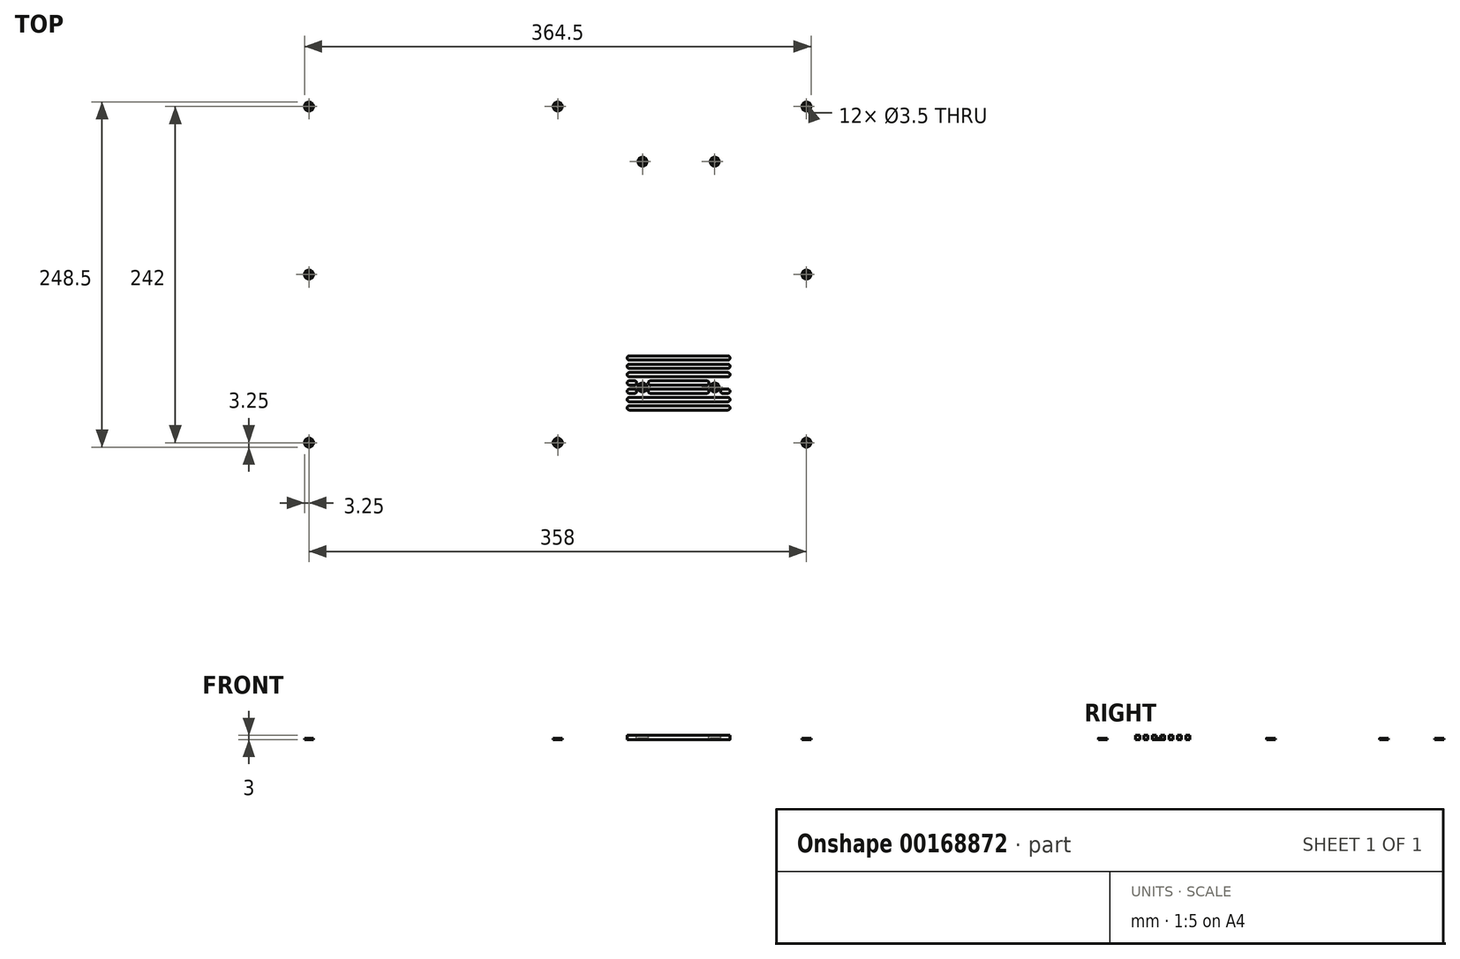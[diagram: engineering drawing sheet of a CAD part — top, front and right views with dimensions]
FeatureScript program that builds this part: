
annotation { "Feature Type Name" : "Feature", "Feature Type Description" : "" }
export const myFeature = defineFeature(function(context is Context, id is Id, definition is map)
    precondition{}
    {
        {
            var Q0;
            Q0=qCreatedBy(makeId("Top.planeOp"),FACE);
            var sketch = newSketch(context, id + "F0", { "sketchPlane" : qUnion([Q0])});
            skLineSegment(sketch, "E0.bottom", {"start": v(184, -126) * mm, "end": v(-184, -126) * mm});
            skLineSegment(sketch, "E0.top", {"start": v(184, 126) * mm, "end": v(-184, 126) * mm});
            skLineSegment(sketch, "E0.left", {"start": v(184, -126) * mm, "end": v(184, 126) * mm});
            skLineSegment(sketch, "E0.right", {"start": v(-184, -126) * mm, "end": v(-184, 126) * mm});
            skPoint(sketch, "E0.middle", {"position": v(0, 0) * mm});
            skLineSegment(sketch, "E1", {"start": v(-123, 245.59) * mm, "end": v(-123, -157.27) * mm, "construction": true});
            skLineSegment(sketch, "E2", {"start": v(-74.74, 270.76) * mm, "end": v(-74.74, -144.34) * mm, "construction": true});
            skLineSegment(sketch, "E3", {"start": v(-26.48, 143.4) * mm, "end": v(-26.48, -157.27) * mm, "construction": true});
            skLineSegment(sketch, "E4", {"start": v(-203.28, 67.26) * mm, "end": v(180.7, 67.26) * mm, "construction": true});
            skLineSegment(sketch, "E5", {"start": v(-202.8, 48.2) * mm, "end": v(185.48, 48.21) * mm, "construction": true});
            skLineSegment(sketch, "E6", {"start": v(-209.03, 29.16) * mm, "end": v(184.53, 29.16) * mm, "construction": true});
            skLineSegment(sketch, "E7.MirrorCS", {"start": v(-209.03, -29.16) * mm, "end": v(184.53, -29.16) * mm, "construction": true});
            skLineSegment(sketch, "E8.MirrorCS", {"start": v(-202.8, -48.2) * mm, "end": v(185.48, -48.21) * mm, "construction": true});
            skLineSegment(sketch, "E9.MirrorCS", {"start": v(-203.28, -67.26) * mm, "end": v(180.7, -67.26) * mm, "construction": true});
            skCircle(sketch, "E10", {"center": v(-123, 29.16) * mm, "radius": 11 * mm});
            skCircle(sketch, "E11", {"center": v(-74.74, 48.21) * mm, "radius": 11 * mm});
            skCircle(sketch, "E12", {"center": v(-123, -29.16) * mm, "radius": 11 * mm});
            skCircle(sketch, "E13", {"center": v(-74.74, -48.21) * mm, "radius": 11 * mm});
            skCircle(sketch, "E14", {"center": v(-26.48, -67.26) * mm, "radius": 11 * mm});
            skCircle(sketch, "E15", {"center": v(-26.48, 67.26) * mm, "radius": 11 * mm});
            skLineSegment(sketch, "E16.bottom", {"start": v(113, -39.5) * mm, "end": v(61, -39.5) * mm});
            skLineSegment(sketch, "E16.top", {"start": v(113, 39.5) * mm, "end": v(61, 39.5) * mm});
            skLineSegment(sketch, "E16.left", {"start": v(113, -39.5) * mm, "end": v(113, 39.5) * mm});
            skLineSegment(sketch, "E16.right", {"start": v(61, -39.5) * mm, "end": v(61, 39.5) * mm});
            skPoint(sketch, "E16.middle", {"position": v(87, 0) * mm});
            skLineSegment(sketch, "E17", {"start": v(55, 135.82) * mm, "end": v(55, -139) * mm, "construction": true});
            skLineSegment(sketch, "E18", {"start": v(119, 132.87) * mm, "end": v(119, -141.2) * mm, "construction": true});
            skLineSegment(sketch, "E19", {"start": v(35.75, 38) * mm, "end": v(185.31, 38) * mm, "construction": true});
            skLineSegment(sketch, "E20.MirrorCS", {"start": v(35.75, -38) * mm, "end": v(185.31, -38) * mm, "construction": true});
            skCircle(sketch, "E21", {"center": v(55, 38) * mm, "radius": 2.25 * mm});
            skCircle(sketch, "E22", {"center": v(119, 38) * mm, "radius": 2.25 * mm});
            skCircle(sketch, "E23", {"center": v(55, -38) * mm, "radius": 2.25 * mm});
            skCircle(sketch, "E24", {"center": v(119, -38) * mm, "radius": 2.25 * mm});
            skLineSegment(sketch, "E25", {"start": v(-171.66, 121) * mm, "end": v(177.1, 121) * mm, "construction": true});
            skLineSegment(sketch, "E26", {"start": v(-179, -132.6) * mm, "end": v(-179, 126) * mm, "construction": true});
            skLineSegment(sketch, "E27.MirrorCS", {"start": v(179, -132.6) * mm, "end": v(179, 126) * mm, "construction": true});
            skLineSegment(sketch, "E28.MirrorCS", {"start": v(-171.66, -121) * mm, "end": v(177.1, -121) * mm, "construction": true});
            skLineSegment(sketch, "E29", {"start": v(0, 148.7) * mm, "end": v(0, -121) * mm, "construction": true});
            skPoint(sketch, "E29.startSnap0", {"position": v(0, 126) * mm});
            skPoint(sketch, "E29.endSnap0", {"position": v(2.72, -121) * mm});
            skLineSegment(sketch, "E30", {"start": v(-194.49, 0) * mm, "end": v(184.92, 0) * mm, "construction": true});
            skPoint(sketch, "E30.startSnap0", {"position": v(-184, 0) * mm});
            skPoint(sketch, "E30.endSnap0", {"position": v(113, 0) * mm});
            skPoint(sketch, "E31", {"position": v(-179, 121) * mm});
            skPoint(sketch, "E32", {"position": v(0, 121) * mm});
            skPoint(sketch, "E33", {"position": v(-179, 0) * mm});
            skPoint(sketch, "E34", {"position": v(179, 121) * mm});
            skPoint(sketch, "E35", {"position": v(179, 0) * mm});
            skPoint(sketch, "E36", {"position": v(179, -121) * mm});
            skPoint(sketch, "E37", {"position": v(0, -121) * mm});
            skPoint(sketch, "E38", {"position": v(-179, -121) * mm});
            skLineSegment(sketch, "E39.bottom", {"start": v(-123, 50.16) * mm, "end": v(-123, 50.16) * mm});
            skLineSegment(sketch, "E39.top", {"start": v(-123, 43.16) * mm, "end": v(-123, 43.16) * mm});
            skLineSegment(sketch, "E39.left", {"start": v(-124, 49.16) * mm, "end": v(-124, 44.16) * mm});
            skLineSegment(sketch, "E39.right", {"start": v(-122, 49.16) * mm, "end": v(-122, 44.16) * mm});
            skPoint(sketch, "E40.visualSharp", {"position": v(-124, 50.16) * mm});
            skArc(sketch, "E40.filletArc", {"start": v(-123, 50.16) * mm, "mid": v(-123.7, 49.87) * mm, "end": v(-124, 49.16) * mm});
            skPoint(sketch, "E41.visualSharp", {"position": v(-122, 50.16) * mm});
            skArc(sketch, "E41.filletArc", {"start": v(-122, 49.16) * mm, "mid": v(-122.3, 49.87) * mm, "end": v(-123, 50.16) * mm});
            skPoint(sketch, "E42.visualSharp", {"position": v(-122, 43.16) * mm});
            skArc(sketch, "E42.filletArc", {"start": v(-123, 43.16) * mm, "mid": v(-122.3, 43.45) * mm, "end": v(-122, 44.16) * mm});
            skPoint(sketch, "E43.visualSharp", {"position": v(-124, 43.16) * mm});
            skArc(sketch, "E43.filletArc", {"start": v(-124, 44.16) * mm, "mid": v(-123.7, 43.45) * mm, "end": v(-123, 43.16) * mm});
            skLineSegment(sketch, "E44.bottom", {"start": v(-74.74, 69.21) * mm, "end": v(-74.74, 69.21) * mm});
            skLineSegment(sketch, "E44.top", {"start": v(-74.74, 62.21) * mm, "end": v(-74.74, 62.21) * mm});
            skLineSegment(sketch, "E44.left", {"start": v(-75.74, 68.21) * mm, "end": v(-75.74, 63.21) * mm});
            skLineSegment(sketch, "E44.right", {"start": v(-73.74, 68.21) * mm, "end": v(-73.74, 63.21) * mm});
            skPoint(sketch, "E45.visualSharp", {"position": v(-75.74, 69.21) * mm});
            skArc(sketch, "E45.filletArc", {"start": v(-74.74, 69.21) * mm, "mid": v(-75.45, 68.92) * mm, "end": v(-75.74, 68.21) * mm});
            skPoint(sketch, "E46.visualSharp", {"position": v(-73.74, 69.21) * mm});
            skArc(sketch, "E46.filletArc", {"start": v(-73.74, 68.21) * mm, "mid": v(-74.03, 68.92) * mm, "end": v(-74.74, 69.21) * mm});
            skPoint(sketch, "E47.visualSharp", {"position": v(-73.74, 62.21) * mm});
            skArc(sketch, "E47.filletArc", {"start": v(-74.74, 62.21) * mm, "mid": v(-74.03, 62.5) * mm, "end": v(-73.74, 63.21) * mm});
            skPoint(sketch, "E48.visualSharp", {"position": v(-75.74, 62.21) * mm});
            skArc(sketch, "E48.filletArc", {"start": v(-75.74, 63.21) * mm, "mid": v(-75.45, 62.5) * mm, "end": v(-74.74, 62.21) * mm});
            skLineSegment(sketch, "E49.bottom", {"start": v(-26.48, 88.26) * mm, "end": v(-26.48, 88.26) * mm});
            skLineSegment(sketch, "E49.top", {"start": v(-26.48, 81.26) * mm, "end": v(-26.48, 81.26) * mm});
            skLineSegment(sketch, "E49.left", {"start": v(-27.48, 87.26) * mm, "end": v(-27.48, 82.26) * mm});
            skLineSegment(sketch, "E49.right", {"start": v(-25.48, 87.26) * mm, "end": v(-25.48, 82.26) * mm});
            skPoint(sketch, "E50.visualSharp", {"position": v(-27.48, 88.26) * mm});
            skArc(sketch, "E50.filletArc", {"start": v(-26.48, 88.26) * mm, "mid": v(-27.19, 87.97) * mm, "end": v(-27.48, 87.26) * mm});
            skPoint(sketch, "E51.visualSharp", {"position": v(-25.48, 88.26) * mm});
            skArc(sketch, "E51.filletArc", {"start": v(-25.48, 87.26) * mm, "mid": v(-25.77, 87.97) * mm, "end": v(-26.48, 88.26) * mm});
            skPoint(sketch, "E52.visualSharp", {"position": v(-25.48, 81.26) * mm});
            skArc(sketch, "E52.filletArc", {"start": v(-26.48, 81.26) * mm, "mid": v(-25.77, 81.55) * mm, "end": v(-25.48, 82.26) * mm});
            skPoint(sketch, "E53.visualSharp", {"position": v(-27.48, 81.26) * mm});
            skArc(sketch, "E53.filletArc", {"start": v(-27.48, 82.26) * mm, "mid": v(-27.19, 81.55) * mm, "end": v(-26.48, 81.26) * mm});
            skLineSegment(sketch, "E54.bottom", {"start": v(-26.48, -46.26) * mm, "end": v(-26.48, -46.26) * mm});
            skLineSegment(sketch, "E54.top", {"start": v(-26.48, -53.26) * mm, "end": v(-26.48, -53.26) * mm});
            skLineSegment(sketch, "E54.left", {"start": v(-27.48, -47.26) * mm, "end": v(-27.48, -52.26) * mm});
            skLineSegment(sketch, "E54.right", {"start": v(-25.48, -47.26) * mm, "end": v(-25.48, -52.26) * mm});
            skPoint(sketch, "E55.visualSharp", {"position": v(-27.48, -46.26) * mm});
            skArc(sketch, "E55.filletArc", {"start": v(-26.48, -46.26) * mm, "mid": v(-27.19, -46.55) * mm, "end": v(-27.48, -47.26) * mm});
            skPoint(sketch, "E56.visualSharp", {"position": v(-25.48, -46.26) * mm});
            skArc(sketch, "E56.filletArc", {"start": v(-25.48, -47.26) * mm, "mid": v(-25.77, -46.55) * mm, "end": v(-26.48, -46.26) * mm});
            skPoint(sketch, "E57.visualSharp", {"position": v(-25.48, -53.26) * mm});
            skArc(sketch, "E57.filletArc", {"start": v(-26.48, -53.26) * mm, "mid": v(-25.77, -52.97) * mm, "end": v(-25.48, -52.26) * mm});
            skPoint(sketch, "E58.visualSharp", {"position": v(-27.48, -53.26) * mm});
            skArc(sketch, "E58.filletArc", {"start": v(-27.48, -52.26) * mm, "mid": v(-27.19, -52.97) * mm, "end": v(-26.48, -53.26) * mm});
            skLineSegment(sketch, "E59.bottom", {"start": v(-74.74, -27.21) * mm, "end": v(-74.74, -27.21) * mm});
            skLineSegment(sketch, "E59.top", {"start": v(-74.74, -34.21) * mm, "end": v(-74.74, -34.21) * mm});
            skLineSegment(sketch, "E59.left", {"start": v(-75.74, -28.21) * mm, "end": v(-75.74, -33.21) * mm});
            skLineSegment(sketch, "E59.right", {"start": v(-73.74, -28.21) * mm, "end": v(-73.74, -33.21) * mm});
            skPoint(sketch, "E60.visualSharp", {"position": v(-75.74, -27.21) * mm});
            skArc(sketch, "E60.filletArc", {"start": v(-74.74, -27.21) * mm, "mid": v(-75.45, -27.5) * mm, "end": v(-75.74, -28.21) * mm});
            skPoint(sketch, "E61.visualSharp", {"position": v(-73.74, -27.21) * mm});
            skArc(sketch, "E61.filletArc", {"start": v(-73.74, -28.21) * mm, "mid": v(-74.03, -27.5) * mm, "end": v(-74.74, -27.21) * mm});
            skPoint(sketch, "E62.visualSharp", {"position": v(-73.74, -34.21) * mm});
            skArc(sketch, "E62.filletArc", {"start": v(-74.74, -34.21) * mm, "mid": v(-74.03, -33.92) * mm, "end": v(-73.74, -33.21) * mm});
            skPoint(sketch, "E63.visualSharp", {"position": v(-75.74, -34.21) * mm});
            skArc(sketch, "E63.filletArc", {"start": v(-75.74, -33.21) * mm, "mid": v(-75.45, -33.92) * mm, "end": v(-74.74, -34.21) * mm});
            skLineSegment(sketch, "E64.bottom", {"start": v(-123, -8.16) * mm, "end": v(-123, -8.16) * mm});
            skLineSegment(sketch, "E64.top", {"start": v(-123, -15.16) * mm, "end": v(-123, -15.16) * mm});
            skLineSegment(sketch, "E64.left", {"start": v(-124, -9.16) * mm, "end": v(-124, -14.16) * mm});
            skLineSegment(sketch, "E64.right", {"start": v(-122, -9.16) * mm, "end": v(-122, -14.16) * mm});
            skPoint(sketch, "E65.visualSharp", {"position": v(-124, -8.16) * mm});
            skArc(sketch, "E65.filletArc", {"start": v(-123, -8.16) * mm, "mid": v(-123.7, -8.45) * mm, "end": v(-124, -9.16) * mm});
            skPoint(sketch, "E66.visualSharp", {"position": v(-122, -8.16) * mm});
            skArc(sketch, "E66.filletArc", {"start": v(-122, -9.16) * mm, "mid": v(-122.3, -8.45) * mm, "end": v(-123, -8.16) * mm});
            skPoint(sketch, "E67.visualSharp", {"position": v(-122, -15.16) * mm});
            skArc(sketch, "E67.filletArc", {"start": v(-123, -15.16) * mm, "mid": v(-122.3, -14.87) * mm, "end": v(-122, -14.16) * mm});
            skPoint(sketch, "E68.visualSharp", {"position": v(-124, -15.16) * mm});
            skArc(sketch, "E68.filletArc", {"start": v(-124, -14.16) * mm, "mid": v(-123.7, -14.87) * mm, "end": v(-123, -15.16) * mm});
            skLineSegment(sketch, "E69.1.0", {"start": v(-128.23, 48.5) * mm, "end": v(-126.68, 43.73) * mm});
            skArc(sketch, "E69.1.1", {"start": v(-128.59, 43.12) * mm, "mid": v(-128.09, 42.53) * mm, "end": v(-127.33, 42.47) * mm});
            skPoint(sketch, "E69.1.2", {"position": v(-126.38, 42.78) * mm});
            skArc(sketch, "E69.1.3", {"start": v(-127.33, 42.47) * mm, "mid": v(-126.74, 42.97) * mm, "end": v(-126.68, 43.73) * mm});
            skPoint(sketch, "E69.1.4", {"position": v(-128.28, 42.17) * mm});
            skLineSegment(sketch, "E69.1.5", {"start": v(-130.13, 47.87) * mm, "end": v(-128.59, 43.12) * mm});
            skPoint(sketch, "E69.1.6", {"position": v(-130.44, 48.82) * mm});
            skArc(sketch, "E69.1.7", {"start": v(-129.49, 49.13) * mm, "mid": v(-130.07, 48.64) * mm, "end": v(-130.13, 47.87) * mm});
            skPoint(sketch, "E69.1.8", {"position": v(-128.54, 49.44) * mm});
            skArc(sketch, "E69.1.9", {"start": v(-128.23, 48.5) * mm, "mid": v(-128.73, 49.07) * mm, "end": v(-129.49, 49.13) * mm});
            skLineSegment(sketch, "E69.2.0", {"start": v(-133.95, 45.93) * mm, "end": v(-131, 41.88) * mm});
            skArc(sketch, "E69.2.1", {"start": v(-132.63, 40.7) * mm, "mid": v(-131.97, 40.3) * mm, "end": v(-131.23, 40.49) * mm});
            skPoint(sketch, "E69.2.2", {"position": v(-130.42, 41.07) * mm});
            skArc(sketch, "E69.2.3", {"start": v(-131.23, 40.49) * mm, "mid": v(-130.83, 41.14) * mm, "end": v(-131, 41.88) * mm});
            skPoint(sketch, "E69.2.4", {"position": v(-132.04, 39.9) * mm});
            skLineSegment(sketch, "E69.2.5", {"start": v(-135.56, 44.75) * mm, "end": v(-132.63, 40.7) * mm});
            skPoint(sketch, "E69.2.6", {"position": v(-136.15, 45.56) * mm});
            skArc(sketch, "E69.2.7", {"start": v(-135.34, 46.15) * mm, "mid": v(-135.74, 45.5) * mm, "end": v(-135.56, 44.75) * mm});
            skPoint(sketch, "E69.2.8", {"position": v(-134.53, 46.74) * mm});
            skArc(sketch, "E69.2.9", {"start": v(-133.95, 45.93) * mm, "mid": v(-134.6, 46.33) * mm, "end": v(-135.34, 46.15) * mm});
            skLineSegment(sketch, "E69.3.0", {"start": v(-138.6, 41.72) * mm, "end": v(-134.55, 38.79) * mm});
            skArc(sketch, "E69.3.1", {"start": v(-135.72, 37.17) * mm, "mid": v(-134.98, 36.99) * mm, "end": v(-134.33, 37.39) * mm});
            skPoint(sketch, "E69.3.2", {"position": v(-133.74, 38.2) * mm});
            skArc(sketch, "E69.3.3", {"start": v(-134.33, 37.39) * mm, "mid": v(-134.15, 38.13) * mm, "end": v(-134.55, 38.79) * mm});
            skPoint(sketch, "E69.3.4", {"position": v(-134.91, 36.58) * mm});
            skLineSegment(sketch, "E69.3.5", {"start": v(-139.77, 40.1) * mm, "end": v(-135.72, 37.17) * mm});
            skPoint(sketch, "E69.3.6", {"position": v(-140.58, 40.7) * mm});
            skArc(sketch, "E69.3.7", {"start": v(-139.99, 41.5) * mm, "mid": v(-140.17, 40.76) * mm, "end": v(-139.77, 40.1) * mm});
            skPoint(sketch, "E69.3.8", {"position": v(-139.4, 42.31) * mm});
            skArc(sketch, "E69.3.9", {"start": v(-138.6, 41.72) * mm, "mid": v(-139.34, 41.9) * mm, "end": v(-139.99, 41.5) * mm});
            skLineSegment(sketch, "E69.4.0", {"start": v(-141.71, 36.3) * mm, "end": v(-136.96, 34.75) * mm});
            skArc(sketch, "E69.4.1", {"start": v(-137.57, 32.84) * mm, "mid": v(-136.81, 32.9) * mm, "end": v(-136.31, 33.49) * mm});
            skPoint(sketch, "E69.4.2", {"position": v(-136, 34.44) * mm});
            skArc(sketch, "E69.4.3", {"start": v(-136.31, 33.49) * mm, "mid": v(-136.37, 34.25) * mm, "end": v(-136.96, 34.75) * mm});
            skPoint(sketch, "E69.4.4", {"position": v(-136.62, 32.54) * mm});
            skLineSegment(sketch, "E69.4.5", {"start": v(-142.33, 34.39) * mm, "end": v(-137.57, 32.84) * mm});
            skPoint(sketch, "E69.4.6", {"position": v(-143.28, 34.7) * mm});
            skArc(sketch, "E69.4.7", {"start": v(-142.97, 35.65) * mm, "mid": v(-142.91, 34.89) * mm, "end": v(-142.33, 34.39) * mm});
            skPoint(sketch, "E69.4.8", {"position": v(-142.66, 36.6) * mm});
            skArc(sketch, "E69.4.9", {"start": v(-141.71, 36.3) * mm, "mid": v(-142.48, 36.23) * mm, "end": v(-142.97, 35.65) * mm});
            skLineSegment(sketch, "E69.5.0", {"start": v(-143, 30.16) * mm, "end": v(-138, 30.16) * mm});
            skArc(sketch, "E69.5.1", {"start": v(-138, 28.16) * mm, "mid": v(-137.3, 28.45) * mm, "end": v(-137, 29.16) * mm});
            skPoint(sketch, "E69.5.2", {"position": v(-137, 30.16) * mm});
            skArc(sketch, "E69.5.3", {"start": v(-137, 29.16) * mm, "mid": v(-137.3, 29.87) * mm, "end": v(-138, 30.16) * mm});
            skPoint(sketch, "E69.5.4", {"position": v(-137, 28.16) * mm});
            skLineSegment(sketch, "E69.5.5", {"start": v(-143, 28.16) * mm, "end": v(-138, 28.16) * mm});
            skPoint(sketch, "E69.5.6", {"position": v(-144, 28.16) * mm});
            skArc(sketch, "E69.5.7", {"start": v(-144, 29.16) * mm, "mid": v(-143.7, 28.45) * mm, "end": v(-143, 28.16) * mm});
            skPoint(sketch, "E69.5.8", {"position": v(-144, 30.16) * mm});
            skArc(sketch, "E69.5.9", {"start": v(-143, 30.16) * mm, "mid": v(-143.7, 29.87) * mm, "end": v(-144, 29.16) * mm});
            skLineSegment(sketch, "E69.6.0", {"start": v(-142.33, 23.93) * mm, "end": v(-137.57, 25.48) * mm});
            skArc(sketch, "E69.6.1", {"start": v(-136.96, 23.57) * mm, "mid": v(-136.37, 24.07) * mm, "end": v(-136.31, 24.83) * mm});
            skPoint(sketch, "E69.6.2", {"position": v(-136.62, 25.78) * mm});
            skArc(sketch, "E69.6.3", {"start": v(-136.31, 24.83) * mm, "mid": v(-136.81, 25.42) * mm, "end": v(-137.57, 25.48) * mm});
            skPoint(sketch, "E69.6.4", {"position": v(-136, 23.88) * mm});
            skLineSegment(sketch, "E69.6.5", {"start": v(-141.71, 22.03) * mm, "end": v(-136.96, 23.57) * mm});
            skPoint(sketch, "E69.6.6", {"position": v(-142.66, 21.72) * mm});
            skArc(sketch, "E69.6.7", {"start": v(-142.97, 22.67) * mm, "mid": v(-142.48, 22.09) * mm, "end": v(-141.71, 22.03) * mm});
            skPoint(sketch, "E69.6.8", {"position": v(-143.28, 23.62) * mm});
            skArc(sketch, "E69.6.9", {"start": v(-142.33, 23.93) * mm, "mid": v(-142.91, 23.43) * mm, "end": v(-142.97, 22.67) * mm});
            skLineSegment(sketch, "E69.7.0", {"start": v(-139.77, 18.21) * mm, "end": v(-135.72, 21.15) * mm});
            skArc(sketch, "E69.7.1", {"start": v(-134.55, 19.53) * mm, "mid": v(-134.15, 20.19) * mm, "end": v(-134.33, 20.93) * mm});
            skPoint(sketch, "E69.7.2", {"position": v(-134.91, 21.74) * mm});
            skArc(sketch, "E69.7.3", {"start": v(-134.33, 20.93) * mm, "mid": v(-134.98, 21.33) * mm, "end": v(-135.72, 21.15) * mm});
            skPoint(sketch, "E69.7.4", {"position": v(-133.74, 20.12) * mm});
            skLineSegment(sketch, "E69.7.5", {"start": v(-138.6, 16.6) * mm, "end": v(-134.55, 19.53) * mm});
            skPoint(sketch, "E69.7.6", {"position": v(-139.4, 16) * mm});
            skArc(sketch, "E69.7.7", {"start": v(-139.99, 16.82) * mm, "mid": v(-139.34, 16.42) * mm, "end": v(-138.6, 16.6) * mm});
            skPoint(sketch, "E69.7.8", {"position": v(-140.58, 17.63) * mm});
            skArc(sketch, "E69.7.9", {"start": v(-139.77, 18.21) * mm, "mid": v(-140.17, 17.56) * mm, "end": v(-139.99, 16.82) * mm});
            skLineSegment(sketch, "E69.8.0", {"start": v(-135.56, 13.57) * mm, "end": v(-132.63, 17.61) * mm});
            skArc(sketch, "E69.8.1", {"start": v(-131, 16.44) * mm, "mid": v(-130.83, 17.18) * mm, "end": v(-131.23, 17.83) * mm});
            skPoint(sketch, "E69.8.2", {"position": v(-132.04, 18.42) * mm});
            skArc(sketch, "E69.8.3", {"start": v(-131.23, 17.83) * mm, "mid": v(-131.97, 18.01) * mm, "end": v(-132.63, 17.61) * mm});
            skPoint(sketch, "E69.8.4", {"position": v(-130.42, 17.25) * mm});
            skLineSegment(sketch, "E69.8.5", {"start": v(-133.95, 12.4) * mm, "end": v(-131, 16.44) * mm});
            skPoint(sketch, "E69.8.6", {"position": v(-134.53, 11.58) * mm});
            skArc(sketch, "E69.8.7", {"start": v(-135.34, 12.17) * mm, "mid": v(-134.6, 12) * mm, "end": v(-133.95, 12.4) * mm});
            skPoint(sketch, "E69.8.8", {"position": v(-136.15, 12.76) * mm});
            skArc(sketch, "E69.8.9", {"start": v(-135.56, 13.57) * mm, "mid": v(-135.74, 12.82) * mm, "end": v(-135.34, 12.17) * mm});
            skLineSegment(sketch, "E69.9.0", {"start": v(-130.13, 10.45) * mm, "end": v(-128.59, 15.2) * mm});
            skArc(sketch, "E69.9.1", {"start": v(-126.68, 14.59) * mm, "mid": v(-126.74, 15.35) * mm, "end": v(-127.33, 15.85) * mm});
            skPoint(sketch, "E69.9.2", {"position": v(-128.28, 16.15) * mm});
            skArc(sketch, "E69.9.3", {"start": v(-127.33, 15.85) * mm, "mid": v(-128.09, 15.79) * mm, "end": v(-128.59, 15.2) * mm});
            skPoint(sketch, "E69.9.4", {"position": v(-126.38, 15.54) * mm});
            skLineSegment(sketch, "E69.9.5", {"start": v(-128.23, 9.83) * mm, "end": v(-126.68, 14.59) * mm});
            skPoint(sketch, "E69.9.6", {"position": v(-128.54, 8.88) * mm});
            skArc(sketch, "E69.9.7", {"start": v(-129.49, 9.19) * mm, "mid": v(-128.73, 9.25) * mm, "end": v(-128.23, 9.83) * mm});
            skPoint(sketch, "E69.9.8", {"position": v(-130.44, 9.5) * mm});
            skArc(sketch, "E69.9.9", {"start": v(-130.13, 10.45) * mm, "mid": v(-130.07, 9.68) * mm, "end": v(-129.49, 9.19) * mm});
            skLineSegment(sketch, "E69.10.0", {"start": v(-124, 9.16) * mm, "end": v(-124, 14.16) * mm});
            skArc(sketch, "E69.10.1", {"start": v(-122, 14.16) * mm, "mid": v(-122.3, 14.87) * mm, "end": v(-123, 15.16) * mm});
            skPoint(sketch, "E69.10.2", {"position": v(-124, 15.16) * mm});
            skArc(sketch, "E69.10.3", {"start": v(-123, 15.16) * mm, "mid": v(-123.7, 14.87) * mm, "end": v(-124, 14.16) * mm});
            skPoint(sketch, "E69.10.4", {"position": v(-122, 15.16) * mm});
            skLineSegment(sketch, "E69.10.5", {"start": v(-122, 9.16) * mm, "end": v(-122, 14.16) * mm});
            skPoint(sketch, "E69.10.6", {"position": v(-122, 8.16) * mm});
            skArc(sketch, "E69.10.7", {"start": v(-123, 8.16) * mm, "mid": v(-122.3, 8.45) * mm, "end": v(-122, 9.16) * mm});
            skPoint(sketch, "E69.10.8", {"position": v(-124, 8.16) * mm});
            skArc(sketch, "E69.10.9", {"start": v(-124, 9.16) * mm, "mid": v(-123.7, 8.45) * mm, "end": v(-123, 8.16) * mm});
            skLineSegment(sketch, "E69.11.0", {"start": v(-117.77, 9.83) * mm, "end": v(-119.32, 14.59) * mm});
            skArc(sketch, "E69.11.1", {"start": v(-117.41, 15.2) * mm, "mid": v(-117.91, 15.79) * mm, "end": v(-118.67, 15.85) * mm});
            skPoint(sketch, "E69.11.2", {"position": v(-119.62, 15.54) * mm});
            skArc(sketch, "E69.11.3", {"start": v(-118.67, 15.85) * mm, "mid": v(-119.26, 15.35) * mm, "end": v(-119.32, 14.59) * mm});
            skPoint(sketch, "E69.11.4", {"position": v(-117.72, 16.15) * mm});
            skLineSegment(sketch, "E69.11.5", {"start": v(-115.87, 10.45) * mm, "end": v(-117.41, 15.2) * mm});
            skPoint(sketch, "E69.11.6", {"position": v(-115.56, 9.5) * mm});
            skArc(sketch, "E69.11.7", {"start": v(-116.51, 9.19) * mm, "mid": v(-115.93, 9.68) * mm, "end": v(-115.87, 10.45) * mm});
            skPoint(sketch, "E69.11.8", {"position": v(-117.46, 8.88) * mm});
            skArc(sketch, "E69.11.9", {"start": v(-117.77, 9.83) * mm, "mid": v(-117.27, 9.25) * mm, "end": v(-116.51, 9.19) * mm});
            skLineSegment(sketch, "E69.12.0", {"start": v(-112.05, 12.4) * mm, "end": v(-115, 16.44) * mm});
            skArc(sketch, "E69.12.1", {"start": v(-113.37, 17.61) * mm, "mid": v(-114.03, 18.01) * mm, "end": v(-114.77, 17.83) * mm});
            skPoint(sketch, "E69.12.2", {"position": v(-115.58, 17.25) * mm});
            skArc(sketch, "E69.12.3", {"start": v(-114.77, 17.83) * mm, "mid": v(-115.17, 17.18) * mm, "end": v(-115, 16.44) * mm});
            skPoint(sketch, "E69.12.4", {"position": v(-113.96, 18.42) * mm});
            skLineSegment(sketch, "E69.12.5", {"start": v(-110.44, 13.57) * mm, "end": v(-113.37, 17.61) * mm});
            skPoint(sketch, "E69.12.6", {"position": v(-109.85, 12.76) * mm});
            skArc(sketch, "E69.12.7", {"start": v(-110.66, 12.17) * mm, "mid": v(-110.26, 12.82) * mm, "end": v(-110.44, 13.57) * mm});
            skPoint(sketch, "E69.12.8", {"position": v(-111.47, 11.58) * mm});
            skArc(sketch, "E69.12.9", {"start": v(-112.05, 12.4) * mm, "mid": v(-111.4, 12) * mm, "end": v(-110.66, 12.17) * mm});
            skLineSegment(sketch, "E69.13.0", {"start": v(-107.4, 16.6) * mm, "end": v(-111.45, 19.53) * mm});
            skArc(sketch, "E69.13.1", {"start": v(-110.28, 21.15) * mm, "mid": v(-111.02, 21.33) * mm, "end": v(-111.67, 20.93) * mm});
            skPoint(sketch, "E69.13.2", {"position": v(-112.26, 20.12) * mm});
            skArc(sketch, "E69.13.3", {"start": v(-111.67, 20.93) * mm, "mid": v(-111.85, 20.19) * mm, "end": v(-111.45, 19.53) * mm});
            skPoint(sketch, "E69.13.4", {"position": v(-111.09, 21.74) * mm});
            skLineSegment(sketch, "E69.13.5", {"start": v(-106.23, 18.21) * mm, "end": v(-110.28, 21.15) * mm});
            skPoint(sketch, "E69.13.6", {"position": v(-105.42, 17.63) * mm});
            skArc(sketch, "E69.13.7", {"start": v(-106.01, 16.82) * mm, "mid": v(-105.83, 17.56) * mm, "end": v(-106.23, 18.21) * mm});
            skPoint(sketch, "E69.13.8", {"position": v(-106.6, 16) * mm});
            skArc(sketch, "E69.13.9", {"start": v(-107.4, 16.6) * mm, "mid": v(-106.66, 16.42) * mm, "end": v(-106.01, 16.82) * mm});
            skLineSegment(sketch, "E69.14.0", {"start": v(-104.29, 22.03) * mm, "end": v(-109.04, 23.57) * mm});
            skArc(sketch, "E69.14.1", {"start": v(-108.43, 25.48) * mm, "mid": v(-109.19, 25.42) * mm, "end": v(-109.69, 24.83) * mm});
            skPoint(sketch, "E69.14.2", {"position": v(-110, 23.88) * mm});
            skArc(sketch, "E69.14.3", {"start": v(-109.69, 24.83) * mm, "mid": v(-109.63, 24.07) * mm, "end": v(-109.04, 23.57) * mm});
            skPoint(sketch, "E69.14.4", {"position": v(-109.38, 25.78) * mm});
            skLineSegment(sketch, "E69.14.5", {"start": v(-103.67, 23.93) * mm, "end": v(-108.43, 25.48) * mm});
            skPoint(sketch, "E69.14.6", {"position": v(-102.72, 23.62) * mm});
            skArc(sketch, "E69.14.7", {"start": v(-103.03, 22.67) * mm, "mid": v(-103.09, 23.43) * mm, "end": v(-103.67, 23.93) * mm});
            skPoint(sketch, "E69.14.8", {"position": v(-103.34, 21.72) * mm});
            skArc(sketch, "E69.14.9", {"start": v(-104.29, 22.03) * mm, "mid": v(-103.52, 22.09) * mm, "end": v(-103.03, 22.67) * mm});
            skLineSegment(sketch, "E69.15.0", {"start": v(-103, 28.16) * mm, "end": v(-108, 28.16) * mm});
            skArc(sketch, "E69.15.1", {"start": v(-108, 30.16) * mm, "mid": v(-108.7, 29.87) * mm, "end": v(-109, 29.16) * mm});
            skPoint(sketch, "E69.15.2", {"position": v(-109, 28.16) * mm});
            skArc(sketch, "E69.15.3", {"start": v(-109, 29.16) * mm, "mid": v(-108.7, 28.45) * mm, "end": v(-108, 28.16) * mm});
            skPoint(sketch, "E69.15.4", {"position": v(-109, 30.16) * mm});
            skLineSegment(sketch, "E69.15.5", {"start": v(-103, 30.16) * mm, "end": v(-108, 30.16) * mm});
            skPoint(sketch, "E69.15.6", {"position": v(-102, 30.16) * mm});
            skArc(sketch, "E69.15.7", {"start": v(-102, 29.16) * mm, "mid": v(-102.3, 29.87) * mm, "end": v(-103, 30.16) * mm});
            skPoint(sketch, "E69.15.8", {"position": v(-102, 28.16) * mm});
            skArc(sketch, "E69.15.9", {"start": v(-103, 28.16) * mm, "mid": v(-102.3, 28.45) * mm, "end": v(-102, 29.16) * mm});
            skLineSegment(sketch, "E69.16.0", {"start": v(-103.67, 34.39) * mm, "end": v(-108.43, 32.84) * mm});
            skArc(sketch, "E69.16.1", {"start": v(-109.04, 34.75) * mm, "mid": v(-109.63, 34.25) * mm, "end": v(-109.69, 33.49) * mm});
            skPoint(sketch, "E69.16.2", {"position": v(-109.38, 32.54) * mm});
            skArc(sketch, "E69.16.3", {"start": v(-109.69, 33.49) * mm, "mid": v(-109.19, 32.9) * mm, "end": v(-108.43, 32.84) * mm});
            skPoint(sketch, "E69.16.4", {"position": v(-110, 34.44) * mm});
            skLineSegment(sketch, "E69.16.5", {"start": v(-104.29, 36.3) * mm, "end": v(-109.04, 34.75) * mm});
            skPoint(sketch, "E69.16.6", {"position": v(-103.34, 36.6) * mm});
            skArc(sketch, "E69.16.7", {"start": v(-103.03, 35.65) * mm, "mid": v(-103.52, 36.23) * mm, "end": v(-104.29, 36.3) * mm});
            skPoint(sketch, "E69.16.8", {"position": v(-102.72, 34.7) * mm});
            skArc(sketch, "E69.16.9", {"start": v(-103.67, 34.39) * mm, "mid": v(-103.09, 34.89) * mm, "end": v(-103.03, 35.65) * mm});
            skLineSegment(sketch, "E69.17.0", {"start": v(-106.23, 40.1) * mm, "end": v(-110.28, 37.17) * mm});
            skArc(sketch, "E69.17.1", {"start": v(-111.45, 38.79) * mm, "mid": v(-111.85, 38.13) * mm, "end": v(-111.67, 37.39) * mm});
            skPoint(sketch, "E69.17.2", {"position": v(-111.09, 36.58) * mm});
            skArc(sketch, "E69.17.3", {"start": v(-111.67, 37.39) * mm, "mid": v(-111.02, 36.99) * mm, "end": v(-110.28, 37.17) * mm});
            skPoint(sketch, "E69.17.4", {"position": v(-112.26, 38.2) * mm});
            skLineSegment(sketch, "E69.17.5", {"start": v(-107.4, 41.72) * mm, "end": v(-111.45, 38.79) * mm});
            skPoint(sketch, "E69.17.6", {"position": v(-106.6, 42.31) * mm});
            skArc(sketch, "E69.17.7", {"start": v(-106.01, 41.5) * mm, "mid": v(-106.66, 41.9) * mm, "end": v(-107.4, 41.72) * mm});
            skPoint(sketch, "E69.17.8", {"position": v(-105.42, 40.7) * mm});
            skArc(sketch, "E69.17.9", {"start": v(-106.23, 40.1) * mm, "mid": v(-105.83, 40.76) * mm, "end": v(-106.01, 41.5) * mm});
            skLineSegment(sketch, "E69.18.0", {"start": v(-110.44, 44.75) * mm, "end": v(-113.37, 40.7) * mm});
            skArc(sketch, "E69.18.1", {"start": v(-115, 41.88) * mm, "mid": v(-115.17, 41.14) * mm, "end": v(-114.77, 40.49) * mm});
            skPoint(sketch, "E69.18.2", {"position": v(-113.96, 39.9) * mm});
            skArc(sketch, "E69.18.3", {"start": v(-114.77, 40.49) * mm, "mid": v(-114.03, 40.3) * mm, "end": v(-113.37, 40.7) * mm});
            skPoint(sketch, "E69.18.4", {"position": v(-115.58, 41.07) * mm});
            skLineSegment(sketch, "E69.18.5", {"start": v(-112.05, 45.93) * mm, "end": v(-115, 41.88) * mm});
            skPoint(sketch, "E69.18.6", {"position": v(-111.47, 46.74) * mm});
            skArc(sketch, "E69.18.7", {"start": v(-110.66, 46.15) * mm, "mid": v(-111.4, 46.33) * mm, "end": v(-112.05, 45.93) * mm});
            skPoint(sketch, "E69.18.8", {"position": v(-109.85, 45.56) * mm});
            skArc(sketch, "E69.18.9", {"start": v(-110.44, 44.75) * mm, "mid": v(-110.26, 45.5) * mm, "end": v(-110.66, 46.15) * mm});
            skLineSegment(sketch, "E69.19.0", {"start": v(-115.87, 47.87) * mm, "end": v(-117.41, 43.12) * mm});
            skArc(sketch, "E69.19.1", {"start": v(-119.32, 43.73) * mm, "mid": v(-119.26, 42.97) * mm, "end": v(-118.67, 42.47) * mm});
            skPoint(sketch, "E69.19.2", {"position": v(-117.72, 42.17) * mm});
            skArc(sketch, "E69.19.3", {"start": v(-118.67, 42.47) * mm, "mid": v(-117.91, 42.53) * mm, "end": v(-117.41, 43.12) * mm});
            skPoint(sketch, "E69.19.4", {"position": v(-119.62, 42.78) * mm});
            skLineSegment(sketch, "E69.19.5", {"start": v(-117.77, 48.5) * mm, "end": v(-119.32, 43.73) * mm});
            skPoint(sketch, "E69.19.6", {"position": v(-117.46, 49.44) * mm});
            skArc(sketch, "E69.19.7", {"start": v(-116.51, 49.13) * mm, "mid": v(-117.27, 49.07) * mm, "end": v(-117.77, 48.5) * mm});
            skPoint(sketch, "E69.19.8", {"position": v(-115.56, 48.82) * mm});
            skArc(sketch, "E69.19.9", {"start": v(-115.87, 47.87) * mm, "mid": v(-115.93, 48.64) * mm, "end": v(-116.51, 49.13) * mm});
            skLineSegment(sketch, "E70.1.0", {"start": v(-79.97, 67.54) * mm, "end": v(-78.42, 62.78) * mm});
            skLineSegment(sketch, "E70.1.1", {"start": v(-81.87, 66.92) * mm, "end": v(-80.33, 62.17) * mm});
            skPoint(sketch, "E70.1.2", {"position": v(-80.02, 61.22) * mm});
            skPoint(sketch, "E70.1.3", {"position": v(-78.12, 61.83) * mm});
            skArc(sketch, "E70.1.4", {"start": v(-80.33, 62.17) * mm, "mid": v(-79.83, 61.58) * mm, "end": v(-79.07, 61.52) * mm});
            skArc(sketch, "E70.1.5", {"start": v(-79.07, 61.52) * mm, "mid": v(-78.48, 62.02) * mm, "end": v(-78.42, 62.78) * mm});
            skPoint(sketch, "E70.1.6", {"position": v(-82.18, 67.87) * mm});
            skPoint(sketch, "E70.1.7", {"position": v(-80.28, 68.5) * mm});
            skArc(sketch, "E70.1.8", {"start": v(-79.97, 67.54) * mm, "mid": v(-80.47, 68.12) * mm, "end": v(-81.23, 68.18) * mm});
            skArc(sketch, "E70.1.9", {"start": v(-81.23, 68.18) * mm, "mid": v(-81.81, 67.69) * mm, "end": v(-81.87, 66.92) * mm});
            skLineSegment(sketch, "E70.2.0", {"start": v(-85.69, 64.98) * mm, "end": v(-82.75, 60.93) * mm});
            skLineSegment(sketch, "E70.2.1", {"start": v(-87.3, 63.8) * mm, "end": v(-84.37, 59.76) * mm});
            skPoint(sketch, "E70.2.2", {"position": v(-83.78, 58.95) * mm});
            skPoint(sketch, "E70.2.3", {"position": v(-82.16, 60.12) * mm});
            skArc(sketch, "E70.2.4", {"start": v(-84.37, 59.76) * mm, "mid": v(-83.71, 59.36) * mm, "end": v(-82.97, 59.54) * mm});
            skArc(sketch, "E70.2.5", {"start": v(-82.97, 59.54) * mm, "mid": v(-82.57, 60.19) * mm, "end": v(-82.75, 60.93) * mm});
            skPoint(sketch, "E70.2.6", {"position": v(-87.9, 64.61) * mm});
            skPoint(sketch, "E70.2.7", {"position": v(-86.27, 65.79) * mm});
            skArc(sketch, "E70.2.8", {"start": v(-85.69, 64.98) * mm, "mid": v(-86.34, 65.38) * mm, "end": v(-87.08, 65.2) * mm});
            skArc(sketch, "E70.2.9", {"start": v(-87.08, 65.2) * mm, "mid": v(-87.48, 64.55) * mm, "end": v(-87.3, 63.8) * mm});
            skLineSegment(sketch, "E70.3.0", {"start": v(-90.33, 60.77) * mm, "end": v(-86.29, 57.84) * mm});
            skLineSegment(sketch, "E70.3.1", {"start": v(-91.5, 59.16) * mm, "end": v(-87.46, 56.22) * mm});
            skPoint(sketch, "E70.3.2", {"position": v(-86.65, 55.63) * mm});
            skPoint(sketch, "E70.3.3", {"position": v(-85.48, 57.25) * mm});
            skArc(sketch, "E70.3.4", {"start": v(-87.46, 56.22) * mm, "mid": v(-86.72, 56.04) * mm, "end": v(-86.07, 56.44) * mm});
            skArc(sketch, "E70.3.5", {"start": v(-86.07, 56.44) * mm, "mid": v(-85.89, 57.18) * mm, "end": v(-86.29, 57.84) * mm});
            skPoint(sketch, "E70.3.6", {"position": v(-92.32, 59.74) * mm});
            skPoint(sketch, "E70.3.7", {"position": v(-91.14, 61.36) * mm});
            skArc(sketch, "E70.3.8", {"start": v(-90.33, 60.77) * mm, "mid": v(-91.08, 60.95) * mm, "end": v(-91.73, 60.55) * mm});
            skArc(sketch, "E70.3.9", {"start": v(-91.73, 60.55) * mm, "mid": v(-91.9, 59.8) * mm, "end": v(-91.5, 59.16) * mm});
            skLineSegment(sketch, "E70.4.0", {"start": v(-93.45, 55.34) * mm, "end": v(-88.7, 53.8) * mm});
            skLineSegment(sketch, "E70.4.1", {"start": v(-94.07, 53.44) * mm, "end": v(-89.31, 51.9) * mm});
            skPoint(sketch, "E70.4.2", {"position": v(-88.36, 51.59) * mm});
            skPoint(sketch, "E70.4.3", {"position": v(-87.75, 53.49) * mm});
            skArc(sketch, "E70.4.4", {"start": v(-89.31, 51.9) * mm, "mid": v(-88.55, 51.95) * mm, "end": v(-88.05, 52.54) * mm});
            skArc(sketch, "E70.4.5", {"start": v(-88.05, 52.54) * mm, "mid": v(-88.11, 53.3) * mm, "end": v(-88.7, 53.8) * mm});
            skPoint(sketch, "E70.4.6", {"position": v(-95.02, 53.75) * mm});
            skPoint(sketch, "E70.4.7", {"position": v(-94.4, 55.65) * mm});
            skArc(sketch, "E70.4.8", {"start": v(-93.45, 55.34) * mm, "mid": v(-94.22, 55.28) * mm, "end": v(-94.71, 54.7) * mm});
            skArc(sketch, "E70.4.9", {"start": v(-94.71, 54.7) * mm, "mid": v(-94.65, 53.94) * mm, "end": v(-94.07, 53.44) * mm});
            skLineSegment(sketch, "E70.5.0", {"start": v(-94.74, 49.21) * mm, "end": v(-89.74, 49.21) * mm});
            skLineSegment(sketch, "E70.5.1", {"start": v(-94.74, 47.21) * mm, "end": v(-89.74, 47.21) * mm});
            skPoint(sketch, "E70.5.2", {"position": v(-88.74, 47.21) * mm});
            skPoint(sketch, "E70.5.3", {"position": v(-88.74, 49.21) * mm});
            skArc(sketch, "E70.5.4", {"start": v(-89.74, 47.21) * mm, "mid": v(-89.03, 47.5) * mm, "end": v(-88.74, 48.21) * mm});
            skArc(sketch, "E70.5.5", {"start": v(-88.74, 48.21) * mm, "mid": v(-89.03, 48.92) * mm, "end": v(-89.74, 49.21) * mm});
            skPoint(sketch, "E70.5.6", {"position": v(-95.74, 47.21) * mm});
            skPoint(sketch, "E70.5.7", {"position": v(-95.74, 49.21) * mm});
            skArc(sketch, "E70.5.8", {"start": v(-94.74, 49.21) * mm, "mid": v(-95.45, 48.92) * mm, "end": v(-95.74, 48.21) * mm});
            skArc(sketch, "E70.5.9", {"start": v(-95.74, 48.21) * mm, "mid": v(-95.45, 47.5) * mm, "end": v(-94.74, 47.21) * mm});
            skLineSegment(sketch, "E70.6.0", {"start": v(-94.07, 42.98) * mm, "end": v(-89.31, 44.53) * mm});
            skLineSegment(sketch, "E70.6.1", {"start": v(-93.45, 41.08) * mm, "end": v(-88.7, 42.62) * mm});
            skPoint(sketch, "E70.6.2", {"position": v(-87.75, 42.93) * mm});
            skPoint(sketch, "E70.6.3", {"position": v(-88.36, 44.83) * mm});
            skArc(sketch, "E70.6.4", {"start": v(-88.7, 42.62) * mm, "mid": v(-88.11, 43.12) * mm, "end": v(-88.05, 43.88) * mm});
            skArc(sketch, "E70.6.5", {"start": v(-88.05, 43.88) * mm, "mid": v(-88.55, 44.47) * mm, "end": v(-89.31, 44.53) * mm});
            skPoint(sketch, "E70.6.6", {"position": v(-94.4, 40.77) * mm});
            skPoint(sketch, "E70.6.7", {"position": v(-95.02, 42.67) * mm});
            skArc(sketch, "E70.6.8", {"start": v(-94.07, 42.98) * mm, "mid": v(-94.65, 42.48) * mm, "end": v(-94.71, 41.72) * mm});
            skArc(sketch, "E70.6.9", {"start": v(-94.71, 41.72) * mm, "mid": v(-94.22, 41.14) * mm, "end": v(-93.45, 41.08) * mm});
            skLineSegment(sketch, "E70.7.0", {"start": v(-91.5, 37.26) * mm, "end": v(-87.46, 40.2) * mm});
            skLineSegment(sketch, "E70.7.1", {"start": v(-90.33, 35.65) * mm, "end": v(-86.29, 38.58) * mm});
            skPoint(sketch, "E70.7.2", {"position": v(-85.48, 39.17) * mm});
            skPoint(sketch, "E70.7.3", {"position": v(-86.65, 40.8) * mm});
            skArc(sketch, "E70.7.4", {"start": v(-86.29, 38.58) * mm, "mid": v(-85.89, 39.24) * mm, "end": v(-86.07, 39.98) * mm});
            skArc(sketch, "E70.7.5", {"start": v(-86.07, 39.98) * mm, "mid": v(-86.72, 40.38) * mm, "end": v(-87.46, 40.2) * mm});
            skPoint(sketch, "E70.7.6", {"position": v(-91.14, 35.06) * mm});
            skPoint(sketch, "E70.7.7", {"position": v(-92.32, 36.68) * mm});
            skArc(sketch, "E70.7.8", {"start": v(-91.5, 37.26) * mm, "mid": v(-91.9, 36.61) * mm, "end": v(-91.73, 35.87) * mm});
            skArc(sketch, "E70.7.9", {"start": v(-91.73, 35.87) * mm, "mid": v(-91.08, 35.47) * mm, "end": v(-90.33, 35.65) * mm});
            skLineSegment(sketch, "E70.8.0", {"start": v(-87.3, 32.62) * mm, "end": v(-84.37, 36.66) * mm});
            skLineSegment(sketch, "E70.8.1", {"start": v(-85.69, 31.44) * mm, "end": v(-82.75, 35.49) * mm});
            skPoint(sketch, "E70.8.2", {"position": v(-82.16, 36.3) * mm});
            skPoint(sketch, "E70.8.3", {"position": v(-83.78, 37.47) * mm});
            skArc(sketch, "E70.8.4", {"start": v(-82.75, 35.49) * mm, "mid": v(-82.57, 36.23) * mm, "end": v(-82.97, 36.88) * mm});
            skArc(sketch, "E70.8.5", {"start": v(-82.97, 36.88) * mm, "mid": v(-83.71, 37.06) * mm, "end": v(-84.37, 36.66) * mm});
            skPoint(sketch, "E70.8.6", {"position": v(-86.27, 30.63) * mm});
            skPoint(sketch, "E70.8.7", {"position": v(-87.9, 31.8) * mm});
            skArc(sketch, "E70.8.8", {"start": v(-87.3, 32.62) * mm, "mid": v(-87.48, 31.87) * mm, "end": v(-87.08, 31.22) * mm});
            skArc(sketch, "E70.8.9", {"start": v(-87.08, 31.22) * mm, "mid": v(-86.34, 31.04) * mm, "end": v(-85.69, 31.44) * mm});
            skLineSegment(sketch, "E70.9.0", {"start": v(-81.87, 29.5) * mm, "end": v(-80.33, 34.25) * mm});
            skLineSegment(sketch, "E70.9.1", {"start": v(-79.97, 28.88) * mm, "end": v(-78.42, 33.64) * mm});
            skPoint(sketch, "E70.9.2", {"position": v(-78.12, 34.59) * mm});
            skPoint(sketch, "E70.9.3", {"position": v(-80.02, 35.2) * mm});
            skArc(sketch, "E70.9.4", {"start": v(-78.42, 33.64) * mm, "mid": v(-78.48, 34.4) * mm, "end": v(-79.07, 34.9) * mm});
            skArc(sketch, "E70.9.5", {"start": v(-79.07, 34.9) * mm, "mid": v(-79.83, 34.84) * mm, "end": v(-80.33, 34.25) * mm});
            skPoint(sketch, "E70.9.6", {"position": v(-80.28, 27.93) * mm});
            skPoint(sketch, "E70.9.7", {"position": v(-82.18, 28.55) * mm});
            skArc(sketch, "E70.9.8", {"start": v(-81.87, 29.5) * mm, "mid": v(-81.81, 28.73) * mm, "end": v(-81.23, 28.24) * mm});
            skArc(sketch, "E70.9.9", {"start": v(-81.23, 28.24) * mm, "mid": v(-80.47, 28.3) * mm, "end": v(-79.97, 28.88) * mm});
            skLineSegment(sketch, "E70.10.0", {"start": v(-75.74, 28.21) * mm, "end": v(-75.74, 33.21) * mm});
            skLineSegment(sketch, "E70.10.1", {"start": v(-73.74, 28.21) * mm, "end": v(-73.74, 33.21) * mm});
            skPoint(sketch, "E70.10.2", {"position": v(-73.74, 34.21) * mm});
            skPoint(sketch, "E70.10.3", {"position": v(-75.74, 34.21) * mm});
            skArc(sketch, "E70.10.4", {"start": v(-73.74, 33.21) * mm, "mid": v(-74.03, 33.92) * mm, "end": v(-74.74, 34.21) * mm});
            skArc(sketch, "E70.10.5", {"start": v(-74.74, 34.21) * mm, "mid": v(-75.45, 33.92) * mm, "end": v(-75.74, 33.21) * mm});
            skPoint(sketch, "E70.10.6", {"position": v(-73.74, 27.21) * mm});
            skPoint(sketch, "E70.10.7", {"position": v(-75.74, 27.21) * mm});
            skArc(sketch, "E70.10.8", {"start": v(-75.74, 28.21) * mm, "mid": v(-75.45, 27.5) * mm, "end": v(-74.74, 27.21) * mm});
            skArc(sketch, "E70.10.9", {"start": v(-74.74, 27.21) * mm, "mid": v(-74.03, 27.5) * mm, "end": v(-73.74, 28.21) * mm});
            skLineSegment(sketch, "E70.11.0", {"start": v(-69.51, 28.88) * mm, "end": v(-71.06, 33.64) * mm});
            skLineSegment(sketch, "E70.11.1", {"start": v(-67.6, 29.5) * mm, "end": v(-69.15, 34.25) * mm});
            skPoint(sketch, "E70.11.2", {"position": v(-69.46, 35.2) * mm});
            skPoint(sketch, "E70.11.3", {"position": v(-71.36, 34.59) * mm});
            skArc(sketch, "E70.11.4", {"start": v(-69.15, 34.25) * mm, "mid": v(-69.65, 34.84) * mm, "end": v(-70.41, 34.9) * mm});
            skArc(sketch, "E70.11.5", {"start": v(-70.41, 34.9) * mm, "mid": v(-71, 34.4) * mm, "end": v(-71.06, 33.64) * mm});
            skPoint(sketch, "E70.11.6", {"position": v(-67.3, 28.55) * mm});
            skPoint(sketch, "E70.11.7", {"position": v(-69.2, 27.93) * mm});
            skArc(sketch, "E70.11.8", {"start": v(-69.51, 28.88) * mm, "mid": v(-69.01, 28.3) * mm, "end": v(-68.25, 28.24) * mm});
            skArc(sketch, "E70.11.9", {"start": v(-68.25, 28.24) * mm, "mid": v(-67.67, 28.73) * mm, "end": v(-67.6, 29.5) * mm});
            skLineSegment(sketch, "E70.12.0", {"start": v(-63.8, 31.44) * mm, "end": v(-66.73, 35.49) * mm});
            skLineSegment(sketch, "E70.12.1", {"start": v(-62.18, 32.62) * mm, "end": v(-65.11, 36.66) * mm});
            skPoint(sketch, "E70.12.2", {"position": v(-65.7, 37.47) * mm});
            skPoint(sketch, "E70.12.3", {"position": v(-67.32, 36.3) * mm});
            skArc(sketch, "E70.12.4", {"start": v(-65.11, 36.66) * mm, "mid": v(-65.77, 37.06) * mm, "end": v(-66.51, 36.88) * mm});
            skArc(sketch, "E70.12.5", {"start": v(-66.51, 36.88) * mm, "mid": v(-66.91, 36.23) * mm, "end": v(-66.73, 35.49) * mm});
            skPoint(sketch, "E70.12.6", {"position": v(-61.59, 31.8) * mm});
            skPoint(sketch, "E70.12.7", {"position": v(-63.2, 30.63) * mm});
            skArc(sketch, "E70.12.8", {"start": v(-63.8, 31.44) * mm, "mid": v(-63.14, 31.04) * mm, "end": v(-62.4, 31.22) * mm});
            skArc(sketch, "E70.12.9", {"start": v(-62.4, 31.22) * mm, "mid": v(-62, 31.87) * mm, "end": v(-62.18, 32.62) * mm});
            skLineSegment(sketch, "E70.13.0", {"start": v(-59.15, 35.65) * mm, "end": v(-63.2, 38.58) * mm});
            skLineSegment(sketch, "E70.13.1", {"start": v(-57.97, 37.26) * mm, "end": v(-62.02, 40.2) * mm});
            skPoint(sketch, "E70.13.2", {"position": v(-62.83, 40.8) * mm});
            skPoint(sketch, "E70.13.3", {"position": v(-64, 39.17) * mm});
            skArc(sketch, "E70.13.4", {"start": v(-62.02, 40.2) * mm, "mid": v(-62.76, 40.38) * mm, "end": v(-63.41, 39.98) * mm});
            skArc(sketch, "E70.13.5", {"start": v(-63.41, 39.98) * mm, "mid": v(-63.6, 39.24) * mm, "end": v(-63.2, 38.58) * mm});
            skPoint(sketch, "E70.13.6", {"position": v(-57.16, 36.68) * mm});
            skPoint(sketch, "E70.13.7", {"position": v(-58.34, 35.06) * mm});
            skArc(sketch, "E70.13.8", {"start": v(-59.15, 35.65) * mm, "mid": v(-58.4, 35.47) * mm, "end": v(-57.75, 35.87) * mm});
            skArc(sketch, "E70.13.9", {"start": v(-57.75, 35.87) * mm, "mid": v(-57.57, 36.61) * mm, "end": v(-57.97, 37.26) * mm});
            skLineSegment(sketch, "E70.14.0", {"start": v(-56.03, 41.08) * mm, "end": v(-60.78, 42.62) * mm});
            skLineSegment(sketch, "E70.14.1", {"start": v(-55.4, 42.98) * mm, "end": v(-60.17, 44.53) * mm});
            skPoint(sketch, "E70.14.2", {"position": v(-61.12, 44.83) * mm});
            skPoint(sketch, "E70.14.3", {"position": v(-61.73, 42.93) * mm});
            skArc(sketch, "E70.14.4", {"start": v(-60.17, 44.53) * mm, "mid": v(-60.93, 44.47) * mm, "end": v(-61.43, 43.88) * mm});
            skArc(sketch, "E70.14.5", {"start": v(-61.43, 43.88) * mm, "mid": v(-61.37, 43.12) * mm, "end": v(-60.78, 42.62) * mm});
            skPoint(sketch, "E70.14.6", {"position": v(-54.46, 42.67) * mm});
            skPoint(sketch, "E70.14.7", {"position": v(-55.08, 40.77) * mm});
            skArc(sketch, "E70.14.8", {"start": v(-56.03, 41.08) * mm, "mid": v(-55.26, 41.14) * mm, "end": v(-54.77, 41.72) * mm});
            skArc(sketch, "E70.14.9", {"start": v(-54.77, 41.72) * mm, "mid": v(-54.83, 42.48) * mm, "end": v(-55.4, 42.98) * mm});
            skLineSegment(sketch, "E70.15.0", {"start": v(-54.74, 47.21) * mm, "end": v(-59.74, 47.21) * mm});
            skLineSegment(sketch, "E70.15.1", {"start": v(-54.74, 49.21) * mm, "end": v(-59.74, 49.21) * mm});
            skPoint(sketch, "E70.15.2", {"position": v(-60.74, 49.21) * mm});
            skPoint(sketch, "E70.15.3", {"position": v(-60.74, 47.21) * mm});
            skArc(sketch, "E70.15.4", {"start": v(-59.74, 49.21) * mm, "mid": v(-60.45, 48.92) * mm, "end": v(-60.74, 48.21) * mm});
            skArc(sketch, "E70.15.5", {"start": v(-60.74, 48.21) * mm, "mid": v(-60.45, 47.5) * mm, "end": v(-59.74, 47.21) * mm});
            skPoint(sketch, "E70.15.6", {"position": v(-53.74, 49.21) * mm});
            skPoint(sketch, "E70.15.7", {"position": v(-53.74, 47.21) * mm});
            skArc(sketch, "E70.15.8", {"start": v(-54.74, 47.21) * mm, "mid": v(-54.03, 47.5) * mm, "end": v(-53.74, 48.21) * mm});
            skArc(sketch, "E70.15.9", {"start": v(-53.74, 48.21) * mm, "mid": v(-54.03, 48.92) * mm, "end": v(-54.74, 49.21) * mm});
            skLineSegment(sketch, "E70.16.0", {"start": v(-55.4, 53.44) * mm, "end": v(-60.17, 51.9) * mm});
            skLineSegment(sketch, "E70.16.1", {"start": v(-56.03, 55.34) * mm, "end": v(-60.78, 53.8) * mm});
            skPoint(sketch, "E70.16.2", {"position": v(-61.73, 53.49) * mm});
            skPoint(sketch, "E70.16.3", {"position": v(-61.12, 51.59) * mm});
            skArc(sketch, "E70.16.4", {"start": v(-60.78, 53.8) * mm, "mid": v(-61.37, 53.3) * mm, "end": v(-61.43, 52.54) * mm});
            skArc(sketch, "E70.16.5", {"start": v(-61.43, 52.54) * mm, "mid": v(-60.93, 51.95) * mm, "end": v(-60.17, 51.9) * mm});
            skPoint(sketch, "E70.16.6", {"position": v(-55.08, 55.65) * mm});
            skPoint(sketch, "E70.16.7", {"position": v(-54.46, 53.75) * mm});
            skArc(sketch, "E70.16.8", {"start": v(-55.4, 53.44) * mm, "mid": v(-54.83, 53.94) * mm, "end": v(-54.77, 54.7) * mm});
            skArc(sketch, "E70.16.9", {"start": v(-54.77, 54.7) * mm, "mid": v(-55.26, 55.28) * mm, "end": v(-56.03, 55.34) * mm});
            skLineSegment(sketch, "E70.17.0", {"start": v(-57.97, 59.16) * mm, "end": v(-62.02, 56.22) * mm});
            skLineSegment(sketch, "E70.17.1", {"start": v(-59.15, 60.77) * mm, "end": v(-63.2, 57.84) * mm});
            skPoint(sketch, "E70.17.2", {"position": v(-64, 57.25) * mm});
            skPoint(sketch, "E70.17.3", {"position": v(-62.83, 55.63) * mm});
            skArc(sketch, "E70.17.4", {"start": v(-63.2, 57.84) * mm, "mid": v(-63.6, 57.18) * mm, "end": v(-63.41, 56.44) * mm});
            skArc(sketch, "E70.17.5", {"start": v(-63.41, 56.44) * mm, "mid": v(-62.76, 56.04) * mm, "end": v(-62.02, 56.22) * mm});
            skPoint(sketch, "E70.17.6", {"position": v(-58.34, 61.36) * mm});
            skPoint(sketch, "E70.17.7", {"position": v(-57.16, 59.74) * mm});
            skArc(sketch, "E70.17.8", {"start": v(-57.97, 59.16) * mm, "mid": v(-57.57, 59.8) * mm, "end": v(-57.75, 60.55) * mm});
            skArc(sketch, "E70.17.9", {"start": v(-57.75, 60.55) * mm, "mid": v(-58.4, 60.95) * mm, "end": v(-59.15, 60.77) * mm});
            skLineSegment(sketch, "E70.18.0", {"start": v(-62.18, 63.8) * mm, "end": v(-65.11, 59.76) * mm});
            skLineSegment(sketch, "E70.18.1", {"start": v(-63.8, 64.98) * mm, "end": v(-66.73, 60.93) * mm});
            skPoint(sketch, "E70.18.2", {"position": v(-67.32, 60.12) * mm});
            skPoint(sketch, "E70.18.3", {"position": v(-65.7, 58.95) * mm});
            skArc(sketch, "E70.18.4", {"start": v(-66.73, 60.93) * mm, "mid": v(-66.91, 60.19) * mm, "end": v(-66.51, 59.54) * mm});
            skArc(sketch, "E70.18.5", {"start": v(-66.51, 59.54) * mm, "mid": v(-65.77, 59.36) * mm, "end": v(-65.11, 59.76) * mm});
            skPoint(sketch, "E70.18.6", {"position": v(-63.2, 65.79) * mm});
            skPoint(sketch, "E70.18.7", {"position": v(-61.59, 64.61) * mm});
            skArc(sketch, "E70.18.8", {"start": v(-62.18, 63.8) * mm, "mid": v(-62, 64.55) * mm, "end": v(-62.4, 65.2) * mm});
            skArc(sketch, "E70.18.9", {"start": v(-62.4, 65.2) * mm, "mid": v(-63.14, 65.38) * mm, "end": v(-63.8, 64.98) * mm});
            skLineSegment(sketch, "E70.19.0", {"start": v(-67.6, 66.92) * mm, "end": v(-69.15, 62.17) * mm});
            skLineSegment(sketch, "E70.19.1", {"start": v(-69.51, 67.54) * mm, "end": v(-71.06, 62.78) * mm});
            skPoint(sketch, "E70.19.2", {"position": v(-71.36, 61.83) * mm});
            skPoint(sketch, "E70.19.3", {"position": v(-69.46, 61.22) * mm});
            skArc(sketch, "E70.19.4", {"start": v(-71.06, 62.78) * mm, "mid": v(-71, 62.02) * mm, "end": v(-70.41, 61.52) * mm});
            skArc(sketch, "E70.19.5", {"start": v(-70.41, 61.52) * mm, "mid": v(-69.65, 61.58) * mm, "end": v(-69.15, 62.17) * mm});
            skPoint(sketch, "E70.19.6", {"position": v(-69.2, 68.5) * mm});
            skPoint(sketch, "E70.19.7", {"position": v(-67.3, 67.87) * mm});
            skArc(sketch, "E70.19.8", {"start": v(-67.6, 66.92) * mm, "mid": v(-67.67, 67.69) * mm, "end": v(-68.25, 68.18) * mm});
            skArc(sketch, "E70.19.9", {"start": v(-68.25, 68.18) * mm, "mid": v(-69.01, 68.12) * mm, "end": v(-69.51, 67.54) * mm});
            skArc(sketch, "E71.1.0", {"start": v(-30.8, 80.57) * mm, "mid": v(-30.22, 81.07) * mm, "end": v(-30.16, 81.83) * mm});
            skLineSegment(sketch, "E71.1.1", {"start": v(-33.61, 85.97) * mm, "end": v(-32.07, 81.22) * mm});
            skPoint(sketch, "E71.1.2", {"position": v(-29.86, 80.88) * mm});
            skLineSegment(sketch, "E71.1.3", {"start": v(-31.7, 86.6) * mm, "end": v(-30.16, 81.83) * mm});
            skPoint(sketch, "E71.1.4", {"position": v(-31.76, 80.27) * mm});
            skArc(sketch, "E71.1.5", {"start": v(-32.07, 81.22) * mm, "mid": v(-31.57, 80.63) * mm, "end": v(-30.8, 80.57) * mm});
            skPoint(sketch, "E71.1.6", {"position": v(-33.92, 86.92) * mm});
            skPoint(sketch, "E71.1.7", {"position": v(-32.02, 87.54) * mm});
            skArc(sketch, "E71.1.8", {"start": v(-31.7, 86.6) * mm, "mid": v(-32.2, 87.17) * mm, "end": v(-32.97, 87.23) * mm});
            skArc(sketch, "E71.1.9", {"start": v(-32.97, 87.23) * mm, "mid": v(-33.55, 86.74) * mm, "end": v(-33.61, 85.97) * mm});
            skArc(sketch, "E71.2.0", {"start": v(-34.7, 78.59) * mm, "mid": v(-34.3, 79.24) * mm, "end": v(-34.49, 79.98) * mm});
            skLineSegment(sketch, "E71.2.1", {"start": v(-39.04, 82.85) * mm, "end": v(-36.1, 78.8) * mm});
            skPoint(sketch, "E71.2.2", {"position": v(-33.9, 79.17) * mm});
            skLineSegment(sketch, "E71.2.3", {"start": v(-37.43, 84.03) * mm, "end": v(-34.49, 79.98) * mm});
            skPoint(sketch, "E71.2.4", {"position": v(-35.52, 78) * mm});
            skArc(sketch, "E71.2.5", {"start": v(-36.1, 78.8) * mm, "mid": v(-35.45, 78.4) * mm, "end": v(-34.7, 78.59) * mm});
            skPoint(sketch, "E71.2.6", {"position": v(-39.63, 83.66) * mm});
            skPoint(sketch, "E71.2.7", {"position": v(-38.01, 84.84) * mm});
            skArc(sketch, "E71.2.8", {"start": v(-37.43, 84.03) * mm, "mid": v(-38.08, 84.43) * mm, "end": v(-38.82, 84.25) * mm});
            skArc(sketch, "E71.2.9", {"start": v(-38.82, 84.25) * mm, "mid": v(-39.22, 83.6) * mm, "end": v(-39.04, 82.85) * mm});
            skArc(sketch, "E71.3.0", {"start": v(-37.8, 75.49) * mm, "mid": v(-37.63, 76.23) * mm, "end": v(-38.03, 76.89) * mm});
            skLineSegment(sketch, "E71.3.1", {"start": v(-43.25, 78.2) * mm, "end": v(-39.2, 75.27) * mm});
            skPoint(sketch, "E71.3.2", {"position": v(-37.22, 76.3) * mm});
            skLineSegment(sketch, "E71.3.3", {"start": v(-42.07, 79.82) * mm, "end": v(-38.03, 76.89) * mm});
            skPoint(sketch, "E71.3.4", {"position": v(-38.4, 74.68) * mm});
            skArc(sketch, "E71.3.5", {"start": v(-39.2, 75.27) * mm, "mid": v(-38.46, 75.09) * mm, "end": v(-37.8, 75.49) * mm});
            skPoint(sketch, "E71.3.6", {"position": v(-44.06, 78.8) * mm});
            skPoint(sketch, "E71.3.7", {"position": v(-42.88, 80.41) * mm});
            skArc(sketch, "E71.3.8", {"start": v(-42.07, 79.82) * mm, "mid": v(-42.82, 80) * mm, "end": v(-43.47, 79.6) * mm});
            skArc(sketch, "E71.3.9", {"start": v(-43.47, 79.6) * mm, "mid": v(-43.65, 78.86) * mm, "end": v(-43.25, 78.2) * mm});
            skArc(sketch, "E71.4.0", {"start": v(-39.8, 71.59) * mm, "mid": v(-39.85, 72.35) * mm, "end": v(-40.44, 72.85) * mm});
            skLineSegment(sketch, "E71.4.1", {"start": v(-45.81, 72.49) * mm, "end": v(-41.05, 70.94) * mm});
            skPoint(sketch, "E71.4.2", {"position": v(-39.49, 72.54) * mm});
            skLineSegment(sketch, "E71.4.3", {"start": v(-45.2, 74.4) * mm, "end": v(-40.44, 72.85) * mm});
            skPoint(sketch, "E71.4.4", {"position": v(-40.1, 70.64) * mm});
            skArc(sketch, "E71.4.5", {"start": v(-41.05, 70.94) * mm, "mid": v(-40.3, 71) * mm, "end": v(-39.8, 71.59) * mm});
            skPoint(sketch, "E71.4.6", {"position": v(-46.76, 72.8) * mm});
            skPoint(sketch, "E71.4.7", {"position": v(-46.14, 74.7) * mm});
            skArc(sketch, "E71.4.8", {"start": v(-45.2, 74.4) * mm, "mid": v(-45.96, 74.33) * mm, "end": v(-46.45, 73.75) * mm});
            skArc(sketch, "E71.4.9", {"start": v(-46.45, 73.75) * mm, "mid": v(-46.4, 72.99) * mm, "end": v(-45.81, 72.49) * mm});
            skArc(sketch, "E71.5.0", {"start": v(-40.48, 67.26) * mm, "mid": v(-40.77, 67.97) * mm, "end": v(-41.48, 68.26) * mm});
            skLineSegment(sketch, "E71.5.1", {"start": v(-46.48, 66.26) * mm, "end": v(-41.48, 66.26) * mm});
            skPoint(sketch, "E71.5.2", {"position": v(-40.48, 68.26) * mm});
            skLineSegment(sketch, "E71.5.3", {"start": v(-46.48, 68.26) * mm, "end": v(-41.48, 68.26) * mm});
            skPoint(sketch, "E71.5.4", {"position": v(-40.48, 66.26) * mm});
            skArc(sketch, "E71.5.5", {"start": v(-41.48, 66.26) * mm, "mid": v(-40.77, 66.55) * mm, "end": v(-40.48, 67.26) * mm});
            skPoint(sketch, "E71.5.6", {"position": v(-47.48, 66.26) * mm});
            skPoint(sketch, "E71.5.7", {"position": v(-47.48, 68.26) * mm});
            skArc(sketch, "E71.5.8", {"start": v(-46.48, 68.26) * mm, "mid": v(-47.19, 67.97) * mm, "end": v(-47.48, 67.26) * mm});
            skArc(sketch, "E71.5.9", {"start": v(-47.48, 67.26) * mm, "mid": v(-47.19, 66.55) * mm, "end": v(-46.48, 66.26) * mm});
            skArc(sketch, "E71.6.0", {"start": v(-39.8, 62.93) * mm, "mid": v(-40.3, 63.52) * mm, "end": v(-41.05, 63.58) * mm});
            skLineSegment(sketch, "E71.6.1", {"start": v(-45.2, 60.13) * mm, "end": v(-40.44, 61.67) * mm});
            skPoint(sketch, "E71.6.2", {"position": v(-40.1, 63.88) * mm});
            skLineSegment(sketch, "E71.6.3", {"start": v(-45.81, 62.03) * mm, "end": v(-41.05, 63.58) * mm});
            skPoint(sketch, "E71.6.4", {"position": v(-39.49, 61.98) * mm});
            skArc(sketch, "E71.6.5", {"start": v(-40.44, 61.67) * mm, "mid": v(-39.85, 62.17) * mm, "end": v(-39.8, 62.93) * mm});
            skPoint(sketch, "E71.6.6", {"position": v(-46.14, 59.82) * mm});
            skPoint(sketch, "E71.6.7", {"position": v(-46.76, 61.72) * mm});
            skArc(sketch, "E71.6.8", {"start": v(-45.81, 62.03) * mm, "mid": v(-46.4, 61.53) * mm, "end": v(-46.45, 60.77) * mm});
            skArc(sketch, "E71.6.9", {"start": v(-46.45, 60.77) * mm, "mid": v(-45.96, 60.19) * mm, "end": v(-45.2, 60.13) * mm});
            skArc(sketch, "E71.7.0", {"start": v(-37.8, 59.03) * mm, "mid": v(-38.46, 59.43) * mm, "end": v(-39.2, 59.25) * mm});
            skLineSegment(sketch, "E71.7.1", {"start": v(-42.07, 54.7) * mm, "end": v(-38.03, 57.63) * mm});
            skPoint(sketch, "E71.7.2", {"position": v(-38.4, 59.84) * mm});
            skLineSegment(sketch, "E71.7.3", {"start": v(-43.25, 56.31) * mm, "end": v(-39.2, 59.25) * mm});
            skPoint(sketch, "E71.7.4", {"position": v(-37.22, 58.22) * mm});
            skArc(sketch, "E71.7.5", {"start": v(-38.03, 57.63) * mm, "mid": v(-37.63, 58.29) * mm, "end": v(-37.8, 59.03) * mm});
            skPoint(sketch, "E71.7.6", {"position": v(-42.88, 54.1) * mm});
            skPoint(sketch, "E71.7.7", {"position": v(-44.06, 55.73) * mm});
            skArc(sketch, "E71.7.8", {"start": v(-43.25, 56.31) * mm, "mid": v(-43.65, 55.66) * mm, "end": v(-43.47, 54.92) * mm});
            skArc(sketch, "E71.7.9", {"start": v(-43.47, 54.92) * mm, "mid": v(-42.82, 54.52) * mm, "end": v(-42.07, 54.7) * mm});
            skArc(sketch, "E71.8.0", {"start": v(-34.7, 55.93) * mm, "mid": v(-35.45, 56.11) * mm, "end": v(-36.1, 55.71) * mm});
            skLineSegment(sketch, "E71.8.1", {"start": v(-37.43, 50.5) * mm, "end": v(-34.49, 54.54) * mm});
            skPoint(sketch, "E71.8.2", {"position": v(-35.52, 56.52) * mm});
            skLineSegment(sketch, "E71.8.3", {"start": v(-39.04, 51.67) * mm, "end": v(-36.1, 55.71) * mm});
            skPoint(sketch, "E71.8.4", {"position": v(-33.9, 55.35) * mm});
            skArc(sketch, "E71.8.5", {"start": v(-34.49, 54.54) * mm, "mid": v(-34.3, 55.28) * mm, "end": v(-34.7, 55.93) * mm});
            skPoint(sketch, "E71.8.6", {"position": v(-38.01, 49.68) * mm});
            skPoint(sketch, "E71.8.7", {"position": v(-39.63, 50.86) * mm});
            skArc(sketch, "E71.8.8", {"start": v(-39.04, 51.67) * mm, "mid": v(-39.22, 50.92) * mm, "end": v(-38.82, 50.27) * mm});
            skArc(sketch, "E71.8.9", {"start": v(-38.82, 50.27) * mm, "mid": v(-38.08, 50.1) * mm, "end": v(-37.43, 50.5) * mm});
            skArc(sketch, "E71.9.0", {"start": v(-30.8, 53.95) * mm, "mid": v(-31.57, 53.89) * mm, "end": v(-32.07, 53.3) * mm});
            skLineSegment(sketch, "E71.9.1", {"start": v(-31.7, 47.93) * mm, "end": v(-30.16, 52.69) * mm});
            skPoint(sketch, "E71.9.2", {"position": v(-31.76, 54.25) * mm});
            skLineSegment(sketch, "E71.9.3", {"start": v(-33.61, 48.55) * mm, "end": v(-32.07, 53.3) * mm});
            skPoint(sketch, "E71.9.4", {"position": v(-29.86, 53.64) * mm});
            skArc(sketch, "E71.9.5", {"start": v(-30.16, 52.69) * mm, "mid": v(-30.22, 53.45) * mm, "end": v(-30.8, 53.95) * mm});
            skPoint(sketch, "E71.9.6", {"position": v(-32.02, 46.98) * mm});
            skPoint(sketch, "E71.9.7", {"position": v(-33.92, 47.6) * mm});
            skArc(sketch, "E71.9.8", {"start": v(-33.61, 48.55) * mm, "mid": v(-33.55, 47.78) * mm, "end": v(-32.97, 47.29) * mm});
            skArc(sketch, "E71.9.9", {"start": v(-32.97, 47.29) * mm, "mid": v(-32.2, 47.35) * mm, "end": v(-31.7, 47.93) * mm});
            skArc(sketch, "E71.10.0", {"start": v(-26.48, 53.26) * mm, "mid": v(-27.19, 52.97) * mm, "end": v(-27.48, 52.26) * mm});
            skLineSegment(sketch, "E71.10.1", {"start": v(-25.48, 47.26) * mm, "end": v(-25.48, 52.26) * mm});
            skPoint(sketch, "E71.10.2", {"position": v(-27.48, 53.26) * mm});
            skLineSegment(sketch, "E71.10.3", {"start": v(-27.48, 47.26) * mm, "end": v(-27.48, 52.26) * mm});
            skPoint(sketch, "E71.10.4", {"position": v(-25.48, 53.26) * mm});
            skArc(sketch, "E71.10.5", {"start": v(-25.48, 52.26) * mm, "mid": v(-25.77, 52.97) * mm, "end": v(-26.48, 53.26) * mm});
            skPoint(sketch, "E71.10.6", {"position": v(-25.48, 46.26) * mm});
            skPoint(sketch, "E71.10.7", {"position": v(-27.48, 46.26) * mm});
            skArc(sketch, "E71.10.8", {"start": v(-27.48, 47.26) * mm, "mid": v(-27.19, 46.55) * mm, "end": v(-26.48, 46.26) * mm});
            skArc(sketch, "E71.10.9", {"start": v(-26.48, 46.26) * mm, "mid": v(-25.77, 46.55) * mm, "end": v(-25.48, 47.26) * mm});
            skArc(sketch, "E71.11.0", {"start": v(-22.15, 53.95) * mm, "mid": v(-22.74, 53.45) * mm, "end": v(-22.8, 52.69) * mm});
            skLineSegment(sketch, "E71.11.1", {"start": v(-19.35, 48.55) * mm, "end": v(-20.9, 53.3) * mm});
            skPoint(sketch, "E71.11.2", {"position": v(-23.1, 53.64) * mm});
            skLineSegment(sketch, "E71.11.3", {"start": v(-21.25, 47.93) * mm, "end": v(-22.8, 52.69) * mm});
            skPoint(sketch, "E71.11.4", {"position": v(-21.2, 54.25) * mm});
            skArc(sketch, "E71.11.5", {"start": v(-20.9, 53.3) * mm, "mid": v(-21.4, 53.89) * mm, "end": v(-22.15, 53.95) * mm});
            skPoint(sketch, "E71.11.6", {"position": v(-19.04, 47.6) * mm});
            skPoint(sketch, "E71.11.7", {"position": v(-20.94, 46.98) * mm});
            skArc(sketch, "E71.11.8", {"start": v(-21.25, 47.93) * mm, "mid": v(-20.75, 47.35) * mm, "end": v(-20, 47.29) * mm});
            skArc(sketch, "E71.11.9", {"start": v(-20, 47.29) * mm, "mid": v(-19.4, 47.78) * mm, "end": v(-19.35, 48.55) * mm});
            skArc(sketch, "E71.12.0", {"start": v(-18.25, 55.93) * mm, "mid": v(-18.65, 55.28) * mm, "end": v(-18.47, 54.54) * mm});
            skLineSegment(sketch, "E71.12.1", {"start": v(-13.92, 51.67) * mm, "end": v(-16.85, 55.71) * mm});
            skPoint(sketch, "E71.12.2", {"position": v(-19.06, 55.35) * mm});
            skLineSegment(sketch, "E71.12.3", {"start": v(-15.53, 50.5) * mm, "end": v(-18.47, 54.54) * mm});
            skPoint(sketch, "E71.12.4", {"position": v(-17.44, 56.52) * mm});
            skArc(sketch, "E71.12.5", {"start": v(-16.85, 55.71) * mm, "mid": v(-17.5, 56.11) * mm, "end": v(-18.25, 55.93) * mm});
            skPoint(sketch, "E71.12.6", {"position": v(-13.33, 50.86) * mm});
            skPoint(sketch, "E71.12.7", {"position": v(-14.95, 49.68) * mm});
            skArc(sketch, "E71.12.8", {"start": v(-15.53, 50.5) * mm, "mid": v(-14.88, 50.1) * mm, "end": v(-14.14, 50.27) * mm});
            skArc(sketch, "E71.12.9", {"start": v(-14.14, 50.27) * mm, "mid": v(-13.74, 50.92) * mm, "end": v(-13.92, 51.67) * mm});
            skArc(sketch, "E71.13.0", {"start": v(-15.15, 59.03) * mm, "mid": v(-15.33, 58.29) * mm, "end": v(-14.93, 57.63) * mm});
            skLineSegment(sketch, "E71.13.1", {"start": v(-9.71, 56.31) * mm, "end": v(-13.76, 59.25) * mm});
            skPoint(sketch, "E71.13.2", {"position": v(-15.74, 58.22) * mm});
            skLineSegment(sketch, "E71.13.3", {"start": v(-10.89, 54.7) * mm, "end": v(-14.93, 57.63) * mm});
            skPoint(sketch, "E71.13.4", {"position": v(-14.57, 59.84) * mm});
            skArc(sketch, "E71.13.5", {"start": v(-13.76, 59.25) * mm, "mid": v(-14.5, 59.43) * mm, "end": v(-15.15, 59.03) * mm});
            skPoint(sketch, "E71.13.6", {"position": v(-8.9, 55.73) * mm});
            skPoint(sketch, "E71.13.7", {"position": v(-10.08, 54.1) * mm});
            skArc(sketch, "E71.13.8", {"start": v(-10.89, 54.7) * mm, "mid": v(-10.14, 54.52) * mm, "end": v(-9.5, 54.92) * mm});
            skArc(sketch, "E71.13.9", {"start": v(-9.5, 54.92) * mm, "mid": v(-9.31, 55.66) * mm, "end": v(-9.71, 56.31) * mm});
            skArc(sketch, "E71.14.0", {"start": v(-13.17, 62.93) * mm, "mid": v(-13.1, 62.17) * mm, "end": v(-12.52, 61.67) * mm});
            skLineSegment(sketch, "E71.14.1", {"start": v(-7.15, 62.03) * mm, "end": v(-11.9, 63.58) * mm});
            skPoint(sketch, "E71.14.2", {"position": v(-13.47, 61.98) * mm});
            skLineSegment(sketch, "E71.14.3", {"start": v(-7.77, 60.13) * mm, "end": v(-12.52, 61.67) * mm});
            skPoint(sketch, "E71.14.4", {"position": v(-12.86, 63.88) * mm});
            skArc(sketch, "E71.14.5", {"start": v(-11.9, 63.58) * mm, "mid": v(-12.67, 63.52) * mm, "end": v(-13.17, 62.93) * mm});
            skPoint(sketch, "E71.14.6", {"position": v(-6.2, 61.72) * mm});
            skPoint(sketch, "E71.14.7", {"position": v(-6.82, 59.82) * mm});
            skArc(sketch, "E71.14.8", {"start": v(-7.77, 60.13) * mm, "mid": v(-7, 60.19) * mm, "end": v(-6.5, 60.77) * mm});
            skArc(sketch, "E71.14.9", {"start": v(-6.5, 60.77) * mm, "mid": v(-6.57, 61.53) * mm, "end": v(-7.15, 62.03) * mm});
            skArc(sketch, "E71.15.0", {"start": v(-12.48, 67.26) * mm, "mid": v(-12.19, 66.55) * mm, "end": v(-11.48, 66.26) * mm});
            skLineSegment(sketch, "E71.15.1", {"start": v(-6.48, 68.26) * mm, "end": v(-11.48, 68.26) * mm});
            skPoint(sketch, "E71.15.2", {"position": v(-12.48, 66.26) * mm});
            skLineSegment(sketch, "E71.15.3", {"start": v(-6.48, 66.26) * mm, "end": v(-11.48, 66.26) * mm});
            skPoint(sketch, "E71.15.4", {"position": v(-12.48, 68.26) * mm});
            skArc(sketch, "E71.15.5", {"start": v(-11.48, 68.26) * mm, "mid": v(-12.19, 67.97) * mm, "end": v(-12.48, 67.26) * mm});
            skPoint(sketch, "E71.15.6", {"position": v(-5.48, 68.26) * mm});
            skPoint(sketch, "E71.15.7", {"position": v(-5.48, 66.26) * mm});
            skArc(sketch, "E71.15.8", {"start": v(-6.48, 66.26) * mm, "mid": v(-5.77, 66.55) * mm, "end": v(-5.48, 67.26) * mm});
            skArc(sketch, "E71.15.9", {"start": v(-5.48, 67.26) * mm, "mid": v(-5.77, 67.97) * mm, "end": v(-6.48, 68.26) * mm});
            skArc(sketch, "E71.16.0", {"start": v(-13.17, 71.59) * mm, "mid": v(-12.67, 71) * mm, "end": v(-11.9, 70.94) * mm});
            skLineSegment(sketch, "E71.16.1", {"start": v(-7.77, 74.4) * mm, "end": v(-12.52, 72.85) * mm});
            skPoint(sketch, "E71.16.2", {"position": v(-12.86, 70.64) * mm});
            skLineSegment(sketch, "E71.16.3", {"start": v(-7.15, 72.49) * mm, "end": v(-11.9, 70.94) * mm});
            skPoint(sketch, "E71.16.4", {"position": v(-13.47, 72.54) * mm});
            skArc(sketch, "E71.16.5", {"start": v(-12.52, 72.85) * mm, "mid": v(-13.1, 72.35) * mm, "end": v(-13.17, 71.59) * mm});
            skPoint(sketch, "E71.16.6", {"position": v(-6.82, 74.7) * mm});
            skPoint(sketch, "E71.16.7", {"position": v(-6.2, 72.8) * mm});
            skArc(sketch, "E71.16.8", {"start": v(-7.15, 72.49) * mm, "mid": v(-6.57, 72.99) * mm, "end": v(-6.5, 73.75) * mm});
            skArc(sketch, "E71.16.9", {"start": v(-6.5, 73.75) * mm, "mid": v(-7, 74.33) * mm, "end": v(-7.77, 74.4) * mm});
            skArc(sketch, "E71.17.0", {"start": v(-15.15, 75.49) * mm, "mid": v(-14.5, 75.09) * mm, "end": v(-13.76, 75.27) * mm});
            skLineSegment(sketch, "E71.17.1", {"start": v(-10.89, 79.82) * mm, "end": v(-14.93, 76.89) * mm});
            skPoint(sketch, "E71.17.2", {"position": v(-14.57, 74.68) * mm});
            skLineSegment(sketch, "E71.17.3", {"start": v(-9.71, 78.2) * mm, "end": v(-13.76, 75.27) * mm});
            skPoint(sketch, "E71.17.4", {"position": v(-15.74, 76.3) * mm});
            skArc(sketch, "E71.17.5", {"start": v(-14.93, 76.89) * mm, "mid": v(-15.33, 76.23) * mm, "end": v(-15.15, 75.49) * mm});
            skPoint(sketch, "E71.17.6", {"position": v(-10.08, 80.41) * mm});
            skPoint(sketch, "E71.17.7", {"position": v(-8.9, 78.8) * mm});
            skArc(sketch, "E71.17.8", {"start": v(-9.71, 78.2) * mm, "mid": v(-9.31, 78.86) * mm, "end": v(-9.5, 79.6) * mm});
            skArc(sketch, "E71.17.9", {"start": v(-9.5, 79.6) * mm, "mid": v(-10.14, 80) * mm, "end": v(-10.89, 79.82) * mm});
            skArc(sketch, "E71.18.0", {"start": v(-18.25, 78.59) * mm, "mid": v(-17.5, 78.4) * mm, "end": v(-16.85, 78.8) * mm});
            skLineSegment(sketch, "E71.18.1", {"start": v(-15.53, 84.03) * mm, "end": v(-18.47, 79.98) * mm});
            skPoint(sketch, "E71.18.2", {"position": v(-17.44, 78) * mm});
            skLineSegment(sketch, "E71.18.3", {"start": v(-13.92, 82.85) * mm, "end": v(-16.85, 78.8) * mm});
            skPoint(sketch, "E71.18.4", {"position": v(-19.06, 79.17) * mm});
            skArc(sketch, "E71.18.5", {"start": v(-18.47, 79.98) * mm, "mid": v(-18.65, 79.24) * mm, "end": v(-18.25, 78.59) * mm});
            skPoint(sketch, "E71.18.6", {"position": v(-14.95, 84.84) * mm});
            skPoint(sketch, "E71.18.7", {"position": v(-13.33, 83.66) * mm});
            skArc(sketch, "E71.18.8", {"start": v(-13.92, 82.85) * mm, "mid": v(-13.74, 83.6) * mm, "end": v(-14.14, 84.25) * mm});
            skArc(sketch, "E71.18.9", {"start": v(-14.14, 84.25) * mm, "mid": v(-14.88, 84.43) * mm, "end": v(-15.53, 84.03) * mm});
            skArc(sketch, "E71.19.0", {"start": v(-22.15, 80.57) * mm, "mid": v(-21.4, 80.63) * mm, "end": v(-20.9, 81.22) * mm});
            skLineSegment(sketch, "E71.19.1", {"start": v(-21.25, 86.6) * mm, "end": v(-22.8, 81.83) * mm});
            skPoint(sketch, "E71.19.2", {"position": v(-21.2, 80.27) * mm});
            skLineSegment(sketch, "E71.19.3", {"start": v(-19.35, 85.97) * mm, "end": v(-20.9, 81.22) * mm});
            skPoint(sketch, "E71.19.4", {"position": v(-23.1, 80.88) * mm});
            skArc(sketch, "E71.19.5", {"start": v(-22.8, 81.83) * mm, "mid": v(-22.74, 81.07) * mm, "end": v(-22.15, 80.57) * mm});
            skPoint(sketch, "E71.19.6", {"position": v(-20.94, 87.54) * mm});
            skPoint(sketch, "E71.19.7", {"position": v(-19.04, 86.92) * mm});
            skArc(sketch, "E71.19.8", {"start": v(-19.35, 85.97) * mm, "mid": v(-19.4, 86.74) * mm, "end": v(-20, 87.23) * mm});
            skArc(sketch, "E71.19.9", {"start": v(-20, 87.23) * mm, "mid": v(-20.75, 87.17) * mm, "end": v(-21.25, 86.6) * mm});
            skPoint(sketch, "E72.1.0", {"position": v(-31.76, -54.25) * mm});
            skPoint(sketch, "E72.1.1", {"position": v(-32.02, -46.98) * mm});
            skPoint(sketch, "E72.1.2", {"position": v(-29.86, -53.64) * mm});
            skPoint(sketch, "E72.1.3", {"position": v(-33.92, -47.6) * mm});
            skLineSegment(sketch, "E72.1.4", {"start": v(-31.7, -47.93) * mm, "end": v(-30.16, -52.69) * mm});
            skLineSegment(sketch, "E72.1.5", {"start": v(-33.61, -48.55) * mm, "end": v(-32.07, -53.3) * mm});
            skArc(sketch, "E72.1.6", {"start": v(-32.07, -53.3) * mm, "mid": v(-31.57, -53.89) * mm, "end": v(-30.8, -53.95) * mm});
            skArc(sketch, "E72.1.7", {"start": v(-30.8, -53.95) * mm, "mid": v(-30.22, -53.45) * mm, "end": v(-30.16, -52.69) * mm});
            skArc(sketch, "E72.1.8", {"start": v(-31.7, -47.93) * mm, "mid": v(-32.2, -47.35) * mm, "end": v(-32.97, -47.29) * mm});
            skArc(sketch, "E72.1.9", {"start": v(-32.97, -47.29) * mm, "mid": v(-33.55, -47.78) * mm, "end": v(-33.61, -48.55) * mm});
            skPoint(sketch, "E72.2.0", {"position": v(-35.52, -56.52) * mm});
            skPoint(sketch, "E72.2.1", {"position": v(-38.01, -49.68) * mm});
            skPoint(sketch, "E72.2.2", {"position": v(-33.9, -55.35) * mm});
            skPoint(sketch, "E72.2.3", {"position": v(-39.63, -50.86) * mm});
            skLineSegment(sketch, "E72.2.4", {"start": v(-37.43, -50.5) * mm, "end": v(-34.49, -54.54) * mm});
            skLineSegment(sketch, "E72.2.5", {"start": v(-39.04, -51.67) * mm, "end": v(-36.1, -55.71) * mm});
            skArc(sketch, "E72.2.6", {"start": v(-36.1, -55.71) * mm, "mid": v(-35.45, -56.11) * mm, "end": v(-34.7, -55.93) * mm});
            skArc(sketch, "E72.2.7", {"start": v(-34.7, -55.93) * mm, "mid": v(-34.3, -55.28) * mm, "end": v(-34.49, -54.54) * mm});
            skArc(sketch, "E72.2.8", {"start": v(-37.43, -50.5) * mm, "mid": v(-38.08, -50.1) * mm, "end": v(-38.82, -50.27) * mm});
            skArc(sketch, "E72.2.9", {"start": v(-38.82, -50.27) * mm, "mid": v(-39.22, -50.92) * mm, "end": v(-39.04, -51.67) * mm});
            skPoint(sketch, "E72.3.0", {"position": v(-38.4, -59.84) * mm});
            skPoint(sketch, "E72.3.1", {"position": v(-42.88, -54.1) * mm});
            skPoint(sketch, "E72.3.2", {"position": v(-37.22, -58.22) * mm});
            skPoint(sketch, "E72.3.3", {"position": v(-44.06, -55.73) * mm});
            skLineSegment(sketch, "E72.3.4", {"start": v(-42.07, -54.7) * mm, "end": v(-38.03, -57.63) * mm});
            skLineSegment(sketch, "E72.3.5", {"start": v(-43.25, -56.31) * mm, "end": v(-39.2, -59.25) * mm});
            skArc(sketch, "E72.3.6", {"start": v(-39.2, -59.25) * mm, "mid": v(-38.46, -59.43) * mm, "end": v(-37.8, -59.03) * mm});
            skArc(sketch, "E72.3.7", {"start": v(-37.8, -59.03) * mm, "mid": v(-37.63, -58.29) * mm, "end": v(-38.03, -57.63) * mm});
            skArc(sketch, "E72.3.8", {"start": v(-42.07, -54.7) * mm, "mid": v(-42.82, -54.52) * mm, "end": v(-43.47, -54.92) * mm});
            skArc(sketch, "E72.3.9", {"start": v(-43.47, -54.92) * mm, "mid": v(-43.65, -55.66) * mm, "end": v(-43.25, -56.31) * mm});
            skPoint(sketch, "E72.4.0", {"position": v(-40.1, -63.88) * mm});
            skPoint(sketch, "E72.4.1", {"position": v(-46.14, -59.82) * mm});
            skPoint(sketch, "E72.4.2", {"position": v(-39.49, -61.98) * mm});
            skPoint(sketch, "E72.4.3", {"position": v(-46.76, -61.72) * mm});
            skLineSegment(sketch, "E72.4.4", {"start": v(-45.2, -60.13) * mm, "end": v(-40.44, -61.67) * mm});
            skLineSegment(sketch, "E72.4.5", {"start": v(-45.81, -62.03) * mm, "end": v(-41.05, -63.58) * mm});
            skArc(sketch, "E72.4.6", {"start": v(-41.05, -63.58) * mm, "mid": v(-40.3, -63.52) * mm, "end": v(-39.8, -62.93) * mm});
            skArc(sketch, "E72.4.7", {"start": v(-39.8, -62.93) * mm, "mid": v(-39.85, -62.17) * mm, "end": v(-40.44, -61.67) * mm});
            skArc(sketch, "E72.4.8", {"start": v(-45.2, -60.13) * mm, "mid": v(-45.96, -60.19) * mm, "end": v(-46.45, -60.77) * mm});
            skArc(sketch, "E72.4.9", {"start": v(-46.45, -60.77) * mm, "mid": v(-46.4, -61.53) * mm, "end": v(-45.81, -62.03) * mm});
            skPoint(sketch, "E72.5.0", {"position": v(-40.48, -68.26) * mm});
            skPoint(sketch, "E72.5.1", {"position": v(-47.48, -66.26) * mm});
            skPoint(sketch, "E72.5.2", {"position": v(-40.48, -66.26) * mm});
            skPoint(sketch, "E72.5.3", {"position": v(-47.48, -68.26) * mm});
            skLineSegment(sketch, "E72.5.4", {"start": v(-46.48, -66.26) * mm, "end": v(-41.48, -66.26) * mm});
            skLineSegment(sketch, "E72.5.5", {"start": v(-46.48, -68.26) * mm, "end": v(-41.48, -68.26) * mm});
            skArc(sketch, "E72.5.6", {"start": v(-41.48, -68.26) * mm, "mid": v(-40.77, -67.97) * mm, "end": v(-40.48, -67.26) * mm});
            skArc(sketch, "E72.5.7", {"start": v(-40.48, -67.26) * mm, "mid": v(-40.77, -66.55) * mm, "end": v(-41.48, -66.26) * mm});
            skArc(sketch, "E72.5.8", {"start": v(-46.48, -66.26) * mm, "mid": v(-47.19, -66.55) * mm, "end": v(-47.48, -67.26) * mm});
            skArc(sketch, "E72.5.9", {"start": v(-47.48, -67.26) * mm, "mid": v(-47.19, -67.97) * mm, "end": v(-46.48, -68.26) * mm});
            skPoint(sketch, "E72.6.0", {"position": v(-39.49, -72.54) * mm});
            skPoint(sketch, "E72.6.1", {"position": v(-46.76, -72.8) * mm});
            skPoint(sketch, "E72.6.2", {"position": v(-40.1, -70.64) * mm});
            skPoint(sketch, "E72.6.3", {"position": v(-46.14, -74.7) * mm});
            skLineSegment(sketch, "E72.6.4", {"start": v(-45.81, -72.49) * mm, "end": v(-41.05, -70.94) * mm});
            skLineSegment(sketch, "E72.6.5", {"start": v(-45.2, -74.4) * mm, "end": v(-40.44, -72.85) * mm});
            skArc(sketch, "E72.6.6", {"start": v(-40.44, -72.85) * mm, "mid": v(-39.85, -72.35) * mm, "end": v(-39.8, -71.59) * mm});
            skArc(sketch, "E72.6.7", {"start": v(-39.8, -71.59) * mm, "mid": v(-40.3, -71) * mm, "end": v(-41.05, -70.94) * mm});
            skArc(sketch, "E72.6.8", {"start": v(-45.81, -72.49) * mm, "mid": v(-46.4, -72.99) * mm, "end": v(-46.45, -73.75) * mm});
            skArc(sketch, "E72.6.9", {"start": v(-46.45, -73.75) * mm, "mid": v(-45.96, -74.33) * mm, "end": v(-45.2, -74.4) * mm});
            skPoint(sketch, "E72.7.0", {"position": v(-37.22, -76.3) * mm});
            skPoint(sketch, "E72.7.1", {"position": v(-44.06, -78.8) * mm});
            skPoint(sketch, "E72.7.2", {"position": v(-38.4, -74.68) * mm});
            skPoint(sketch, "E72.7.3", {"position": v(-42.88, -80.41) * mm});
            skLineSegment(sketch, "E72.7.4", {"start": v(-43.25, -78.2) * mm, "end": v(-39.2, -75.27) * mm});
            skLineSegment(sketch, "E72.7.5", {"start": v(-42.07, -79.82) * mm, "end": v(-38.03, -76.89) * mm});
            skArc(sketch, "E72.7.6", {"start": v(-38.03, -76.89) * mm, "mid": v(-37.63, -76.23) * mm, "end": v(-37.8, -75.49) * mm});
            skArc(sketch, "E72.7.7", {"start": v(-37.8, -75.49) * mm, "mid": v(-38.46, -75.09) * mm, "end": v(-39.2, -75.27) * mm});
            skArc(sketch, "E72.7.8", {"start": v(-43.25, -78.2) * mm, "mid": v(-43.65, -78.86) * mm, "end": v(-43.47, -79.6) * mm});
            skArc(sketch, "E72.7.9", {"start": v(-43.47, -79.6) * mm, "mid": v(-42.82, -80) * mm, "end": v(-42.07, -79.82) * mm});
            skPoint(sketch, "E72.8.0", {"position": v(-33.9, -79.17) * mm});
            skPoint(sketch, "E72.8.1", {"position": v(-39.63, -83.66) * mm});
            skPoint(sketch, "E72.8.2", {"position": v(-35.52, -78) * mm});
            skPoint(sketch, "E72.8.3", {"position": v(-38.01, -84.84) * mm});
            skLineSegment(sketch, "E72.8.4", {"start": v(-39.04, -82.85) * mm, "end": v(-36.1, -78.8) * mm});
            skLineSegment(sketch, "E72.8.5", {"start": v(-37.43, -84.03) * mm, "end": v(-34.49, -79.98) * mm});
            skArc(sketch, "E72.8.6", {"start": v(-34.49, -79.98) * mm, "mid": v(-34.3, -79.24) * mm, "end": v(-34.7, -78.59) * mm});
            skArc(sketch, "E72.8.7", {"start": v(-34.7, -78.59) * mm, "mid": v(-35.45, -78.4) * mm, "end": v(-36.1, -78.8) * mm});
            skArc(sketch, "E72.8.8", {"start": v(-39.04, -82.85) * mm, "mid": v(-39.22, -83.6) * mm, "end": v(-38.82, -84.25) * mm});
            skArc(sketch, "E72.8.9", {"start": v(-38.82, -84.25) * mm, "mid": v(-38.08, -84.43) * mm, "end": v(-37.43, -84.03) * mm});
            skPoint(sketch, "E72.9.0", {"position": v(-29.86, -80.88) * mm});
            skPoint(sketch, "E72.9.1", {"position": v(-33.92, -86.92) * mm});
            skPoint(sketch, "E72.9.2", {"position": v(-31.76, -80.27) * mm});
            skPoint(sketch, "E72.9.3", {"position": v(-32.02, -87.54) * mm});
            skLineSegment(sketch, "E72.9.4", {"start": v(-33.61, -85.97) * mm, "end": v(-32.07, -81.22) * mm});
            skLineSegment(sketch, "E72.9.5", {"start": v(-31.7, -86.6) * mm, "end": v(-30.16, -81.83) * mm});
            skArc(sketch, "E72.9.6", {"start": v(-30.16, -81.83) * mm, "mid": v(-30.22, -81.07) * mm, "end": v(-30.8, -80.57) * mm});
            skArc(sketch, "E72.9.7", {"start": v(-30.8, -80.57) * mm, "mid": v(-31.57, -80.63) * mm, "end": v(-32.07, -81.22) * mm});
            skArc(sketch, "E72.9.8", {"start": v(-33.61, -85.97) * mm, "mid": v(-33.55, -86.74) * mm, "end": v(-32.97, -87.23) * mm});
            skArc(sketch, "E72.9.9", {"start": v(-32.97, -87.23) * mm, "mid": v(-32.2, -87.17) * mm, "end": v(-31.7, -86.6) * mm});
            skPoint(sketch, "E72.10.0", {"position": v(-25.48, -81.26) * mm});
            skPoint(sketch, "E72.10.1", {"position": v(-27.48, -88.26) * mm});
            skPoint(sketch, "E72.10.2", {"position": v(-27.48, -81.26) * mm});
            skPoint(sketch, "E72.10.3", {"position": v(-25.48, -88.26) * mm});
            skLineSegment(sketch, "E72.10.4", {"start": v(-27.48, -87.26) * mm, "end": v(-27.48, -82.26) * mm});
            skLineSegment(sketch, "E72.10.5", {"start": v(-25.48, -87.26) * mm, "end": v(-25.48, -82.26) * mm});
            skArc(sketch, "E72.10.6", {"start": v(-25.48, -82.26) * mm, "mid": v(-25.77, -81.55) * mm, "end": v(-26.48, -81.26) * mm});
            skArc(sketch, "E72.10.7", {"start": v(-26.48, -81.26) * mm, "mid": v(-27.19, -81.55) * mm, "end": v(-27.48, -82.26) * mm});
            skArc(sketch, "E72.10.8", {"start": v(-27.48, -87.26) * mm, "mid": v(-27.19, -87.97) * mm, "end": v(-26.48, -88.26) * mm});
            skArc(sketch, "E72.10.9", {"start": v(-26.48, -88.26) * mm, "mid": v(-25.77, -87.97) * mm, "end": v(-25.48, -87.26) * mm});
            skPoint(sketch, "E72.11.0", {"position": v(-21.2, -80.27) * mm});
            skPoint(sketch, "E72.11.1", {"position": v(-20.94, -87.54) * mm});
            skPoint(sketch, "E72.11.2", {"position": v(-23.1, -80.88) * mm});
            skPoint(sketch, "E72.11.3", {"position": v(-19.04, -86.92) * mm});
            skLineSegment(sketch, "E72.11.4", {"start": v(-21.25, -86.6) * mm, "end": v(-22.8, -81.83) * mm});
            skLineSegment(sketch, "E72.11.5", {"start": v(-19.35, -85.97) * mm, "end": v(-20.9, -81.22) * mm});
            skArc(sketch, "E72.11.6", {"start": v(-20.9, -81.22) * mm, "mid": v(-21.4, -80.63) * mm, "end": v(-22.15, -80.57) * mm});
            skArc(sketch, "E72.11.7", {"start": v(-22.15, -80.57) * mm, "mid": v(-22.74, -81.07) * mm, "end": v(-22.8, -81.83) * mm});
            skArc(sketch, "E72.11.8", {"start": v(-21.25, -86.6) * mm, "mid": v(-20.75, -87.17) * mm, "end": v(-20, -87.23) * mm});
            skArc(sketch, "E72.11.9", {"start": v(-20, -87.23) * mm, "mid": v(-19.4, -86.74) * mm, "end": v(-19.35, -85.97) * mm});
            skPoint(sketch, "E72.12.0", {"position": v(-17.44, -78) * mm});
            skPoint(sketch, "E72.12.1", {"position": v(-14.95, -84.84) * mm});
            skPoint(sketch, "E72.12.2", {"position": v(-19.06, -79.17) * mm});
            skPoint(sketch, "E72.12.3", {"position": v(-13.33, -83.66) * mm});
            skLineSegment(sketch, "E72.12.4", {"start": v(-15.53, -84.03) * mm, "end": v(-18.47, -79.98) * mm});
            skLineSegment(sketch, "E72.12.5", {"start": v(-13.92, -82.85) * mm, "end": v(-16.85, -78.8) * mm});
            skArc(sketch, "E72.12.6", {"start": v(-16.85, -78.8) * mm, "mid": v(-17.5, -78.4) * mm, "end": v(-18.25, -78.59) * mm});
            skArc(sketch, "E72.12.7", {"start": v(-18.25, -78.59) * mm, "mid": v(-18.65, -79.24) * mm, "end": v(-18.47, -79.98) * mm});
            skArc(sketch, "E72.12.8", {"start": v(-15.53, -84.03) * mm, "mid": v(-14.88, -84.43) * mm, "end": v(-14.14, -84.25) * mm});
            skArc(sketch, "E72.12.9", {"start": v(-14.14, -84.25) * mm, "mid": v(-13.74, -83.6) * mm, "end": v(-13.92, -82.85) * mm});
            skPoint(sketch, "E72.13.0", {"position": v(-14.57, -74.68) * mm});
            skPoint(sketch, "E72.13.1", {"position": v(-10.08, -80.41) * mm});
            skPoint(sketch, "E72.13.2", {"position": v(-15.74, -76.3) * mm});
            skPoint(sketch, "E72.13.3", {"position": v(-8.9, -78.8) * mm});
            skLineSegment(sketch, "E72.13.4", {"start": v(-10.89, -79.82) * mm, "end": v(-14.93, -76.89) * mm});
            skLineSegment(sketch, "E72.13.5", {"start": v(-9.71, -78.2) * mm, "end": v(-13.76, -75.27) * mm});
            skArc(sketch, "E72.13.6", {"start": v(-13.76, -75.27) * mm, "mid": v(-14.5, -75.09) * mm, "end": v(-15.15, -75.49) * mm});
            skArc(sketch, "E72.13.7", {"start": v(-15.15, -75.49) * mm, "mid": v(-15.33, -76.23) * mm, "end": v(-14.93, -76.89) * mm});
            skArc(sketch, "E72.13.8", {"start": v(-10.89, -79.82) * mm, "mid": v(-10.14, -80) * mm, "end": v(-9.5, -79.6) * mm});
            skArc(sketch, "E72.13.9", {"start": v(-9.5, -79.6) * mm, "mid": v(-9.31, -78.86) * mm, "end": v(-9.71, -78.2) * mm});
            skPoint(sketch, "E72.14.0", {"position": v(-12.86, -70.64) * mm});
            skPoint(sketch, "E72.14.1", {"position": v(-6.82, -74.7) * mm});
            skPoint(sketch, "E72.14.2", {"position": v(-13.47, -72.54) * mm});
            skPoint(sketch, "E72.14.3", {"position": v(-6.2, -72.8) * mm});
            skLineSegment(sketch, "E72.14.4", {"start": v(-7.77, -74.4) * mm, "end": v(-12.52, -72.85) * mm});
            skLineSegment(sketch, "E72.14.5", {"start": v(-7.15, -72.49) * mm, "end": v(-11.9, -70.94) * mm});
            skArc(sketch, "E72.14.6", {"start": v(-11.9, -70.94) * mm, "mid": v(-12.67, -71) * mm, "end": v(-13.17, -71.59) * mm});
            skArc(sketch, "E72.14.7", {"start": v(-13.17, -71.59) * mm, "mid": v(-13.1, -72.35) * mm, "end": v(-12.52, -72.85) * mm});
            skArc(sketch, "E72.14.8", {"start": v(-7.77, -74.4) * mm, "mid": v(-7, -74.33) * mm, "end": v(-6.5, -73.75) * mm});
            skArc(sketch, "E72.14.9", {"start": v(-6.5, -73.75) * mm, "mid": v(-6.57, -72.99) * mm, "end": v(-7.15, -72.49) * mm});
            skPoint(sketch, "E72.15.0", {"position": v(-12.48, -66.26) * mm});
            skPoint(sketch, "E72.15.1", {"position": v(-5.48, -68.26) * mm});
            skPoint(sketch, "E72.15.2", {"position": v(-12.48, -68.26) * mm});
            skPoint(sketch, "E72.15.3", {"position": v(-5.48, -66.26) * mm});
            skLineSegment(sketch, "E72.15.4", {"start": v(-6.48, -68.26) * mm, "end": v(-11.48, -68.26) * mm});
            skLineSegment(sketch, "E72.15.5", {"start": v(-6.48, -66.26) * mm, "end": v(-11.48, -66.26) * mm});
            skArc(sketch, "E72.15.6", {"start": v(-11.48, -66.26) * mm, "mid": v(-12.19, -66.55) * mm, "end": v(-12.48, -67.26) * mm});
            skArc(sketch, "E72.15.7", {"start": v(-12.48, -67.26) * mm, "mid": v(-12.19, -67.97) * mm, "end": v(-11.48, -68.26) * mm});
            skArc(sketch, "E72.15.8", {"start": v(-6.48, -68.26) * mm, "mid": v(-5.77, -67.97) * mm, "end": v(-5.48, -67.26) * mm});
            skArc(sketch, "E72.15.9", {"start": v(-5.48, -67.26) * mm, "mid": v(-5.77, -66.55) * mm, "end": v(-6.48, -66.26) * mm});
            skPoint(sketch, "E72.16.0", {"position": v(-13.47, -61.98) * mm});
            skPoint(sketch, "E72.16.1", {"position": v(-6.2, -61.72) * mm});
            skPoint(sketch, "E72.16.2", {"position": v(-12.86, -63.88) * mm});
            skPoint(sketch, "E72.16.3", {"position": v(-6.82, -59.82) * mm});
            skLineSegment(sketch, "E72.16.4", {"start": v(-7.15, -62.03) * mm, "end": v(-11.9, -63.58) * mm});
            skLineSegment(sketch, "E72.16.5", {"start": v(-7.77, -60.13) * mm, "end": v(-12.52, -61.67) * mm});
            skArc(sketch, "E72.16.6", {"start": v(-12.52, -61.67) * mm, "mid": v(-13.1, -62.17) * mm, "end": v(-13.17, -62.93) * mm});
            skArc(sketch, "E72.16.7", {"start": v(-13.17, -62.93) * mm, "mid": v(-12.67, -63.52) * mm, "end": v(-11.9, -63.58) * mm});
            skArc(sketch, "E72.16.8", {"start": v(-7.15, -62.03) * mm, "mid": v(-6.57, -61.53) * mm, "end": v(-6.5, -60.77) * mm});
            skArc(sketch, "E72.16.9", {"start": v(-6.5, -60.77) * mm, "mid": v(-7, -60.19) * mm, "end": v(-7.77, -60.13) * mm});
            skPoint(sketch, "E72.17.0", {"position": v(-15.74, -58.22) * mm});
            skPoint(sketch, "E72.17.1", {"position": v(-8.9, -55.73) * mm});
            skPoint(sketch, "E72.17.2", {"position": v(-14.57, -59.84) * mm});
            skPoint(sketch, "E72.17.3", {"position": v(-10.08, -54.1) * mm});
            skLineSegment(sketch, "E72.17.4", {"start": v(-9.71, -56.31) * mm, "end": v(-13.76, -59.25) * mm});
            skLineSegment(sketch, "E72.17.5", {"start": v(-10.89, -54.7) * mm, "end": v(-14.93, -57.63) * mm});
            skArc(sketch, "E72.17.6", {"start": v(-14.93, -57.63) * mm, "mid": v(-15.33, -58.29) * mm, "end": v(-15.15, -59.03) * mm});
            skArc(sketch, "E72.17.7", {"start": v(-15.15, -59.03) * mm, "mid": v(-14.5, -59.43) * mm, "end": v(-13.76, -59.25) * mm});
            skArc(sketch, "E72.17.8", {"start": v(-9.71, -56.31) * mm, "mid": v(-9.31, -55.66) * mm, "end": v(-9.5, -54.92) * mm});
            skArc(sketch, "E72.17.9", {"start": v(-9.5, -54.92) * mm, "mid": v(-10.14, -54.52) * mm, "end": v(-10.89, -54.7) * mm});
            skPoint(sketch, "E72.18.0", {"position": v(-19.06, -55.35) * mm});
            skPoint(sketch, "E72.18.1", {"position": v(-13.33, -50.86) * mm});
            skPoint(sketch, "E72.18.2", {"position": v(-17.44, -56.52) * mm});
            skPoint(sketch, "E72.18.3", {"position": v(-14.95, -49.68) * mm});
            skLineSegment(sketch, "E72.18.4", {"start": v(-13.92, -51.67) * mm, "end": v(-16.85, -55.71) * mm});
            skLineSegment(sketch, "E72.18.5", {"start": v(-15.53, -50.5) * mm, "end": v(-18.47, -54.54) * mm});
            skArc(sketch, "E72.18.6", {"start": v(-18.47, -54.54) * mm, "mid": v(-18.65, -55.28) * mm, "end": v(-18.25, -55.93) * mm});
            skArc(sketch, "E72.18.7", {"start": v(-18.25, -55.93) * mm, "mid": v(-17.5, -56.11) * mm, "end": v(-16.85, -55.71) * mm});
            skArc(sketch, "E72.18.8", {"start": v(-13.92, -51.67) * mm, "mid": v(-13.74, -50.92) * mm, "end": v(-14.14, -50.27) * mm});
            skArc(sketch, "E72.18.9", {"start": v(-14.14, -50.27) * mm, "mid": v(-14.88, -50.1) * mm, "end": v(-15.53, -50.5) * mm});
            skPoint(sketch, "E72.19.0", {"position": v(-23.1, -53.64) * mm});
            skPoint(sketch, "E72.19.1", {"position": v(-19.04, -47.6) * mm});
            skPoint(sketch, "E72.19.2", {"position": v(-21.2, -54.25) * mm});
            skPoint(sketch, "E72.19.3", {"position": v(-20.94, -46.98) * mm});
            skLineSegment(sketch, "E72.19.4", {"start": v(-19.35, -48.55) * mm, "end": v(-20.9, -53.3) * mm});
            skLineSegment(sketch, "E72.19.5", {"start": v(-21.25, -47.93) * mm, "end": v(-22.8, -52.69) * mm});
            skArc(sketch, "E72.19.6", {"start": v(-22.8, -52.69) * mm, "mid": v(-22.74, -53.45) * mm, "end": v(-22.15, -53.95) * mm});
            skArc(sketch, "E72.19.7", {"start": v(-22.15, -53.95) * mm, "mid": v(-21.4, -53.89) * mm, "end": v(-20.9, -53.3) * mm});
            skArc(sketch, "E72.19.8", {"start": v(-19.35, -48.55) * mm, "mid": v(-19.4, -47.78) * mm, "end": v(-20, -47.29) * mm});
            skArc(sketch, "E72.19.9", {"start": v(-20, -47.29) * mm, "mid": v(-20.75, -47.35) * mm, "end": v(-21.25, -47.93) * mm});
            skArc(sketch, "E73.1.0", {"start": v(-80.33, -34.25) * mm, "mid": v(-79.83, -34.84) * mm, "end": v(-79.07, -34.9) * mm});
            skPoint(sketch, "E73.1.1", {"position": v(-82.18, -28.55) * mm});
            skArc(sketch, "E73.1.2", {"start": v(-79.97, -28.88) * mm, "mid": v(-80.47, -28.3) * mm, "end": v(-81.23, -28.24) * mm});
            skArc(sketch, "E73.1.3", {"start": v(-79.07, -34.9) * mm, "mid": v(-78.48, -34.4) * mm, "end": v(-78.42, -33.64) * mm});
            skArc(sketch, "E73.1.4", {"start": v(-81.23, -28.24) * mm, "mid": v(-81.81, -28.73) * mm, "end": v(-81.87, -29.5) * mm});
            skPoint(sketch, "E73.1.5", {"position": v(-78.12, -34.59) * mm});
            skPoint(sketch, "E73.1.6", {"position": v(-80.28, -27.93) * mm});
            skPoint(sketch, "E73.1.7", {"position": v(-80.02, -35.2) * mm});
            skLineSegment(sketch, "E73.1.8", {"start": v(-79.97, -28.88) * mm, "end": v(-78.42, -33.64) * mm});
            skLineSegment(sketch, "E73.1.9", {"start": v(-81.87, -29.5) * mm, "end": v(-80.33, -34.25) * mm});
            skArc(sketch, "E73.2.0", {"start": v(-84.37, -36.66) * mm, "mid": v(-83.71, -37.06) * mm, "end": v(-82.97, -36.88) * mm});
            skPoint(sketch, "E73.2.1", {"position": v(-87.9, -31.8) * mm});
            skArc(sketch, "E73.2.2", {"start": v(-85.69, -31.44) * mm, "mid": v(-86.34, -31.04) * mm, "end": v(-87.08, -31.22) * mm});
            skArc(sketch, "E73.2.3", {"start": v(-82.97, -36.88) * mm, "mid": v(-82.57, -36.23) * mm, "end": v(-82.75, -35.49) * mm});
            skArc(sketch, "E73.2.4", {"start": v(-87.08, -31.22) * mm, "mid": v(-87.48, -31.87) * mm, "end": v(-87.3, -32.62) * mm});
            skPoint(sketch, "E73.2.5", {"position": v(-82.16, -36.3) * mm});
            skPoint(sketch, "E73.2.6", {"position": v(-86.27, -30.63) * mm});
            skPoint(sketch, "E73.2.7", {"position": v(-83.78, -37.47) * mm});
            skLineSegment(sketch, "E73.2.8", {"start": v(-85.69, -31.44) * mm, "end": v(-82.75, -35.49) * mm});
            skLineSegment(sketch, "E73.2.9", {"start": v(-87.3, -32.62) * mm, "end": v(-84.37, -36.66) * mm});
            skArc(sketch, "E73.3.0", {"start": v(-87.46, -40.2) * mm, "mid": v(-86.72, -40.38) * mm, "end": v(-86.07, -39.98) * mm});
            skPoint(sketch, "E73.3.1", {"position": v(-92.32, -36.68) * mm});
            skArc(sketch, "E73.3.2", {"start": v(-90.33, -35.65) * mm, "mid": v(-91.08, -35.47) * mm, "end": v(-91.73, -35.87) * mm});
            skArc(sketch, "E73.3.3", {"start": v(-86.07, -39.98) * mm, "mid": v(-85.89, -39.24) * mm, "end": v(-86.29, -38.58) * mm});
            skArc(sketch, "E73.3.4", {"start": v(-91.73, -35.87) * mm, "mid": v(-91.9, -36.61) * mm, "end": v(-91.5, -37.26) * mm});
            skPoint(sketch, "E73.3.5", {"position": v(-85.48, -39.17) * mm});
            skPoint(sketch, "E73.3.6", {"position": v(-91.14, -35.06) * mm});
            skPoint(sketch, "E73.3.7", {"position": v(-86.65, -40.8) * mm});
            skLineSegment(sketch, "E73.3.8", {"start": v(-90.33, -35.65) * mm, "end": v(-86.29, -38.58) * mm});
            skLineSegment(sketch, "E73.3.9", {"start": v(-91.5, -37.26) * mm, "end": v(-87.46, -40.2) * mm});
            skArc(sketch, "E73.4.0", {"start": v(-89.31, -44.53) * mm, "mid": v(-88.55, -44.47) * mm, "end": v(-88.05, -43.88) * mm});
            skPoint(sketch, "E73.4.1", {"position": v(-95.02, -42.67) * mm});
            skArc(sketch, "E73.4.2", {"start": v(-93.45, -41.08) * mm, "mid": v(-94.22, -41.14) * mm, "end": v(-94.71, -41.72) * mm});
            skArc(sketch, "E73.4.3", {"start": v(-88.05, -43.88) * mm, "mid": v(-88.11, -43.12) * mm, "end": v(-88.7, -42.62) * mm});
            skArc(sketch, "E73.4.4", {"start": v(-94.71, -41.72) * mm, "mid": v(-94.65, -42.48) * mm, "end": v(-94.07, -42.98) * mm});
            skPoint(sketch, "E73.4.5", {"position": v(-87.75, -42.93) * mm});
            skPoint(sketch, "E73.4.6", {"position": v(-94.4, -40.77) * mm});
            skPoint(sketch, "E73.4.7", {"position": v(-88.36, -44.83) * mm});
            skLineSegment(sketch, "E73.4.8", {"start": v(-93.45, -41.08) * mm, "end": v(-88.7, -42.62) * mm});
            skLineSegment(sketch, "E73.4.9", {"start": v(-94.07, -42.98) * mm, "end": v(-89.31, -44.53) * mm});
            skArc(sketch, "E73.5.0", {"start": v(-89.74, -49.21) * mm, "mid": v(-89.03, -48.92) * mm, "end": v(-88.74, -48.21) * mm});
            skPoint(sketch, "E73.5.1", {"position": v(-95.74, -49.21) * mm});
            skArc(sketch, "E73.5.2", {"start": v(-94.74, -47.21) * mm, "mid": v(-95.45, -47.5) * mm, "end": v(-95.74, -48.21) * mm});
            skArc(sketch, "E73.5.3", {"start": v(-88.74, -48.21) * mm, "mid": v(-89.03, -47.5) * mm, "end": v(-89.74, -47.21) * mm});
            skArc(sketch, "E73.5.4", {"start": v(-95.74, -48.21) * mm, "mid": v(-95.45, -48.92) * mm, "end": v(-94.74, -49.21) * mm});
            skPoint(sketch, "E73.5.5", {"position": v(-88.74, -47.21) * mm});
            skPoint(sketch, "E73.5.6", {"position": v(-95.74, -47.21) * mm});
            skPoint(sketch, "E73.5.7", {"position": v(-88.74, -49.21) * mm});
            skLineSegment(sketch, "E73.5.8", {"start": v(-94.74, -47.21) * mm, "end": v(-89.74, -47.21) * mm});
            skLineSegment(sketch, "E73.5.9", {"start": v(-94.74, -49.21) * mm, "end": v(-89.74, -49.21) * mm});
            skArc(sketch, "E73.6.0", {"start": v(-88.7, -53.8) * mm, "mid": v(-88.11, -53.3) * mm, "end": v(-88.05, -52.54) * mm});
            skPoint(sketch, "E73.6.1", {"position": v(-94.4, -55.65) * mm});
            skArc(sketch, "E73.6.2", {"start": v(-94.07, -53.44) * mm, "mid": v(-94.65, -53.94) * mm, "end": v(-94.71, -54.7) * mm});
            skArc(sketch, "E73.6.3", {"start": v(-88.05, -52.54) * mm, "mid": v(-88.55, -51.95) * mm, "end": v(-89.31, -51.9) * mm});
            skArc(sketch, "E73.6.4", {"start": v(-94.71, -54.7) * mm, "mid": v(-94.22, -55.28) * mm, "end": v(-93.45, -55.34) * mm});
            skPoint(sketch, "E73.6.5", {"position": v(-88.36, -51.59) * mm});
            skPoint(sketch, "E73.6.6", {"position": v(-95.02, -53.75) * mm});
            skPoint(sketch, "E73.6.7", {"position": v(-87.75, -53.49) * mm});
            skLineSegment(sketch, "E73.6.8", {"start": v(-94.07, -53.44) * mm, "end": v(-89.31, -51.9) * mm});
            skLineSegment(sketch, "E73.6.9", {"start": v(-93.45, -55.34) * mm, "end": v(-88.7, -53.8) * mm});
            skArc(sketch, "E73.7.0", {"start": v(-86.29, -57.84) * mm, "mid": v(-85.89, -57.18) * mm, "end": v(-86.07, -56.44) * mm});
            skPoint(sketch, "E73.7.1", {"position": v(-91.14, -61.36) * mm});
            skArc(sketch, "E73.7.2", {"start": v(-91.5, -59.16) * mm, "mid": v(-91.9, -59.8) * mm, "end": v(-91.73, -60.55) * mm});
            skArc(sketch, "E73.7.3", {"start": v(-86.07, -56.44) * mm, "mid": v(-86.72, -56.04) * mm, "end": v(-87.46, -56.22) * mm});
            skArc(sketch, "E73.7.4", {"start": v(-91.73, -60.55) * mm, "mid": v(-91.08, -60.95) * mm, "end": v(-90.33, -60.77) * mm});
            skPoint(sketch, "E73.7.5", {"position": v(-86.65, -55.63) * mm});
            skPoint(sketch, "E73.7.6", {"position": v(-92.32, -59.74) * mm});
            skPoint(sketch, "E73.7.7", {"position": v(-85.48, -57.25) * mm});
            skLineSegment(sketch, "E73.7.8", {"start": v(-91.5, -59.16) * mm, "end": v(-87.46, -56.22) * mm});
            skLineSegment(sketch, "E73.7.9", {"start": v(-90.33, -60.77) * mm, "end": v(-86.29, -57.84) * mm});
            skArc(sketch, "E73.8.0", {"start": v(-82.75, -60.93) * mm, "mid": v(-82.57, -60.19) * mm, "end": v(-82.97, -59.54) * mm});
            skPoint(sketch, "E73.8.1", {"position": v(-86.27, -65.79) * mm});
            skArc(sketch, "E73.8.2", {"start": v(-87.3, -63.8) * mm, "mid": v(-87.48, -64.55) * mm, "end": v(-87.08, -65.2) * mm});
            skArc(sketch, "E73.8.3", {"start": v(-82.97, -59.54) * mm, "mid": v(-83.71, -59.36) * mm, "end": v(-84.37, -59.76) * mm});
            skArc(sketch, "E73.8.4", {"start": v(-87.08, -65.2) * mm, "mid": v(-86.34, -65.38) * mm, "end": v(-85.69, -64.98) * mm});
            skPoint(sketch, "E73.8.5", {"position": v(-83.78, -58.95) * mm});
            skPoint(sketch, "E73.8.6", {"position": v(-87.9, -64.61) * mm});
            skPoint(sketch, "E73.8.7", {"position": v(-82.16, -60.12) * mm});
            skLineSegment(sketch, "E73.8.8", {"start": v(-87.3, -63.8) * mm, "end": v(-84.37, -59.76) * mm});
            skLineSegment(sketch, "E73.8.9", {"start": v(-85.69, -64.98) * mm, "end": v(-82.75, -60.93) * mm});
            skArc(sketch, "E73.9.0", {"start": v(-78.42, -62.78) * mm, "mid": v(-78.48, -62.02) * mm, "end": v(-79.07, -61.52) * mm});
            skPoint(sketch, "E73.9.1", {"position": v(-80.28, -68.5) * mm});
            skArc(sketch, "E73.9.2", {"start": v(-81.87, -66.92) * mm, "mid": v(-81.81, -67.69) * mm, "end": v(-81.23, -68.18) * mm});
            skArc(sketch, "E73.9.3", {"start": v(-79.07, -61.52) * mm, "mid": v(-79.83, -61.58) * mm, "end": v(-80.33, -62.17) * mm});
            skArc(sketch, "E73.9.4", {"start": v(-81.23, -68.18) * mm, "mid": v(-80.47, -68.12) * mm, "end": v(-79.97, -67.54) * mm});
            skPoint(sketch, "E73.9.5", {"position": v(-80.02, -61.22) * mm});
            skPoint(sketch, "E73.9.6", {"position": v(-82.18, -67.87) * mm});
            skPoint(sketch, "E73.9.7", {"position": v(-78.12, -61.83) * mm});
            skLineSegment(sketch, "E73.9.8", {"start": v(-81.87, -66.92) * mm, "end": v(-80.33, -62.17) * mm});
            skLineSegment(sketch, "E73.9.9", {"start": v(-79.97, -67.54) * mm, "end": v(-78.42, -62.78) * mm});
            skArc(sketch, "E73.10.0", {"start": v(-73.74, -63.21) * mm, "mid": v(-74.03, -62.5) * mm, "end": v(-74.74, -62.21) * mm});
            skPoint(sketch, "E73.10.1", {"position": v(-73.74, -69.21) * mm});
            skArc(sketch, "E73.10.2", {"start": v(-75.74, -68.21) * mm, "mid": v(-75.45, -68.92) * mm, "end": v(-74.74, -69.21) * mm});
            skArc(sketch, "E73.10.3", {"start": v(-74.74, -62.21) * mm, "mid": v(-75.45, -62.5) * mm, "end": v(-75.74, -63.21) * mm});
            skArc(sketch, "E73.10.4", {"start": v(-74.74, -69.21) * mm, "mid": v(-74.03, -68.92) * mm, "end": v(-73.74, -68.21) * mm});
            skPoint(sketch, "E73.10.5", {"position": v(-75.74, -62.21) * mm});
            skPoint(sketch, "E73.10.6", {"position": v(-75.74, -69.21) * mm});
            skPoint(sketch, "E73.10.7", {"position": v(-73.74, -62.21) * mm});
            skLineSegment(sketch, "E73.10.8", {"start": v(-75.74, -68.21) * mm, "end": v(-75.74, -63.21) * mm});
            skLineSegment(sketch, "E73.10.9", {"start": v(-73.74, -68.21) * mm, "end": v(-73.74, -63.21) * mm});
            skArc(sketch, "E73.11.0", {"start": v(-69.15, -62.17) * mm, "mid": v(-69.65, -61.58) * mm, "end": v(-70.41, -61.52) * mm});
            skPoint(sketch, "E73.11.1", {"position": v(-67.3, -67.87) * mm});
            skArc(sketch, "E73.11.2", {"start": v(-69.51, -67.54) * mm, "mid": v(-69.01, -68.12) * mm, "end": v(-68.25, -68.18) * mm});
            skArc(sketch, "E73.11.3", {"start": v(-70.41, -61.52) * mm, "mid": v(-71, -62.02) * mm, "end": v(-71.06, -62.78) * mm});
            skArc(sketch, "E73.11.4", {"start": v(-68.25, -68.18) * mm, "mid": v(-67.67, -67.69) * mm, "end": v(-67.6, -66.92) * mm});
            skPoint(sketch, "E73.11.5", {"position": v(-71.36, -61.83) * mm});
            skPoint(sketch, "E73.11.6", {"position": v(-69.2, -68.5) * mm});
            skPoint(sketch, "E73.11.7", {"position": v(-69.46, -61.22) * mm});
            skLineSegment(sketch, "E73.11.8", {"start": v(-69.51, -67.54) * mm, "end": v(-71.06, -62.78) * mm});
            skLineSegment(sketch, "E73.11.9", {"start": v(-67.6, -66.92) * mm, "end": v(-69.15, -62.17) * mm});
            skArc(sketch, "E73.12.0", {"start": v(-65.11, -59.76) * mm, "mid": v(-65.77, -59.36) * mm, "end": v(-66.51, -59.54) * mm});
            skPoint(sketch, "E73.12.1", {"position": v(-61.59, -64.61) * mm});
            skArc(sketch, "E73.12.2", {"start": v(-63.8, -64.98) * mm, "mid": v(-63.14, -65.38) * mm, "end": v(-62.4, -65.2) * mm});
            skArc(sketch, "E73.12.3", {"start": v(-66.51, -59.54) * mm, "mid": v(-66.91, -60.19) * mm, "end": v(-66.73, -60.93) * mm});
            skArc(sketch, "E73.12.4", {"start": v(-62.4, -65.2) * mm, "mid": v(-62, -64.55) * mm, "end": v(-62.18, -63.8) * mm});
            skPoint(sketch, "E73.12.5", {"position": v(-67.32, -60.12) * mm});
            skPoint(sketch, "E73.12.6", {"position": v(-63.2, -65.79) * mm});
            skPoint(sketch, "E73.12.7", {"position": v(-65.7, -58.95) * mm});
            skLineSegment(sketch, "E73.12.8", {"start": v(-63.8, -64.98) * mm, "end": v(-66.73, -60.93) * mm});
            skLineSegment(sketch, "E73.12.9", {"start": v(-62.18, -63.8) * mm, "end": v(-65.11, -59.76) * mm});
            skArc(sketch, "E73.13.0", {"start": v(-62.02, -56.22) * mm, "mid": v(-62.76, -56.04) * mm, "end": v(-63.41, -56.44) * mm});
            skPoint(sketch, "E73.13.1", {"position": v(-57.16, -59.74) * mm});
            skArc(sketch, "E73.13.2", {"start": v(-59.15, -60.77) * mm, "mid": v(-58.4, -60.95) * mm, "end": v(-57.75, -60.55) * mm});
            skArc(sketch, "E73.13.3", {"start": v(-63.41, -56.44) * mm, "mid": v(-63.6, -57.18) * mm, "end": v(-63.2, -57.84) * mm});
            skArc(sketch, "E73.13.4", {"start": v(-57.75, -60.55) * mm, "mid": v(-57.57, -59.8) * mm, "end": v(-57.97, -59.16) * mm});
            skPoint(sketch, "E73.13.5", {"position": v(-64, -57.25) * mm});
            skPoint(sketch, "E73.13.6", {"position": v(-58.34, -61.36) * mm});
            skPoint(sketch, "E73.13.7", {"position": v(-62.83, -55.63) * mm});
            skLineSegment(sketch, "E73.13.8", {"start": v(-59.15, -60.77) * mm, "end": v(-63.2, -57.84) * mm});
            skLineSegment(sketch, "E73.13.9", {"start": v(-57.97, -59.16) * mm, "end": v(-62.02, -56.22) * mm});
            skArc(sketch, "E73.14.0", {"start": v(-60.17, -51.9) * mm, "mid": v(-60.93, -51.95) * mm, "end": v(-61.43, -52.54) * mm});
            skPoint(sketch, "E73.14.1", {"position": v(-54.46, -53.75) * mm});
            skArc(sketch, "E73.14.2", {"start": v(-56.03, -55.34) * mm, "mid": v(-55.26, -55.28) * mm, "end": v(-54.77, -54.7) * mm});
            skArc(sketch, "E73.14.3", {"start": v(-61.43, -52.54) * mm, "mid": v(-61.37, -53.3) * mm, "end": v(-60.78, -53.8) * mm});
            skArc(sketch, "E73.14.4", {"start": v(-54.77, -54.7) * mm, "mid": v(-54.83, -53.94) * mm, "end": v(-55.4, -53.44) * mm});
            skPoint(sketch, "E73.14.5", {"position": v(-61.73, -53.49) * mm});
            skPoint(sketch, "E73.14.6", {"position": v(-55.08, -55.65) * mm});
            skPoint(sketch, "E73.14.7", {"position": v(-61.12, -51.59) * mm});
            skLineSegment(sketch, "E73.14.8", {"start": v(-56.03, -55.34) * mm, "end": v(-60.78, -53.8) * mm});
            skLineSegment(sketch, "E73.14.9", {"start": v(-55.4, -53.44) * mm, "end": v(-60.17, -51.9) * mm});
            skArc(sketch, "E73.15.0", {"start": v(-59.74, -47.21) * mm, "mid": v(-60.45, -47.5) * mm, "end": v(-60.74, -48.21) * mm});
            skPoint(sketch, "E73.15.1", {"position": v(-53.74, -47.21) * mm});
            skArc(sketch, "E73.15.2", {"start": v(-54.74, -49.21) * mm, "mid": v(-54.03, -48.92) * mm, "end": v(-53.74, -48.21) * mm});
            skArc(sketch, "E73.15.3", {"start": v(-60.74, -48.21) * mm, "mid": v(-60.45, -48.92) * mm, "end": v(-59.74, -49.21) * mm});
            skArc(sketch, "E73.15.4", {"start": v(-53.74, -48.21) * mm, "mid": v(-54.03, -47.5) * mm, "end": v(-54.74, -47.21) * mm});
            skPoint(sketch, "E73.15.5", {"position": v(-60.74, -49.21) * mm});
            skPoint(sketch, "E73.15.6", {"position": v(-53.74, -49.21) * mm});
            skPoint(sketch, "E73.15.7", {"position": v(-60.74, -47.21) * mm});
            skLineSegment(sketch, "E73.15.8", {"start": v(-54.74, -49.21) * mm, "end": v(-59.74, -49.21) * mm});
            skLineSegment(sketch, "E73.15.9", {"start": v(-54.74, -47.21) * mm, "end": v(-59.74, -47.21) * mm});
            skArc(sketch, "E73.16.0", {"start": v(-60.78, -42.62) * mm, "mid": v(-61.37, -43.12) * mm, "end": v(-61.43, -43.88) * mm});
            skPoint(sketch, "E73.16.1", {"position": v(-55.08, -40.77) * mm});
            skArc(sketch, "E73.16.2", {"start": v(-55.4, -42.98) * mm, "mid": v(-54.83, -42.48) * mm, "end": v(-54.77, -41.72) * mm});
            skArc(sketch, "E73.16.3", {"start": v(-61.43, -43.88) * mm, "mid": v(-60.93, -44.47) * mm, "end": v(-60.17, -44.53) * mm});
            skArc(sketch, "E73.16.4", {"start": v(-54.77, -41.72) * mm, "mid": v(-55.26, -41.14) * mm, "end": v(-56.03, -41.08) * mm});
            skPoint(sketch, "E73.16.5", {"position": v(-61.12, -44.83) * mm});
            skPoint(sketch, "E73.16.6", {"position": v(-54.46, -42.67) * mm});
            skPoint(sketch, "E73.16.7", {"position": v(-61.73, -42.93) * mm});
            skLineSegment(sketch, "E73.16.8", {"start": v(-55.4, -42.98) * mm, "end": v(-60.17, -44.53) * mm});
            skLineSegment(sketch, "E73.16.9", {"start": v(-56.03, -41.08) * mm, "end": v(-60.78, -42.62) * mm});
            skArc(sketch, "E73.17.0", {"start": v(-63.2, -38.58) * mm, "mid": v(-63.6, -39.24) * mm, "end": v(-63.41, -39.98) * mm});
            skPoint(sketch, "E73.17.1", {"position": v(-58.34, -35.06) * mm});
            skArc(sketch, "E73.17.2", {"start": v(-57.97, -37.26) * mm, "mid": v(-57.57, -36.61) * mm, "end": v(-57.75, -35.87) * mm});
            skArc(sketch, "E73.17.3", {"start": v(-63.41, -39.98) * mm, "mid": v(-62.76, -40.38) * mm, "end": v(-62.02, -40.2) * mm});
            skArc(sketch, "E73.17.4", {"start": v(-57.75, -35.87) * mm, "mid": v(-58.4, -35.47) * mm, "end": v(-59.15, -35.65) * mm});
            skPoint(sketch, "E73.17.5", {"position": v(-62.83, -40.8) * mm});
            skPoint(sketch, "E73.17.6", {"position": v(-57.16, -36.68) * mm});
            skPoint(sketch, "E73.17.7", {"position": v(-64, -39.17) * mm});
            skLineSegment(sketch, "E73.17.8", {"start": v(-57.97, -37.26) * mm, "end": v(-62.02, -40.2) * mm});
            skLineSegment(sketch, "E73.17.9", {"start": v(-59.15, -35.65) * mm, "end": v(-63.2, -38.58) * mm});
            skArc(sketch, "E73.18.0", {"start": v(-66.73, -35.49) * mm, "mid": v(-66.91, -36.23) * mm, "end": v(-66.51, -36.88) * mm});
            skPoint(sketch, "E73.18.1", {"position": v(-63.2, -30.63) * mm});
            skArc(sketch, "E73.18.2", {"start": v(-62.18, -32.62) * mm, "mid": v(-62, -31.87) * mm, "end": v(-62.4, -31.22) * mm});
            skArc(sketch, "E73.18.3", {"start": v(-66.51, -36.88) * mm, "mid": v(-65.77, -37.06) * mm, "end": v(-65.11, -36.66) * mm});
            skArc(sketch, "E73.18.4", {"start": v(-62.4, -31.22) * mm, "mid": v(-63.14, -31.04) * mm, "end": v(-63.8, -31.44) * mm});
            skPoint(sketch, "E73.18.5", {"position": v(-65.7, -37.47) * mm});
            skPoint(sketch, "E73.18.6", {"position": v(-61.59, -31.8) * mm});
            skPoint(sketch, "E73.18.7", {"position": v(-67.32, -36.3) * mm});
            skLineSegment(sketch, "E73.18.8", {"start": v(-62.18, -32.62) * mm, "end": v(-65.11, -36.66) * mm});
            skLineSegment(sketch, "E73.18.9", {"start": v(-63.8, -31.44) * mm, "end": v(-66.73, -35.49) * mm});
            skArc(sketch, "E73.19.0", {"start": v(-71.06, -33.64) * mm, "mid": v(-71, -34.4) * mm, "end": v(-70.41, -34.9) * mm});
            skPoint(sketch, "E73.19.1", {"position": v(-69.2, -27.93) * mm});
            skArc(sketch, "E73.19.2", {"start": v(-67.6, -29.5) * mm, "mid": v(-67.67, -28.73) * mm, "end": v(-68.25, -28.24) * mm});
            skArc(sketch, "E73.19.3", {"start": v(-70.41, -34.9) * mm, "mid": v(-69.65, -34.84) * mm, "end": v(-69.15, -34.25) * mm});
            skArc(sketch, "E73.19.4", {"start": v(-68.25, -28.24) * mm, "mid": v(-69.01, -28.3) * mm, "end": v(-69.51, -28.88) * mm});
            skPoint(sketch, "E73.19.5", {"position": v(-69.46, -35.2) * mm});
            skPoint(sketch, "E73.19.6", {"position": v(-67.3, -28.55) * mm});
            skPoint(sketch, "E73.19.7", {"position": v(-71.36, -34.59) * mm});
            skLineSegment(sketch, "E73.19.8", {"start": v(-67.6, -29.5) * mm, "end": v(-69.15, -34.25) * mm});
            skLineSegment(sketch, "E73.19.9", {"start": v(-69.51, -28.88) * mm, "end": v(-71.06, -33.64) * mm});
            skPoint(sketch, "E74.1.0", {"position": v(-128.54, -8.88) * mm});
            skLineSegment(sketch, "E74.1.1", {"start": v(-130.13, -10.45) * mm, "end": v(-128.59, -15.2) * mm});
            skLineSegment(sketch, "E74.1.2", {"start": v(-128.23, -9.83) * mm, "end": v(-126.68, -14.59) * mm});
            skPoint(sketch, "E74.1.3", {"position": v(-126.38, -15.54) * mm});
            skPoint(sketch, "E74.1.4", {"position": v(-130.44, -9.5) * mm});
            skPoint(sketch, "E74.1.5", {"position": v(-128.28, -16.15) * mm});
            skArc(sketch, "E74.1.6", {"start": v(-128.59, -15.2) * mm, "mid": v(-128.09, -15.79) * mm, "end": v(-127.33, -15.85) * mm});
            skArc(sketch, "E74.1.7", {"start": v(-129.49, -9.19) * mm, "mid": v(-130.07, -9.68) * mm, "end": v(-130.13, -10.45) * mm});
            skArc(sketch, "E74.1.8", {"start": v(-128.23, -9.83) * mm, "mid": v(-128.73, -9.25) * mm, "end": v(-129.49, -9.19) * mm});
            skArc(sketch, "E74.1.9", {"start": v(-127.33, -15.85) * mm, "mid": v(-126.74, -15.35) * mm, "end": v(-126.68, -14.59) * mm});
            skPoint(sketch, "E74.2.0", {"position": v(-134.53, -11.58) * mm});
            skLineSegment(sketch, "E74.2.1", {"start": v(-135.56, -13.57) * mm, "end": v(-132.63, -17.61) * mm});
            skLineSegment(sketch, "E74.2.2", {"start": v(-133.95, -12.4) * mm, "end": v(-131, -16.44) * mm});
            skPoint(sketch, "E74.2.3", {"position": v(-130.42, -17.25) * mm});
            skPoint(sketch, "E74.2.4", {"position": v(-136.15, -12.76) * mm});
            skPoint(sketch, "E74.2.5", {"position": v(-132.04, -18.42) * mm});
            skArc(sketch, "E74.2.6", {"start": v(-132.63, -17.61) * mm, "mid": v(-131.97, -18.01) * mm, "end": v(-131.23, -17.83) * mm});
            skArc(sketch, "E74.2.7", {"start": v(-135.34, -12.17) * mm, "mid": v(-135.74, -12.82) * mm, "end": v(-135.56, -13.57) * mm});
            skArc(sketch, "E74.2.8", {"start": v(-133.95, -12.4) * mm, "mid": v(-134.6, -12) * mm, "end": v(-135.34, -12.17) * mm});
            skArc(sketch, "E74.2.9", {"start": v(-131.23, -17.83) * mm, "mid": v(-130.83, -17.18) * mm, "end": v(-131, -16.44) * mm});
            skPoint(sketch, "E74.3.0", {"position": v(-139.4, -16) * mm});
            skLineSegment(sketch, "E74.3.1", {"start": v(-139.77, -18.21) * mm, "end": v(-135.72, -21.15) * mm});
            skLineSegment(sketch, "E74.3.2", {"start": v(-138.6, -16.6) * mm, "end": v(-134.55, -19.53) * mm});
            skPoint(sketch, "E74.3.3", {"position": v(-133.74, -20.12) * mm});
            skPoint(sketch, "E74.3.4", {"position": v(-140.58, -17.63) * mm});
            skPoint(sketch, "E74.3.5", {"position": v(-134.91, -21.74) * mm});
            skArc(sketch, "E74.3.6", {"start": v(-135.72, -21.15) * mm, "mid": v(-134.98, -21.33) * mm, "end": v(-134.33, -20.93) * mm});
            skArc(sketch, "E74.3.7", {"start": v(-139.99, -16.82) * mm, "mid": v(-140.17, -17.56) * mm, "end": v(-139.77, -18.21) * mm});
            skArc(sketch, "E74.3.8", {"start": v(-138.6, -16.6) * mm, "mid": v(-139.34, -16.42) * mm, "end": v(-139.99, -16.82) * mm});
            skArc(sketch, "E74.3.9", {"start": v(-134.33, -20.93) * mm, "mid": v(-134.15, -20.19) * mm, "end": v(-134.55, -19.53) * mm});
            skPoint(sketch, "E74.4.0", {"position": v(-142.66, -21.72) * mm});
            skLineSegment(sketch, "E74.4.1", {"start": v(-142.33, -23.93) * mm, "end": v(-137.57, -25.48) * mm});
            skLineSegment(sketch, "E74.4.2", {"start": v(-141.71, -22.03) * mm, "end": v(-136.96, -23.57) * mm});
            skPoint(sketch, "E74.4.3", {"position": v(-136, -23.88) * mm});
            skPoint(sketch, "E74.4.4", {"position": v(-143.28, -23.62) * mm});
            skPoint(sketch, "E74.4.5", {"position": v(-136.62, -25.78) * mm});
            skArc(sketch, "E74.4.6", {"start": v(-137.57, -25.48) * mm, "mid": v(-136.81, -25.42) * mm, "end": v(-136.31, -24.83) * mm});
            skArc(sketch, "E74.4.7", {"start": v(-142.97, -22.67) * mm, "mid": v(-142.91, -23.43) * mm, "end": v(-142.33, -23.93) * mm});
            skArc(sketch, "E74.4.8", {"start": v(-141.71, -22.03) * mm, "mid": v(-142.48, -22.09) * mm, "end": v(-142.97, -22.67) * mm});
            skArc(sketch, "E74.4.9", {"start": v(-136.31, -24.83) * mm, "mid": v(-136.37, -24.07) * mm, "end": v(-136.96, -23.57) * mm});
            skPoint(sketch, "E74.5.0", {"position": v(-144, -28.16) * mm});
            skLineSegment(sketch, "E74.5.1", {"start": v(-143, -30.16) * mm, "end": v(-138, -30.16) * mm});
            skLineSegment(sketch, "E74.5.2", {"start": v(-143, -28.16) * mm, "end": v(-138, -28.16) * mm});
            skPoint(sketch, "E74.5.3", {"position": v(-137, -28.16) * mm});
            skPoint(sketch, "E74.5.4", {"position": v(-144, -30.16) * mm});
            skPoint(sketch, "E74.5.5", {"position": v(-137, -30.16) * mm});
            skArc(sketch, "E74.5.6", {"start": v(-138, -30.16) * mm, "mid": v(-137.3, -29.87) * mm, "end": v(-137, -29.16) * mm});
            skArc(sketch, "E74.5.7", {"start": v(-144, -29.16) * mm, "mid": v(-143.7, -29.87) * mm, "end": v(-143, -30.16) * mm});
            skArc(sketch, "E74.5.8", {"start": v(-143, -28.16) * mm, "mid": v(-143.7, -28.45) * mm, "end": v(-144, -29.16) * mm});
            skArc(sketch, "E74.5.9", {"start": v(-137, -29.16) * mm, "mid": v(-137.3, -28.45) * mm, "end": v(-138, -28.16) * mm});
            skPoint(sketch, "E74.6.0", {"position": v(-143.28, -34.7) * mm});
            skLineSegment(sketch, "E74.6.1", {"start": v(-141.71, -36.3) * mm, "end": v(-136.96, -34.75) * mm});
            skLineSegment(sketch, "E74.6.2", {"start": v(-142.33, -34.39) * mm, "end": v(-137.57, -32.84) * mm});
            skPoint(sketch, "E74.6.3", {"position": v(-136.62, -32.54) * mm});
            skPoint(sketch, "E74.6.4", {"position": v(-142.66, -36.6) * mm});
            skPoint(sketch, "E74.6.5", {"position": v(-136, -34.44) * mm});
            skArc(sketch, "E74.6.6", {"start": v(-136.96, -34.75) * mm, "mid": v(-136.37, -34.25) * mm, "end": v(-136.31, -33.49) * mm});
            skArc(sketch, "E74.6.7", {"start": v(-142.97, -35.65) * mm, "mid": v(-142.48, -36.23) * mm, "end": v(-141.71, -36.3) * mm});
            skArc(sketch, "E74.6.8", {"start": v(-142.33, -34.39) * mm, "mid": v(-142.91, -34.89) * mm, "end": v(-142.97, -35.65) * mm});
            skArc(sketch, "E74.6.9", {"start": v(-136.31, -33.49) * mm, "mid": v(-136.81, -32.9) * mm, "end": v(-137.57, -32.84) * mm});
            skPoint(sketch, "E74.7.0", {"position": v(-140.58, -40.7) * mm});
            skLineSegment(sketch, "E74.7.1", {"start": v(-138.6, -41.72) * mm, "end": v(-134.55, -38.79) * mm});
            skLineSegment(sketch, "E74.7.2", {"start": v(-139.77, -40.1) * mm, "end": v(-135.72, -37.17) * mm});
            skPoint(sketch, "E74.7.3", {"position": v(-134.91, -36.58) * mm});
            skPoint(sketch, "E74.7.4", {"position": v(-139.4, -42.31) * mm});
            skPoint(sketch, "E74.7.5", {"position": v(-133.74, -38.2) * mm});
            skArc(sketch, "E74.7.6", {"start": v(-134.55, -38.79) * mm, "mid": v(-134.15, -38.13) * mm, "end": v(-134.33, -37.39) * mm});
            skArc(sketch, "E74.7.7", {"start": v(-139.99, -41.5) * mm, "mid": v(-139.34, -41.9) * mm, "end": v(-138.6, -41.72) * mm});
            skArc(sketch, "E74.7.8", {"start": v(-139.77, -40.1) * mm, "mid": v(-140.17, -40.76) * mm, "end": v(-139.99, -41.5) * mm});
            skArc(sketch, "E74.7.9", {"start": v(-134.33, -37.39) * mm, "mid": v(-134.98, -36.99) * mm, "end": v(-135.72, -37.17) * mm});
            skPoint(sketch, "E74.8.0", {"position": v(-136.15, -45.56) * mm});
            skLineSegment(sketch, "E74.8.1", {"start": v(-133.95, -45.93) * mm, "end": v(-131, -41.88) * mm});
            skLineSegment(sketch, "E74.8.2", {"start": v(-135.56, -44.75) * mm, "end": v(-132.63, -40.7) * mm});
            skPoint(sketch, "E74.8.3", {"position": v(-132.04, -39.9) * mm});
            skPoint(sketch, "E74.8.4", {"position": v(-134.53, -46.74) * mm});
            skPoint(sketch, "E74.8.5", {"position": v(-130.42, -41.07) * mm});
            skArc(sketch, "E74.8.6", {"start": v(-131, -41.88) * mm, "mid": v(-130.83, -41.14) * mm, "end": v(-131.23, -40.49) * mm});
            skArc(sketch, "E74.8.7", {"start": v(-135.34, -46.15) * mm, "mid": v(-134.6, -46.33) * mm, "end": v(-133.95, -45.93) * mm});
            skArc(sketch, "E74.8.8", {"start": v(-135.56, -44.75) * mm, "mid": v(-135.74, -45.5) * mm, "end": v(-135.34, -46.15) * mm});
            skArc(sketch, "E74.8.9", {"start": v(-131.23, -40.49) * mm, "mid": v(-131.97, -40.3) * mm, "end": v(-132.63, -40.7) * mm});
            skPoint(sketch, "E74.9.0", {"position": v(-130.44, -48.82) * mm});
            skLineSegment(sketch, "E74.9.1", {"start": v(-128.23, -48.5) * mm, "end": v(-126.68, -43.73) * mm});
            skLineSegment(sketch, "E74.9.2", {"start": v(-130.13, -47.87) * mm, "end": v(-128.59, -43.12) * mm});
            skPoint(sketch, "E74.9.3", {"position": v(-128.28, -42.17) * mm});
            skPoint(sketch, "E74.9.4", {"position": v(-128.54, -49.44) * mm});
            skPoint(sketch, "E74.9.5", {"position": v(-126.38, -42.78) * mm});
            skArc(sketch, "E74.9.6", {"start": v(-126.68, -43.73) * mm, "mid": v(-126.74, -42.97) * mm, "end": v(-127.33, -42.47) * mm});
            skArc(sketch, "E74.9.7", {"start": v(-129.49, -49.13) * mm, "mid": v(-128.73, -49.07) * mm, "end": v(-128.23, -48.5) * mm});
            skArc(sketch, "E74.9.8", {"start": v(-130.13, -47.87) * mm, "mid": v(-130.07, -48.64) * mm, "end": v(-129.49, -49.13) * mm});
            skArc(sketch, "E74.9.9", {"start": v(-127.33, -42.47) * mm, "mid": v(-128.09, -42.53) * mm, "end": v(-128.59, -43.12) * mm});
            skPoint(sketch, "E74.10.0", {"position": v(-124, -50.16) * mm});
            skLineSegment(sketch, "E74.10.1", {"start": v(-122, -49.16) * mm, "end": v(-122, -44.16) * mm});
            skLineSegment(sketch, "E74.10.2", {"start": v(-124, -49.16) * mm, "end": v(-124, -44.16) * mm});
            skPoint(sketch, "E74.10.3", {"position": v(-124, -43.16) * mm});
            skPoint(sketch, "E74.10.4", {"position": v(-122, -50.16) * mm});
            skPoint(sketch, "E74.10.5", {"position": v(-122, -43.16) * mm});
            skArc(sketch, "E74.10.6", {"start": v(-122, -44.16) * mm, "mid": v(-122.3, -43.45) * mm, "end": v(-123, -43.16) * mm});
            skArc(sketch, "E74.10.7", {"start": v(-123, -50.16) * mm, "mid": v(-122.3, -49.87) * mm, "end": v(-122, -49.16) * mm});
            skArc(sketch, "E74.10.8", {"start": v(-124, -49.16) * mm, "mid": v(-123.7, -49.87) * mm, "end": v(-123, -50.16) * mm});
            skArc(sketch, "E74.10.9", {"start": v(-123, -43.16) * mm, "mid": v(-123.7, -43.45) * mm, "end": v(-124, -44.16) * mm});
            skPoint(sketch, "E74.11.0", {"position": v(-117.46, -49.44) * mm});
            skLineSegment(sketch, "E74.11.1", {"start": v(-115.87, -47.87) * mm, "end": v(-117.41, -43.12) * mm});
            skLineSegment(sketch, "E74.11.2", {"start": v(-117.77, -48.5) * mm, "end": v(-119.32, -43.73) * mm});
            skPoint(sketch, "E74.11.3", {"position": v(-119.62, -42.78) * mm});
            skPoint(sketch, "E74.11.4", {"position": v(-115.56, -48.82) * mm});
            skPoint(sketch, "E74.11.5", {"position": v(-117.72, -42.17) * mm});
            skArc(sketch, "E74.11.6", {"start": v(-117.41, -43.12) * mm, "mid": v(-117.91, -42.53) * mm, "end": v(-118.67, -42.47) * mm});
            skArc(sketch, "E74.11.7", {"start": v(-116.51, -49.13) * mm, "mid": v(-115.93, -48.64) * mm, "end": v(-115.87, -47.87) * mm});
            skArc(sketch, "E74.11.8", {"start": v(-117.77, -48.5) * mm, "mid": v(-117.27, -49.07) * mm, "end": v(-116.51, -49.13) * mm});
            skArc(sketch, "E74.11.9", {"start": v(-118.67, -42.47) * mm, "mid": v(-119.26, -42.97) * mm, "end": v(-119.32, -43.73) * mm});
            skPoint(sketch, "E74.12.0", {"position": v(-111.47, -46.74) * mm});
            skLineSegment(sketch, "E74.12.1", {"start": v(-110.44, -44.75) * mm, "end": v(-113.37, -40.7) * mm});
            skLineSegment(sketch, "E74.12.2", {"start": v(-112.05, -45.93) * mm, "end": v(-115, -41.88) * mm});
            skPoint(sketch, "E74.12.3", {"position": v(-115.58, -41.07) * mm});
            skPoint(sketch, "E74.12.4", {"position": v(-109.85, -45.56) * mm});
            skPoint(sketch, "E74.12.5", {"position": v(-113.96, -39.9) * mm});
            skArc(sketch, "E74.12.6", {"start": v(-113.37, -40.7) * mm, "mid": v(-114.03, -40.3) * mm, "end": v(-114.77, -40.49) * mm});
            skArc(sketch, "E74.12.7", {"start": v(-110.66, -46.15) * mm, "mid": v(-110.26, -45.5) * mm, "end": v(-110.44, -44.75) * mm});
            skArc(sketch, "E74.12.8", {"start": v(-112.05, -45.93) * mm, "mid": v(-111.4, -46.33) * mm, "end": v(-110.66, -46.15) * mm});
            skArc(sketch, "E74.12.9", {"start": v(-114.77, -40.49) * mm, "mid": v(-115.17, -41.14) * mm, "end": v(-115, -41.88) * mm});
            skPoint(sketch, "E74.13.0", {"position": v(-106.6, -42.31) * mm});
            skLineSegment(sketch, "E74.13.1", {"start": v(-106.23, -40.1) * mm, "end": v(-110.28, -37.17) * mm});
            skLineSegment(sketch, "E74.13.2", {"start": v(-107.4, -41.72) * mm, "end": v(-111.45, -38.79) * mm});
            skPoint(sketch, "E74.13.3", {"position": v(-112.26, -38.2) * mm});
            skPoint(sketch, "E74.13.4", {"position": v(-105.42, -40.7) * mm});
            skPoint(sketch, "E74.13.5", {"position": v(-111.09, -36.58) * mm});
            skArc(sketch, "E74.13.6", {"start": v(-110.28, -37.17) * mm, "mid": v(-111.02, -36.99) * mm, "end": v(-111.67, -37.39) * mm});
            skArc(sketch, "E74.13.7", {"start": v(-106.01, -41.5) * mm, "mid": v(-105.83, -40.76) * mm, "end": v(-106.23, -40.1) * mm});
            skArc(sketch, "E74.13.8", {"start": v(-107.4, -41.72) * mm, "mid": v(-106.66, -41.9) * mm, "end": v(-106.01, -41.5) * mm});
            skArc(sketch, "E74.13.9", {"start": v(-111.67, -37.39) * mm, "mid": v(-111.85, -38.13) * mm, "end": v(-111.45, -38.79) * mm});
            skPoint(sketch, "E74.14.0", {"position": v(-103.34, -36.6) * mm});
            skLineSegment(sketch, "E74.14.1", {"start": v(-103.67, -34.39) * mm, "end": v(-108.43, -32.84) * mm});
            skLineSegment(sketch, "E74.14.2", {"start": v(-104.29, -36.3) * mm, "end": v(-109.04, -34.75) * mm});
            skPoint(sketch, "E74.14.3", {"position": v(-110, -34.44) * mm});
            skPoint(sketch, "E74.14.4", {"position": v(-102.72, -34.7) * mm});
            skPoint(sketch, "E74.14.5", {"position": v(-109.38, -32.54) * mm});
            skArc(sketch, "E74.14.6", {"start": v(-108.43, -32.84) * mm, "mid": v(-109.19, -32.9) * mm, "end": v(-109.69, -33.49) * mm});
            skArc(sketch, "E74.14.7", {"start": v(-103.03, -35.65) * mm, "mid": v(-103.09, -34.89) * mm, "end": v(-103.67, -34.39) * mm});
            skArc(sketch, "E74.14.8", {"start": v(-104.29, -36.3) * mm, "mid": v(-103.52, -36.23) * mm, "end": v(-103.03, -35.65) * mm});
            skArc(sketch, "E74.14.9", {"start": v(-109.69, -33.49) * mm, "mid": v(-109.63, -34.25) * mm, "end": v(-109.04, -34.75) * mm});
            skPoint(sketch, "E74.15.0", {"position": v(-102, -30.16) * mm});
            skLineSegment(sketch, "E74.15.1", {"start": v(-103, -28.16) * mm, "end": v(-108, -28.16) * mm});
            skLineSegment(sketch, "E74.15.2", {"start": v(-103, -30.16) * mm, "end": v(-108, -30.16) * mm});
            skPoint(sketch, "E74.15.3", {"position": v(-109, -30.16) * mm});
            skPoint(sketch, "E74.15.4", {"position": v(-102, -28.16) * mm});
            skPoint(sketch, "E74.15.5", {"position": v(-109, -28.16) * mm});
            skArc(sketch, "E74.15.6", {"start": v(-108, -28.16) * mm, "mid": v(-108.7, -28.45) * mm, "end": v(-109, -29.16) * mm});
            skArc(sketch, "E74.15.7", {"start": v(-102, -29.16) * mm, "mid": v(-102.3, -28.45) * mm, "end": v(-103, -28.16) * mm});
            skArc(sketch, "E74.15.8", {"start": v(-103, -30.16) * mm, "mid": v(-102.3, -29.87) * mm, "end": v(-102, -29.16) * mm});
            skArc(sketch, "E74.15.9", {"start": v(-109, -29.16) * mm, "mid": v(-108.7, -29.87) * mm, "end": v(-108, -30.16) * mm});
            skPoint(sketch, "E74.16.0", {"position": v(-102.72, -23.62) * mm});
            skLineSegment(sketch, "E74.16.1", {"start": v(-104.29, -22.03) * mm, "end": v(-109.04, -23.57) * mm});
            skLineSegment(sketch, "E74.16.2", {"start": v(-103.67, -23.93) * mm, "end": v(-108.43, -25.48) * mm});
            skPoint(sketch, "E74.16.3", {"position": v(-109.38, -25.78) * mm});
            skPoint(sketch, "E74.16.4", {"position": v(-103.34, -21.72) * mm});
            skPoint(sketch, "E74.16.5", {"position": v(-110, -23.88) * mm});
            skArc(sketch, "E74.16.6", {"start": v(-109.04, -23.57) * mm, "mid": v(-109.63, -24.07) * mm, "end": v(-109.69, -24.83) * mm});
            skArc(sketch, "E74.16.7", {"start": v(-103.03, -22.67) * mm, "mid": v(-103.52, -22.09) * mm, "end": v(-104.29, -22.03) * mm});
            skArc(sketch, "E74.16.8", {"start": v(-103.67, -23.93) * mm, "mid": v(-103.09, -23.43) * mm, "end": v(-103.03, -22.67) * mm});
            skArc(sketch, "E74.16.9", {"start": v(-109.69, -24.83) * mm, "mid": v(-109.19, -25.42) * mm, "end": v(-108.43, -25.48) * mm});
            skPoint(sketch, "E74.17.0", {"position": v(-105.42, -17.63) * mm});
            skLineSegment(sketch, "E74.17.1", {"start": v(-107.4, -16.6) * mm, "end": v(-111.45, -19.53) * mm});
            skLineSegment(sketch, "E74.17.2", {"start": v(-106.23, -18.21) * mm, "end": v(-110.28, -21.15) * mm});
            skPoint(sketch, "E74.17.3", {"position": v(-111.09, -21.74) * mm});
            skPoint(sketch, "E74.17.4", {"position": v(-106.6, -16) * mm});
            skPoint(sketch, "E74.17.5", {"position": v(-112.26, -20.12) * mm});
            skArc(sketch, "E74.17.6", {"start": v(-111.45, -19.53) * mm, "mid": v(-111.85, -20.19) * mm, "end": v(-111.67, -20.93) * mm});
            skArc(sketch, "E74.17.7", {"start": v(-106.01, -16.82) * mm, "mid": v(-106.66, -16.42) * mm, "end": v(-107.4, -16.6) * mm});
            skArc(sketch, "E74.17.8", {"start": v(-106.23, -18.21) * mm, "mid": v(-105.83, -17.56) * mm, "end": v(-106.01, -16.82) * mm});
            skArc(sketch, "E74.17.9", {"start": v(-111.67, -20.93) * mm, "mid": v(-111.02, -21.33) * mm, "end": v(-110.28, -21.15) * mm});
            skPoint(sketch, "E74.18.0", {"position": v(-109.85, -12.76) * mm});
            skLineSegment(sketch, "E74.18.1", {"start": v(-112.05, -12.4) * mm, "end": v(-115, -16.44) * mm});
            skLineSegment(sketch, "E74.18.2", {"start": v(-110.44, -13.57) * mm, "end": v(-113.37, -17.61) * mm});
            skPoint(sketch, "E74.18.3", {"position": v(-113.96, -18.42) * mm});
            skPoint(sketch, "E74.18.4", {"position": v(-111.47, -11.58) * mm});
            skPoint(sketch, "E74.18.5", {"position": v(-115.58, -17.25) * mm});
            skArc(sketch, "E74.18.6", {"start": v(-115, -16.44) * mm, "mid": v(-115.17, -17.18) * mm, "end": v(-114.77, -17.83) * mm});
            skArc(sketch, "E74.18.7", {"start": v(-110.66, -12.17) * mm, "mid": v(-111.4, -12) * mm, "end": v(-112.05, -12.4) * mm});
            skArc(sketch, "E74.18.8", {"start": v(-110.44, -13.57) * mm, "mid": v(-110.26, -12.82) * mm, "end": v(-110.66, -12.17) * mm});
            skArc(sketch, "E74.18.9", {"start": v(-114.77, -17.83) * mm, "mid": v(-114.03, -18.01) * mm, "end": v(-113.37, -17.61) * mm});
            skPoint(sketch, "E74.19.0", {"position": v(-115.56, -9.5) * mm});
            skLineSegment(sketch, "E74.19.1", {"start": v(-117.77, -9.83) * mm, "end": v(-119.32, -14.59) * mm});
            skLineSegment(sketch, "E74.19.2", {"start": v(-115.87, -10.45) * mm, "end": v(-117.41, -15.2) * mm});
            skPoint(sketch, "E74.19.3", {"position": v(-117.72, -16.15) * mm});
            skPoint(sketch, "E74.19.4", {"position": v(-117.46, -8.88) * mm});
            skPoint(sketch, "E74.19.5", {"position": v(-119.62, -15.54) * mm});
            skArc(sketch, "E74.19.6", {"start": v(-119.32, -14.59) * mm, "mid": v(-119.26, -15.35) * mm, "end": v(-118.67, -15.85) * mm});
            skArc(sketch, "E74.19.7", {"start": v(-116.51, -9.19) * mm, "mid": v(-117.27, -9.25) * mm, "end": v(-117.77, -9.83) * mm});
            skArc(sketch, "E74.19.8", {"start": v(-115.87, -10.45) * mm, "mid": v(-115.93, -9.68) * mm, "end": v(-116.51, -9.19) * mm});
            skArc(sketch, "E74.19.9", {"start": v(-118.67, -15.85) * mm, "mid": v(-117.91, -15.79) * mm, "end": v(-117.41, -15.2) * mm});
            skSolve(sketch);
        }
        {
            var Q0;
            Q0=makeQuery(id+"F0.imprint","IMPRINT",FACE,{"disambiguationData":[TD([[makeQuery(id+"F0.imprint","IMPRINT",EDGE,{"derivedFrom":sQuery(id+"F0.wireOp",EDGE,"E0.bottom")}),-1.0]])]});
            extrude(context, id + "F1", {"entities" : qUnion([Q0]), "oppositeDirection" : true, "depth" : 3 * mm});
        }
        {
            var Q0;
            Q0=sQuery(id+"F0.wireOp",VERTEX,"E31");
            var Q1;
            Q1=sQuery(id+"F0.wireOp",VERTEX,"E32");
            var Q2;
            Q2=sQuery(id+"F0.wireOp",VERTEX,"E34");
            var Q3;
            Q3=sQuery(id+"F0.wireOp",VERTEX,"E35");
            var Q4;
            Q4=sQuery(id+"F0.wireOp",VERTEX,"E36");
            var Q5;
            Q5=sQuery(id+"F0.wireOp",VERTEX,"E37");
            var Q6;
            Q6=sQuery(id+"F0.wireOp",VERTEX,"E38");
            var Q7;
            Q7=sQuery(id+"F0.wireOp",VERTEX,"E33");
            var Q8;
            Q8=makeQuery(id+"F1.opExtrude","SWEPT_BODY",BODY,{"disambiguationData":[OSD([sQuery(id+"F0.wireOp",EDGE,"E0.bottom"),sQuery(id+"F0.wireOp",EDGE,"E0.top"),sQuery(id+"F0.wireOp",EDGE,"E0.left"),sQuery(id+"F0.wireOp",EDGE,"E0.right"),sQuery(id+"F0.wireOp",EDGE,"E10"),sQuery(id+"F0.wireOp",EDGE,"E11"),sQuery(id+"F0.wireOp",EDGE,"E12"),sQuery(id+"F0.wireOp",EDGE,"E13"),sQuery(id+"F0.wireOp",EDGE,"E14"),sQuery(id+"F0.wireOp",EDGE,"E15"),sQuery(id+"F0.wireOp",EDGE,"E16.bottom"),sQuery(id+"F0.wireOp",EDGE,"E16.top"),sQuery(id+"F0.wireOp",EDGE,"E16.left"),sQuery(id+"F0.wireOp",EDGE,"E16.right"),sQuery(id+"F0.wireOp",EDGE,"E21"),sQuery(id+"F0.wireOp",EDGE,"E22"),sQuery(id+"F0.wireOp",EDGE,"E23"),sQuery(id+"F0.wireOp",EDGE,"E24")])]});
            hole(context, id + "F2", {"style" : HoleStyle.C_BORE, "endStyle" : HoleEndStyle.THROUGH, "holeDiameter" : 3.5 * mm, "cBoreDiameter" : 6.5 * mm, "cBoreDepth" : 2 * mm, "startFromSketch" : true, "locations" : qUnion([Q0, Q1, Q2, Q3, Q4, Q5, Q6, Q7]), "scope" : qUnion([Q8]), "isTappedThrough" : true});
        }
        {
            var Q0;
            Q0=makeQuery(id+"F1.opExtrude","CAP_FACE",FACE,{"disambiguationData":[OSD([sQuery(id+"F0.wireOp",EDGE,"E0.bottom"),sQuery(id+"F0.wireOp",EDGE,"E0.top"),sQuery(id+"F0.wireOp",EDGE,"E0.left"),sQuery(id+"F0.wireOp",EDGE,"E0.right"),sQuery(id+"F0.wireOp",EDGE,"E10"),sQuery(id+"F0.wireOp",EDGE,"E11"),sQuery(id+"F0.wireOp",EDGE,"E12"),sQuery(id+"F0.wireOp",EDGE,"E13"),sQuery(id+"F0.wireOp",EDGE,"E14"),sQuery(id+"F0.wireOp",EDGE,"E15"),sQuery(id+"F0.wireOp",EDGE,"E16.bottom"),sQuery(id+"F0.wireOp",EDGE,"E16.top"),sQuery(id+"F0.wireOp",EDGE,"E16.left"),sQuery(id+"F0.wireOp",EDGE,"E16.right"),sQuery(id+"F0.wireOp",EDGE,"E21"),sQuery(id+"F0.wireOp",EDGE,"E22"),sQuery(id+"F0.wireOp",EDGE,"E23"),sQuery(id+"F0.wireOp",EDGE,"E24")])],"isStart":true});
            var sketch = newSketch(context, id + "F3", { "sketchPlane" : qUnion([Q0])});
            skLineSegment(sketch, "E75", {"start": v(49.55, 81.28) * mm, "end": v(140.1, 81.28) * mm, "construction": true});
            skLineSegment(sketch, "E76", {"start": v(55.93, -81.28) * mm, "end": v(143.02, -81.28) * mm, "construction": true});
            skLineSegment(sketch, "E77", {"start": v(113, 117.74) * mm, "end": v(113, -66.7) * mm, "construction": true});
            skLineSegment(sketch, "E78", {"start": v(61, 115.87) * mm, "end": v(61, -81.28) * mm, "construction": true});
            skPoint(sketch, "E79", {"position": v(61, 81.28) * mm});
            skPoint(sketch, "E80", {"position": v(113, 81.28) * mm});
            skPoint(sketch, "E81", {"position": v(61, -81.28) * mm});
            skPoint(sketch, "E82", {"position": v(113, -81.28) * mm});
            skSolve(sketch);
        }
        {
            var Q0;
            Q0=sQuery(id+"F3.wireOp",VERTEX,"E79");
            var Q1;
            Q1=sQuery(id+"F3.wireOp",VERTEX,"E80");
            var Q2;
            Q2=sQuery(id+"F3.wireOp",VERTEX,"E81");
            var Q3;
            Q3=sQuery(id+"F3.wireOp",VERTEX,"E82");
            var Q4;
            Q4=makeQuery(id+"F1.opExtrude","SWEPT_BODY",BODY,{"disambiguationData":[OSD([sQuery(id+"F0.wireOp",EDGE,"E0.bottom"),sQuery(id+"F0.wireOp",EDGE,"E0.top"),sQuery(id+"F0.wireOp",EDGE,"E0.left"),sQuery(id+"F0.wireOp",EDGE,"E0.right"),sQuery(id+"F0.wireOp",EDGE,"E10"),sQuery(id+"F0.wireOp",EDGE,"E11"),sQuery(id+"F0.wireOp",EDGE,"E12"),sQuery(id+"F0.wireOp",EDGE,"E13"),sQuery(id+"F0.wireOp",EDGE,"E14"),sQuery(id+"F0.wireOp",EDGE,"E15"),sQuery(id+"F0.wireOp",EDGE,"E16.bottom"),sQuery(id+"F0.wireOp",EDGE,"E16.top"),sQuery(id+"F0.wireOp",EDGE,"E16.left"),sQuery(id+"F0.wireOp",EDGE,"E16.right"),sQuery(id+"F0.wireOp",EDGE,"E21"),sQuery(id+"F0.wireOp",EDGE,"E22"),sQuery(id+"F0.wireOp",EDGE,"E23"),sQuery(id+"F0.wireOp",EDGE,"E24")])]});
            hole(context, id + "F4", {"style" : HoleStyle.C_BORE, "endStyle" : HoleEndStyle.THROUGH, "holeDiameter" : 3.5 * mm, "cBoreDiameter" : 6.5 * mm, "cBoreDepth" : 2 * mm, "startFromSketch" : true, "locations" : qUnion([Q0, Q1, Q2, Q3]), "scope" : qUnion([Q4]), "isTappedThrough" : true});
        }
        {
            var Q0;
            Q0=makeQuery(id+"F1.opExtrude","CAP_FACE",FACE,{"disambiguationData":[OSD([sQuery(id+"F0.wireOp",EDGE,"E0.bottom"),sQuery(id+"F0.wireOp",EDGE,"E0.top"),sQuery(id+"F0.wireOp",EDGE,"E0.left"),sQuery(id+"F0.wireOp",EDGE,"E0.right"),sQuery(id+"F0.wireOp",EDGE,"E10"),sQuery(id+"F0.wireOp",EDGE,"E11"),sQuery(id+"F0.wireOp",EDGE,"E12"),sQuery(id+"F0.wireOp",EDGE,"E13"),sQuery(id+"F0.wireOp",EDGE,"E14"),sQuery(id+"F0.wireOp",EDGE,"E15"),sQuery(id+"F0.wireOp",EDGE,"E16.bottom"),sQuery(id+"F0.wireOp",EDGE,"E16.top"),sQuery(id+"F0.wireOp",EDGE,"E16.left"),sQuery(id+"F0.wireOp",EDGE,"E16.right"),sQuery(id+"F0.wireOp",EDGE,"E21"),sQuery(id+"F0.wireOp",EDGE,"E22"),sQuery(id+"F0.wireOp",EDGE,"E23"),sQuery(id+"F0.wireOp",EDGE,"E24")])],"isStart":true});
            var sketch = newSketch(context, id + "F5", { "sketchPlane" : qUnion([Q0])});
            skLineSegment(sketch, "E83", {"start": v(50, 109.2) * mm, "end": v(50, 0) * mm, "construction": true});
            skLineSegment(sketch, "E84", {"start": v(55, 98.56) * mm, "end": v(55, 15.48) * mm, "construction": true});
            skLineSegment(sketch, "E85", {"start": v(30.25, 96) * mm, "end": v(146.83, 96) * mm, "construction": true});
            skLineSegment(sketch, "E86", {"start": v(124, 107.28) * mm, "end": v(124, 27.3) * mm, "construction": true});
            skLineSegment(sketch, "E87", {"start": v(119, 52.5) * mm, "end": v(119, 25.83) * mm, "construction": true});
            skLineSegment(sketch, "E88", {"start": v(48.72, 90) * mm, "end": v(127.69, 90) * mm, "construction": true});
            skLineSegment(sketch, "E89", {"start": v(47.08, 84) * mm, "end": v(128.67, 84) * mm, "construction": true});
            skLineSegment(sketch, "E90", {"start": v(46.43, 78) * mm, "end": v(128.5, 78) * mm, "construction": true});
            skLineSegment(sketch, "E91", {"start": v(46.5, 60) * mm, "end": v(127.85, 60) * mm, "construction": true});
            skLineSegment(sketch, "E92", {"start": v(47.82, 72) * mm, "end": v(127.85, 72) * mm, "construction": true});
            skLineSegment(sketch, "E93", {"start": v(47.4, 66) * mm, "end": v(127.68, 66) * mm, "construction": true});
            skLineSegment(sketch, "E94.bottom", {"start": v(122.5, 88.5) * mm, "end": v(51.5, 88.5) * mm});
            skLineSegment(sketch, "E94.top", {"start": v(122.5, 91.5) * mm, "end": v(51.5, 91.5) * mm});
            skLineSegment(sketch, "E94.left", {"start": v(124, 90) * mm, "end": v(124, 90) * mm});
            skLineSegment(sketch, "E94.right", {"start": v(50, 90) * mm, "end": v(50, 90) * mm});
            skPoint(sketch, "E94.middle", {"position": v(87, 90) * mm});
            skLineSegment(sketch, "E95.bottom", {"start": v(122.5, 82.5) * mm, "end": v(118.7, 82.5) * mm});
            skLineSegment(sketch, "E95.top", {"start": v(122.5, 85.5) * mm, "end": v(118.7, 85.5) * mm});
            skLineSegment(sketch, "E95.left", {"start": v(124, 84) * mm, "end": v(124, 84) * mm});
            skLineSegment(sketch, "E95.right", {"start": v(50, 84) * mm, "end": v(50, 84) * mm});
            skPoint(sketch, "E95.middle", {"position": v(87, 84) * mm});
            skLineSegment(sketch, "E96.bottom", {"start": v(122.5, 76.5) * mm, "end": v(118.7, 76.5) * mm});
            skLineSegment(sketch, "E96.top", {"start": v(122.5, 79.5) * mm, "end": v(118.7, 79.5) * mm});
            skLineSegment(sketch, "E96.left", {"start": v(124, 78) * mm, "end": v(124, 78) * mm});
            skLineSegment(sketch, "E96.right", {"start": v(50, 78) * mm, "end": v(50, 78) * mm});
            skPoint(sketch, "E96.middle", {"position": v(87, 78) * mm});
            skLineSegment(sketch, "E97.bottom", {"start": v(122.5, 70.5) * mm, "end": v(51.5, 70.5) * mm});
            skLineSegment(sketch, "E97.top", {"start": v(122.5, 73.5) * mm, "end": v(51.5, 73.5) * mm});
            skLineSegment(sketch, "E97.left", {"start": v(124, 72) * mm, "end": v(124, 72) * mm});
            skLineSegment(sketch, "E97.right", {"start": v(50, 72) * mm, "end": v(50, 72) * mm});
            skPoint(sketch, "E97.middle", {"position": v(87, 72) * mm});
            skLineSegment(sketch, "E98.bottom", {"start": v(122.5, 64.5) * mm, "end": v(51.5, 64.5) * mm});
            skLineSegment(sketch, "E98.top", {"start": v(122.5, 67.5) * mm, "end": v(51.5, 67.5) * mm});
            skLineSegment(sketch, "E98.left", {"start": v(124, 66) * mm, "end": v(124, 66) * mm});
            skLineSegment(sketch, "E98.right", {"start": v(50, 66) * mm, "end": v(50, 66) * mm});
            skPoint(sketch, "E98.middle", {"position": v(87, 66) * mm});
            skLineSegment(sketch, "E99.bottom", {"start": v(122.5, 58.5) * mm, "end": v(51.5, 58.5) * mm});
            skLineSegment(sketch, "E99.top", {"start": v(122.5, 61.5) * mm, "end": v(51.5, 61.5) * mm});
            skLineSegment(sketch, "E99.left", {"start": v(124, 60) * mm, "end": v(124, 60) * mm});
            skLineSegment(sketch, "E99.right", {"start": v(50, 60) * mm, "end": v(50, 60) * mm});
            skPoint(sketch, "E99.middle", {"position": v(87, 60) * mm});
            skLineSegment(sketch, "E100.bottom", {"start": v(51.5, 97.5) * mm, "end": v(122.5, 97.5) * mm});
            skLineSegment(sketch, "E100.top", {"start": v(51.5, 94.5) * mm, "end": v(122.5, 94.5) * mm});
            skLineSegment(sketch, "E100.left", {"start": v(50, 96) * mm, "end": v(50, 96) * mm});
            skLineSegment(sketch, "E100.right", {"start": v(124, 96) * mm, "end": v(124, 96) * mm});
            skPoint(sketch, "E101.visualSharp", {"position": v(50, 97.5) * mm});
            skArc(sketch, "E101.filletArc", {"start": v(51.5, 97.5) * mm, "mid": v(50.44, 97.06) * mm, "end": v(50, 96) * mm});
            skPoint(sketch, "E102.visualSharp", {"position": v(50, 94.5) * mm});
            skArc(sketch, "E102.filletArc", {"start": v(50, 96) * mm, "mid": v(50.44, 94.94) * mm, "end": v(51.5, 94.5) * mm});
            skPoint(sketch, "E103.visualSharp", {"position": v(50, 91.5) * mm});
            skArc(sketch, "E103.filletArc", {"start": v(51.5, 91.5) * mm, "mid": v(50.44, 91.06) * mm, "end": v(50, 90) * mm});
            skPoint(sketch, "E104.visualSharp", {"position": v(50, 85.5) * mm});
            skArc(sketch, "E104.filletArc", {"start": v(51.5, 85.5) * mm, "mid": v(50.44, 85.06) * mm, "end": v(50, 84) * mm});
            skPoint(sketch, "E105.visualSharp", {"position": v(50, 88.5) * mm});
            skArc(sketch, "E105.filletArc", {"start": v(50, 90) * mm, "mid": v(50.44, 88.94) * mm, "end": v(51.5, 88.5) * mm});
            skPoint(sketch, "E106.visualSharp", {"position": v(50, 82.5) * mm});
            skArc(sketch, "E106.filletArc", {"start": v(50, 84) * mm, "mid": v(50.44, 82.94) * mm, "end": v(51.5, 82.5) * mm});
            skPoint(sketch, "E107.visualSharp", {"position": v(50, 79.5) * mm});
            skArc(sketch, "E107.filletArc", {"start": v(51.5, 79.5) * mm, "mid": v(50.44, 79.06) * mm, "end": v(50, 78) * mm});
            skPoint(sketch, "E108.visualSharp", {"position": v(50, 76.5) * mm});
            skArc(sketch, "E108.filletArc", {"start": v(50, 78) * mm, "mid": v(50.44, 76.94) * mm, "end": v(51.5, 76.5) * mm});
            skPoint(sketch, "E109.visualSharp", {"position": v(50, 73.5) * mm});
            skArc(sketch, "E109.filletArc", {"start": v(51.5, 73.5) * mm, "mid": v(50.44, 73.06) * mm, "end": v(50, 72) * mm});
            skPoint(sketch, "E110.visualSharp", {"position": v(50, 70.5) * mm});
            skArc(sketch, "E110.filletArc", {"start": v(50, 72) * mm, "mid": v(50.44, 70.94) * mm, "end": v(51.5, 70.5) * mm});
            skPoint(sketch, "E111.visualSharp", {"position": v(50, 67.5) * mm});
            skArc(sketch, "E111.filletArc", {"start": v(51.5, 67.5) * mm, "mid": v(50.44, 67.06) * mm, "end": v(50, 66) * mm});
            skPoint(sketch, "E112.visualSharp", {"position": v(50, 64.5) * mm});
            skArc(sketch, "E112.filletArc", {"start": v(50, 66) * mm, "mid": v(50.44, 64.94) * mm, "end": v(51.5, 64.5) * mm});
            skPoint(sketch, "E113.visualSharp", {"position": v(50, 61.5) * mm});
            skArc(sketch, "E113.filletArc", {"start": v(51.5, 61.5) * mm, "mid": v(50.44, 61.06) * mm, "end": v(50, 60) * mm});
            skPoint(sketch, "E114.visualSharp", {"position": v(50, 58.5) * mm});
            skArc(sketch, "E114.filletArc", {"start": v(50, 60) * mm, "mid": v(50.44, 58.94) * mm, "end": v(51.5, 58.5) * mm});
            skPoint(sketch, "E115.visualSharp", {"position": v(124, 97.5) * mm});
            skArc(sketch, "E115.filletArc", {"start": v(124, 96) * mm, "mid": v(123.56, 97.06) * mm, "end": v(122.5, 97.5) * mm});
            skPoint(sketch, "E116.visualSharp", {"position": v(124, 94.5) * mm});
            skArc(sketch, "E116.filletArc", {"start": v(122.5, 94.5) * mm, "mid": v(123.56, 94.94) * mm, "end": v(124, 96) * mm});
            skPoint(sketch, "E117.visualSharp", {"position": v(124, 91.5) * mm});
            skArc(sketch, "E117.filletArc", {"start": v(124, 90) * mm, "mid": v(123.56, 91.06) * mm, "end": v(122.5, 91.5) * mm});
            skPoint(sketch, "E118.visualSharp", {"position": v(124, 88.5) * mm});
            skArc(sketch, "E118.filletArc", {"start": v(122.5, 88.5) * mm, "mid": v(123.56, 88.94) * mm, "end": v(124, 90) * mm});
            skPoint(sketch, "E119.visualSharp", {"position": v(124, 85.5) * mm});
            skArc(sketch, "E119.filletArc", {"start": v(124, 84) * mm, "mid": v(123.56, 85.06) * mm, "end": v(122.5, 85.5) * mm});
            skPoint(sketch, "E120.visualSharp", {"position": v(124, 82.5) * mm});
            skArc(sketch, "E120.filletArc", {"start": v(122.5, 82.5) * mm, "mid": v(123.56, 82.94) * mm, "end": v(124, 84) * mm});
            skPoint(sketch, "E121.visualSharp", {"position": v(124, 79.5) * mm});
            skArc(sketch, "E121.filletArc", {"start": v(124, 78) * mm, "mid": v(123.56, 79.06) * mm, "end": v(122.5, 79.5) * mm});
            skPoint(sketch, "E122.visualSharp", {"position": v(124, 76.5) * mm});
            skArc(sketch, "E122.filletArc", {"start": v(122.5, 76.5) * mm, "mid": v(123.56, 76.94) * mm, "end": v(124, 78) * mm});
            skPoint(sketch, "E123.visualSharp", {"position": v(124, 73.5) * mm});
            skArc(sketch, "E123.filletArc", {"start": v(124, 72) * mm, "mid": v(123.56, 73.06) * mm, "end": v(122.5, 73.5) * mm});
            skPoint(sketch, "E124.visualSharp", {"position": v(124, 70.5) * mm});
            skArc(sketch, "E124.filletArc", {"start": v(122.5, 70.5) * mm, "mid": v(123.56, 70.94) * mm, "end": v(124, 72) * mm});
            skPoint(sketch, "E125.visualSharp", {"position": v(124, 67.5) * mm});
            skArc(sketch, "E125.filletArc", {"start": v(124, 66) * mm, "mid": v(123.56, 67.06) * mm, "end": v(122.5, 67.5) * mm});
            skPoint(sketch, "E126.visualSharp", {"position": v(124, 64.5) * mm});
            skArc(sketch, "E126.filletArc", {"start": v(122.5, 64.5) * mm, "mid": v(123.56, 64.94) * mm, "end": v(124, 66) * mm});
            skPoint(sketch, "E127.visualSharp", {"position": v(124, 61.5) * mm});
            skArc(sketch, "E127.filletArc", {"start": v(124, 60) * mm, "mid": v(123.56, 61.06) * mm, "end": v(122.5, 61.5) * mm});
            skPoint(sketch, "E128.visualSharp", {"position": v(124, 58.5) * mm});
            skArc(sketch, "E128.filletArc", {"start": v(122.5, 58.5) * mm, "mid": v(123.56, 58.94) * mm, "end": v(124, 60) * mm});
            skArc(sketch, "E129.MirrorCS", {"start": v(51.5, -73.5) * mm, "mid": v(50.44, -73.06) * mm, "end": v(50, -72) * mm});
            skArc(sketch, "E130.MirrorCS", {"start": v(50, -90) * mm, "mid": v(50.44, -88.94) * mm, "end": v(51.5, -88.5) * mm});
            skArc(sketch, "E131.MirrorCS", {"start": v(50, -72) * mm, "mid": v(50.44, -70.94) * mm, "end": v(51.5, -70.5) * mm});
            skArc(sketch, "E132.MirrorCS", {"start": v(51.5, -91.5) * mm, "mid": v(50.44, -91.06) * mm, "end": v(50, -90) * mm});
            skArc(sketch, "E133.MirrorCS", {"start": v(50, -60) * mm, "mid": v(50.44, -58.94) * mm, "end": v(51.5, -58.5) * mm});
            skArc(sketch, "E134.MirrorCS", {"start": v(50, -96) * mm, "mid": v(50.44, -94.94) * mm, "end": v(51.5, -94.5) * mm});
            skArc(sketch, "E135.MirrorCS", {"start": v(50, -66) * mm, "mid": v(50.44, -64.94) * mm, "end": v(51.5, -64.5) * mm});
            skArc(sketch, "E136.MirrorCS", {"start": v(51.5, -67.5) * mm, "mid": v(50.44, -67.06) * mm, "end": v(50, -66) * mm});
            skArc(sketch, "E137.MirrorCS", {"start": v(51.5, -97.5) * mm, "mid": v(50.44, -97.06) * mm, "end": v(50, -96) * mm});
            skArc(sketch, "E138.MirrorCS", {"start": v(51.5, -61.5) * mm, "mid": v(50.44, -61.06) * mm, "end": v(50, -60) * mm});
            skArc(sketch, "E139.MirrorCS", {"start": v(124, -66) * mm, "mid": v(123.56, -67.06) * mm, "end": v(122.5, -67.5) * mm});
            skArc(sketch, "E140.MirrorCS", {"start": v(122.5, -64.5) * mm, "mid": v(123.56, -64.94) * mm, "end": v(124, -66) * mm});
            skArc(sketch, "E141.MirrorCS", {"start": v(122.5, -70.5) * mm, "mid": v(123.56, -70.94) * mm, "end": v(124, -72) * mm});
            skArc(sketch, "E142.MirrorCS", {"start": v(124, -90) * mm, "mid": v(123.56, -91.06) * mm, "end": v(122.5, -91.5) * mm});
            skArc(sketch, "E143.MirrorCS", {"start": v(122.5, -88.5) * mm, "mid": v(123.56, -88.94) * mm, "end": v(124, -90) * mm});
            skArc(sketch, "E144.MirrorCS", {"start": v(124, -72) * mm, "mid": v(123.56, -73.06) * mm, "end": v(122.5, -73.5) * mm});
            skArc(sketch, "E145.MirrorCS", {"start": v(122.5, -58.5) * mm, "mid": v(123.56, -58.94) * mm, "end": v(124, -60) * mm});
            skArc(sketch, "E146.MirrorCS", {"start": v(122.5, -94.5) * mm, "mid": v(123.56, -94.94) * mm, "end": v(124, -96) * mm});
            skArc(sketch, "E147.MirrorCS", {"start": v(124, -96) * mm, "mid": v(123.56, -97.06) * mm, "end": v(122.5, -97.5) * mm});
            skArc(sketch, "E148.MirrorCS", {"start": v(124, -60) * mm, "mid": v(123.56, -61.06) * mm, "end": v(122.5, -61.5) * mm});
            skPoint(sketch, "E149.MirrorP", {"position": v(50, -88.5) * mm});
            skPoint(sketch, "E150.MirrorP", {"position": v(50, -73.5) * mm});
            skPoint(sketch, "E151.MirrorP", {"position": v(124, -67.5) * mm});
            skPoint(sketch, "E152.MirrorP", {"position": v(124, -91.5) * mm});
            skPoint(sketch, "E153.MirrorP", {"position": v(124, -61.5) * mm});
            skPoint(sketch, "E154.MirrorP", {"position": v(50, -91.5) * mm});
            skPoint(sketch, "E155.MirrorP", {"position": v(124, -70.5) * mm});
            skPoint(sketch, "E156.MirrorP", {"position": v(124, -94.5) * mm});
            skPoint(sketch, "E157.MirrorP", {"position": v(50, -67.5) * mm});
            skPoint(sketch, "E158.MirrorP", {"position": v(50, -64.5) * mm});
            skPoint(sketch, "E159.MirrorP", {"position": v(124, -64.5) * mm});
            skPoint(sketch, "E160.MirrorP", {"position": v(50, -94.5) * mm});
            skPoint(sketch, "E161.MirrorP", {"position": v(124, -88.5) * mm});
            skPoint(sketch, "E162.MirrorP", {"position": v(124, -73.5) * mm});
            skPoint(sketch, "E163.MirrorP", {"position": v(50, -70.5) * mm});
            skPoint(sketch, "E164.MirrorP", {"position": v(50, -61.5) * mm});
            skLineSegment(sketch, "E165.MirrorCS", {"start": v(122.5, -70.5) * mm, "end": v(51.5, -70.5) * mm});
            skLineSegment(sketch, "E166.MirrorCS", {"start": v(122.5, -61.5) * mm, "end": v(51.5, -61.5) * mm});
            skLineSegment(sketch, "E167.MirrorCS", {"start": v(50, -96) * mm, "end": v(50, -96) * mm});
            skPoint(sketch, "E168.MirrorP", {"position": v(87, -72) * mm});
            skLineSegment(sketch, "E169.MirrorCS", {"start": v(122.5, -73.5) * mm, "end": v(51.5, -73.5) * mm});
            skLineSegment(sketch, "E170.MirrorCS", {"start": v(124, -72) * mm, "end": v(124, -72) * mm});
            skLineSegment(sketch, "E171.MirrorCS", {"start": v(50, -90) * mm, "end": v(50, -90) * mm});
            skLineSegment(sketch, "E172.MirrorCS", {"start": v(50, -60) * mm, "end": v(50, -60) * mm});
            skPoint(sketch, "E173.MirrorP", {"position": v(124, -97.5) * mm});
            skLineSegment(sketch, "E174.MirrorCS", {"start": v(46.5, -60) * mm, "end": v(127.85, -60) * mm, "construction": true});
            skLineSegment(sketch, "E175.MirrorCS", {"start": v(124, -60) * mm, "end": v(124, -60) * mm});
            skPoint(sketch, "E176.MirrorP", {"position": v(87, -90) * mm});
            skPoint(sketch, "E177.MirrorP", {"position": v(87, -60) * mm});
            skLineSegment(sketch, "E178.MirrorCS", {"start": v(124, -66) * mm, "end": v(124, -66) * mm});
            skPoint(sketch, "E179.MirrorP", {"position": v(124, -58.5) * mm});
            skLineSegment(sketch, "E180.MirrorCS", {"start": v(48.72, -90) * mm, "end": v(127.69, -90) * mm, "construction": true});
            skLineSegment(sketch, "E181.MirrorCS", {"start": v(122.5, -64.5) * mm, "end": v(51.5, -64.5) * mm});
            skLineSegment(sketch, "E182.MirrorCS", {"start": v(122.5, -91.5) * mm, "end": v(51.5, -91.5) * mm});
            skLineSegment(sketch, "E183.MirrorCS", {"start": v(47.4, -66) * mm, "end": v(127.68, -66) * mm, "construction": true});
            skLineSegment(sketch, "E184.MirrorCS", {"start": v(47.82, -72) * mm, "end": v(127.85, -72) * mm, "construction": true});
            skLineSegment(sketch, "E185.MirrorCS", {"start": v(122.5, -88.5) * mm, "end": v(51.5, -88.5) * mm});
            skPoint(sketch, "E186.MirrorP", {"position": v(50, -58.5) * mm});
            skLineSegment(sketch, "E187.MirrorCS", {"start": v(50, -66) * mm, "end": v(50, -66) * mm});
            skLineSegment(sketch, "E188.MirrorCS", {"start": v(51.5, -97.5) * mm, "end": v(122.5, -97.5) * mm});
            skLineSegment(sketch, "E189.MirrorCS", {"start": v(124, -90) * mm, "end": v(124, -90) * mm});
            skPoint(sketch, "E190.MirrorP", {"position": v(87, -66) * mm});
            skLineSegment(sketch, "E191.MirrorCS", {"start": v(124, -96) * mm, "end": v(124, -96) * mm});
            skLineSegment(sketch, "E192.MirrorCS", {"start": v(122.5, -67.5) * mm, "end": v(51.5, -67.5) * mm});
            skLineSegment(sketch, "E193.MirrorCS", {"start": v(51.5, -94.5) * mm, "end": v(122.5, -94.5) * mm});
            skLineSegment(sketch, "E194.MirrorCS", {"start": v(50, -72) * mm, "end": v(50, -72) * mm});
            skPoint(sketch, "E195.MirrorP", {"position": v(50, -97.5) * mm});
            skLineSegment(sketch, "E196.MirrorCS", {"start": v(122.5, -58.5) * mm, "end": v(51.5, -58.5) * mm});
            skLineSegment(sketch, "E197", {"start": v(56.8, 84) * mm, "end": v(56.8, 84) * mm});
            skLineSegment(sketch, "E198", {"start": v(56.8, 78) * mm, "end": v(56.8, 78) * mm});
            skLineSegment(sketch, "E199", {"start": v(65.2, 84) * mm, "end": v(65.2, 84) * mm});
            skLineSegment(sketch, "E200", {"start": v(65.2, 78) * mm, "end": v(65.2, 78) * mm});
            skLineSegment(sketch, "E201", {"start": v(61, 87.48) * mm, "end": v(61, 75.46) * mm, "construction": true});
            skLineSegment(sketch, "E202", {"start": v(87, 90) * mm, "end": v(87, 72) * mm, "construction": true});
            skLineSegment(sketch, "E203.MirrorCS", {"start": v(108.8, 78) * mm, "end": v(108.8, 78) * mm});
            skLineSegment(sketch, "E204.MirrorCS", {"start": v(117.2, 78) * mm, "end": v(117.2, 78) * mm});
            skLineSegment(sketch, "E205.MirrorCS", {"start": v(117.2, 84) * mm, "end": v(117.2, 84) * mm});
            skLineSegment(sketch, "E206.MirrorCS", {"start": v(108.8, 84) * mm, "end": v(108.8, 84) * mm});
            skLineSegment(sketch, "E207.trimOffspring", {"start": v(55.3, 85.5) * mm, "end": v(51.5, 85.5) * mm});
            skLineSegment(sketch, "E208.trimOffspring", {"start": v(55.3, 82.5) * mm, "end": v(51.5, 82.5) * mm});
            skLineSegment(sketch, "E209.trimOffspring", {"start": v(55.3, 79.5) * mm, "end": v(51.5, 79.5) * mm});
            skLineSegment(sketch, "E210.trimOffspring", {"start": v(55.3, 76.5) * mm, "end": v(51.5, 76.5) * mm});
            skLineSegment(sketch, "E211.trimOffspring", {"start": v(107.3, 85.5) * mm, "end": v(66.7, 85.5) * mm});
            skLineSegment(sketch, "E212.trimOffspring", {"start": v(107.3, 82.5) * mm, "end": v(66.7, 82.5) * mm});
            skLineSegment(sketch, "E213.trimOffspring", {"start": v(107.3, 79.5) * mm, "end": v(87, 79.5) * mm});
            skLineSegment(sketch, "E214.trimOffspring", {"start": v(107.3, 76.5) * mm, "end": v(66.7, 76.5) * mm});
            skLineSegment(sketch, "E215", {"start": v(66.7, 79.5) * mm, "end": v(87, 79.5) * mm});
            skPoint(sketch, "E216.visualSharp", {"position": v(56.8, 85.5) * mm});
            skArc(sketch, "E216.filletArc", {"start": v(56.8, 84) * mm, "mid": v(56.36, 85.06) * mm, "end": v(55.3, 85.5) * mm});
            skPoint(sketch, "E217.visualSharp", {"position": v(56.8, 82.5) * mm});
            skArc(sketch, "E217.filletArc", {"start": v(55.3, 82.5) * mm, "mid": v(56.36, 82.94) * mm, "end": v(56.8, 84) * mm});
            skPoint(sketch, "E218.visualSharp", {"position": v(56.8, 79.5) * mm});
            skArc(sketch, "E218.filletArc", {"start": v(56.8, 78) * mm, "mid": v(56.36, 79.06) * mm, "end": v(55.3, 79.5) * mm});
            skPoint(sketch, "E219.visualSharp", {"position": v(56.8, 76.5) * mm});
            skArc(sketch, "E219.filletArc", {"start": v(55.3, 76.5) * mm, "mid": v(56.36, 76.94) * mm, "end": v(56.8, 78) * mm});
            skPoint(sketch, "E220.visualSharp", {"position": v(65.2, 85.5) * mm});
            skArc(sketch, "E220.filletArc", {"start": v(66.7, 85.5) * mm, "mid": v(65.64, 85.06) * mm, "end": v(65.2, 84) * mm});
            skPoint(sketch, "E221.visualSharp", {"position": v(65.2, 82.5) * mm});
            skArc(sketch, "E221.filletArc", {"start": v(65.2, 84) * mm, "mid": v(65.64, 82.94) * mm, "end": v(66.7, 82.5) * mm});
            skPoint(sketch, "E222.visualSharp", {"position": v(65.2, 79.5) * mm});
            skArc(sketch, "E222.filletArc", {"start": v(66.7, 79.5) * mm, "mid": v(65.64, 79.06) * mm, "end": v(65.2, 78) * mm});
            skPoint(sketch, "E223.visualSharp", {"position": v(65.2, 76.5) * mm});
            skArc(sketch, "E223.filletArc", {"start": v(65.2, 78) * mm, "mid": v(65.64, 76.94) * mm, "end": v(66.7, 76.5) * mm});
            skPoint(sketch, "E224.visualSharp", {"position": v(108.8, 85.5) * mm});
            skArc(sketch, "E224.filletArc", {"start": v(108.8, 84) * mm, "mid": v(108.36, 85.06) * mm, "end": v(107.3, 85.5) * mm});
            skPoint(sketch, "E225.visualSharp", {"position": v(108.8, 82.5) * mm});
            skArc(sketch, "E225.filletArc", {"start": v(107.3, 82.5) * mm, "mid": v(108.36, 82.94) * mm, "end": v(108.8, 84) * mm});
            skPoint(sketch, "E226.visualSharp", {"position": v(108.8, 79.5) * mm});
            skArc(sketch, "E226.filletArc", {"start": v(108.8, 78) * mm, "mid": v(108.36, 79.06) * mm, "end": v(107.3, 79.5) * mm});
            skPoint(sketch, "E227.visualSharp", {"position": v(108.8, 76.5) * mm});
            skArc(sketch, "E227.filletArc", {"start": v(107.3, 76.5) * mm, "mid": v(108.36, 76.94) * mm, "end": v(108.8, 78) * mm});
            skPoint(sketch, "E228.visualSharp", {"position": v(117.2, 85.5) * mm});
            skArc(sketch, "E228.filletArc", {"start": v(118.7, 85.5) * mm, "mid": v(117.64, 85.06) * mm, "end": v(117.2, 84) * mm});
            skPoint(sketch, "E229.visualSharp", {"position": v(117.2, 82.5) * mm});
            skArc(sketch, "E229.filletArc", {"start": v(117.2, 84) * mm, "mid": v(117.64, 82.94) * mm, "end": v(118.7, 82.5) * mm});
            skPoint(sketch, "E230.visualSharp", {"position": v(117.2, 79.5) * mm});
            skArc(sketch, "E230.filletArc", {"start": v(118.7, 79.5) * mm, "mid": v(117.64, 79.06) * mm, "end": v(117.2, 78) * mm});
            skPoint(sketch, "E231.visualSharp", {"position": v(117.2, 76.5) * mm});
            skArc(sketch, "E231.filletArc", {"start": v(117.2, 78) * mm, "mid": v(117.64, 76.94) * mm, "end": v(118.7, 76.5) * mm});
            skLineSegment(sketch, "E232.MirrorCS", {"start": v(122.5, -79.5) * mm, "end": v(118.7, -79.5) * mm});
            skArc(sketch, "E233.MirrorCS", {"start": v(50, -78) * mm, "mid": v(50.44, -76.94) * mm, "end": v(51.5, -76.5) * mm});
            skArc(sketch, "E234.MirrorCS", {"start": v(51.5, -79.5) * mm, "mid": v(50.44, -79.06) * mm, "end": v(50, -78) * mm});
            skArc(sketch, "E235.MirrorCS", {"start": v(55.3, -76.5) * mm, "mid": v(56.36, -76.94) * mm, "end": v(56.8, -78) * mm});
            skArc(sketch, "E236.MirrorCS", {"start": v(56.8, -78) * mm, "mid": v(56.36, -79.06) * mm, "end": v(55.3, -79.5) * mm});
            skArc(sketch, "E237.MirrorCS", {"start": v(66.7, -79.5) * mm, "mid": v(65.64, -79.06) * mm, "end": v(65.2, -78) * mm});
            skArc(sketch, "E238.MirrorCS", {"start": v(65.2, -78) * mm, "mid": v(65.64, -76.94) * mm, "end": v(66.7, -76.5) * mm});
            skLineSegment(sketch, "E239.MirrorCS", {"start": v(55.3, -76.5) * mm, "end": v(51.5, -76.5) * mm});
            skArc(sketch, "E240.MirrorCS", {"start": v(108.8, -78) * mm, "mid": v(108.36, -79.06) * mm, "end": v(107.3, -79.5) * mm});
            skArc(sketch, "E241.MirrorCS", {"start": v(117.2, -78) * mm, "mid": v(117.64, -76.94) * mm, "end": v(118.7, -76.5) * mm});
            skLineSegment(sketch, "E242.MirrorCS", {"start": v(122.5, -76.5) * mm, "end": v(118.7, -76.5) * mm});
            skArc(sketch, "E243.MirrorCS", {"start": v(118.7, -79.5) * mm, "mid": v(117.64, -79.06) * mm, "end": v(117.2, -78) * mm});
            skLineSegment(sketch, "E244.MirrorCS", {"start": v(55.3, -79.5) * mm, "end": v(51.5, -79.5) * mm});
            skArc(sketch, "E245.MirrorCS", {"start": v(122.5, -76.5) * mm, "mid": v(123.56, -76.94) * mm, "end": v(124, -78) * mm});
            skArc(sketch, "E246.MirrorCS", {"start": v(124, -78) * mm, "mid": v(123.56, -79.06) * mm, "end": v(122.5, -79.5) * mm});
            skArc(sketch, "E247.MirrorCS", {"start": v(107.3, -76.5) * mm, "mid": v(108.36, -76.94) * mm, "end": v(108.8, -78) * mm});
            skPoint(sketch, "E248.MirrorP", {"position": v(108.8, -82.5) * mm});
            skPoint(sketch, "E249.MirrorP", {"position": v(124, -82.5) * mm});
            skLineSegment(sketch, "E250.MirrorCS", {"start": v(50, -78) * mm, "end": v(50, -78) * mm});
            skLineSegment(sketch, "E251.MirrorCS", {"start": v(124, -78) * mm, "end": v(124, -78) * mm});
            skPoint(sketch, "E252.MirrorP", {"position": v(50, -82.5) * mm});
            skPoint(sketch, "E253.MirrorP", {"position": v(56.8, -82.5) * mm});
            skPoint(sketch, "E254.MirrorP", {"position": v(117.2, -82.5) * mm});
            skPoint(sketch, "E255.MirrorP", {"position": v(65.2, -82.5) * mm});
            skLineSegment(sketch, "E256.MirrorCS", {"start": v(56.8, -78) * mm, "end": v(56.8, -78) * mm});
            skLineSegment(sketch, "E257.MirrorCS", {"start": v(108.8, -78) * mm, "end": v(108.8, -78) * mm});
            skLineSegment(sketch, "E258.MirrorCS", {"start": v(65.2, -78) * mm, "end": v(65.2, -78) * mm});
            skLineSegment(sketch, "E259.MirrorCS", {"start": v(117.2, -78) * mm, "end": v(117.2, -78) * mm});
            skPoint(sketch, "E260.MirrorP", {"position": v(124, -79.5) * mm});
            skPoint(sketch, "E261.MirrorP", {"position": v(56.8, -79.5) * mm});
            skPoint(sketch, "E262.MirrorP", {"position": v(108.8, -79.5) * mm});
            skPoint(sketch, "E263.MirrorP", {"position": v(56.8, -76.5) * mm});
            skPoint(sketch, "E264.MirrorP", {"position": v(108.8, -76.5) * mm});
            skPoint(sketch, "E265.MirrorP", {"position": v(124, -76.5) * mm});
            skLineSegment(sketch, "E266.MirrorCS", {"start": v(107.3, -79.5) * mm, "end": v(87, -79.5) * mm});
            skLineSegment(sketch, "E267.MirrorCS", {"start": v(66.7, -79.5) * mm, "end": v(87, -79.5) * mm});
            skLineSegment(sketch, "E268.MirrorCS", {"start": v(46.43, -78) * mm, "end": v(128.5, -78) * mm, "construction": true});
            skLineSegment(sketch, "E269.MirrorCS", {"start": v(107.3, -76.5) * mm, "end": v(66.7, -76.5) * mm});
            skPoint(sketch, "E270.MirrorP", {"position": v(87, -78) * mm});
            skPoint(sketch, "E271.MirrorP", {"position": v(50, -79.5) * mm});
            skPoint(sketch, "E272.MirrorP", {"position": v(50, -76.5) * mm});
            skPoint(sketch, "E273.MirrorP", {"position": v(117.2, -79.5) * mm});
            skPoint(sketch, "E274.MirrorP", {"position": v(65.2, -79.5) * mm});
            skPoint(sketch, "E275.MirrorP", {"position": v(117.2, -76.5) * mm});
            skPoint(sketch, "E276.MirrorP", {"position": v(65.2, -76.5) * mm});
            skArc(sketch, "E277.MirrorCS", {"start": v(118.7, -85.5) * mm, "mid": v(117.64, -85.06) * mm, "end": v(117.2, -84) * mm});
            skArc(sketch, "E278.MirrorCS", {"start": v(66.7, -85.5) * mm, "mid": v(65.64, -85.06) * mm, "end": v(65.2, -84) * mm});
            skArc(sketch, "E279.MirrorCS", {"start": v(51.5, -85.5) * mm, "mid": v(50.44, -85.06) * mm, "end": v(50, -84) * mm});
            skArc(sketch, "E280.MirrorCS", {"start": v(108.8, -84) * mm, "mid": v(108.36, -85.06) * mm, "end": v(107.3, -85.5) * mm});
            skArc(sketch, "E281.MirrorCS", {"start": v(124, -84) * mm, "mid": v(123.56, -85.06) * mm, "end": v(122.5, -85.5) * mm});
            skLineSegment(sketch, "E282.MirrorCS", {"start": v(55.3, -85.5) * mm, "end": v(51.5, -85.5) * mm});
            skArc(sketch, "E283.MirrorCS", {"start": v(65.2, -84) * mm, "mid": v(65.64, -82.94) * mm, "end": v(66.7, -82.5) * mm});
            skArc(sketch, "E284.MirrorCS", {"start": v(117.2, -84) * mm, "mid": v(117.64, -82.94) * mm, "end": v(118.7, -82.5) * mm});
            skArc(sketch, "E285.MirrorCS", {"start": v(122.5, -82.5) * mm, "mid": v(123.56, -82.94) * mm, "end": v(124, -84) * mm});
            skLineSegment(sketch, "E286.MirrorCS", {"start": v(55.3, -82.5) * mm, "end": v(51.5, -82.5) * mm});
            skArc(sketch, "E287.MirrorCS", {"start": v(56.8, -84) * mm, "mid": v(56.36, -85.06) * mm, "end": v(55.3, -85.5) * mm});
            skArc(sketch, "E288.MirrorCS", {"start": v(55.3, -82.5) * mm, "mid": v(56.36, -82.94) * mm, "end": v(56.8, -84) * mm});
            skArc(sketch, "E289.MirrorCS", {"start": v(107.3, -82.5) * mm, "mid": v(108.36, -82.94) * mm, "end": v(108.8, -84) * mm});
            skArc(sketch, "E290.MirrorCS", {"start": v(50, -84) * mm, "mid": v(50.44, -82.94) * mm, "end": v(51.5, -82.5) * mm});
            skLineSegment(sketch, "E291.MirrorCS", {"start": v(122.5, -82.5) * mm, "end": v(118.7, -82.5) * mm});
            skLineSegment(sketch, "E292.MirrorCS", {"start": v(124, -84) * mm, "end": v(124, -84) * mm});
            skLineSegment(sketch, "E293.MirrorCS", {"start": v(56.8, -84) * mm, "end": v(56.8, -84) * mm});
            skLineSegment(sketch, "E294.MirrorCS", {"start": v(108.8, -84) * mm, "end": v(108.8, -84) * mm});
            skLineSegment(sketch, "E295.MirrorCS", {"start": v(65.2, -84) * mm, "end": v(65.2, -84) * mm});
            skLineSegment(sketch, "E296.MirrorCS", {"start": v(50, -84) * mm, "end": v(50, -84) * mm});
            skLineSegment(sketch, "E297.MirrorCS", {"start": v(117.2, -84) * mm, "end": v(117.2, -84) * mm});
            skPoint(sketch, "E298.MirrorP", {"position": v(50, -85.5) * mm});
            skPoint(sketch, "E299.MirrorP", {"position": v(56.8, -85.5) * mm});
            skPoint(sketch, "E300.MirrorP", {"position": v(108.8, -85.5) * mm});
            skPoint(sketch, "E301.MirrorP", {"position": v(124, -85.5) * mm});
            skPoint(sketch, "E302.MirrorP", {"position": v(117.2, -85.5) * mm});
            skPoint(sketch, "E303.MirrorP", {"position": v(65.2, -85.5) * mm});
            skLineSegment(sketch, "E304.MirrorCS", {"start": v(47.08, -84) * mm, "end": v(128.67, -84) * mm, "construction": true});
            skLineSegment(sketch, "E305.MirrorCS", {"start": v(107.3, -82.5) * mm, "end": v(66.7, -82.5) * mm});
            skPoint(sketch, "E306.MirrorP", {"position": v(87, -84) * mm});
            skLineSegment(sketch, "E307.MirrorCS", {"start": v(107.3, -85.5) * mm, "end": v(66.7, -85.5) * mm});
            skLineSegment(sketch, "E308.MirrorCS", {"start": v(122.5, -85.5) * mm, "end": v(118.7, -85.5) * mm});
            skSolve(sketch);
        }
        {
            var Q0;
            Q0=makeQuery(id+"F5.imprint","IMPRINT",FACE,{"disambiguationData":[TD([[makeQuery(id+"F5.imprint","IMPRINT",EDGE,{"derivedFrom":sQuery(id+"F5.wireOp",EDGE,"E100.bottom")}),-1.0]])]});
            var Q1;
            Q1=makeQuery(id+"F5.imprint","IMPRINT",FACE,{"disambiguationData":[TD([[makeQuery(id+"F5.imprint","IMPRINT",EDGE,{"derivedFrom":sQuery(id+"F5.wireOp",EDGE,"E94.bottom")}),-1.0]])]});
            var Q2;
            Q2=makeQuery(id+"F5.imprint","IMPRINT",FACE,{"disambiguationData":[TD([[makeQuery(id+"F5.imprint","IMPRINT",EDGE,{"derivedFrom":sQuery(id+"F5.wireOp",EDGE,"E95.bottom")}),-1.0]])]});
            var Q3;
            Q3=makeQuery(id+"F5.imprint","IMPRINT",FACE,{"disambiguationData":[TD([[makeQuery(id+"F5.imprint","IMPRINT",EDGE,{"derivedFrom":sQuery(id+"F5.wireOp",EDGE,"E96.bottom")}),-1.0]])]});
            var Q4;
            Q4=makeQuery(id+"F5.imprint","IMPRINT",FACE,{"disambiguationData":[TD([[makeQuery(id+"F5.imprint","IMPRINT",EDGE,{"derivedFrom":sQuery(id+"F5.wireOp",EDGE,"E97.bottom")}),-1.0]])]});
            var Q5;
            Q5=makeQuery(id+"F5.imprint","IMPRINT",FACE,{"disambiguationData":[TD([[makeQuery(id+"F5.imprint","IMPRINT",EDGE,{"derivedFrom":sQuery(id+"F5.wireOp",EDGE,"E98.bottom")}),-1.0]])]});
            var Q6;
            Q6=makeQuery(id+"F5.imprint","IMPRINT",FACE,{"disambiguationData":[TD([[makeQuery(id+"F5.imprint","IMPRINT",EDGE,{"derivedFrom":sQuery(id+"F5.wireOp",EDGE,"E99.bottom")}),-1.0]])]});
            var Q7;
            Q7=makeQuery(id+"F5.imprint","IMPRINT",FACE,{"disambiguationData":[TD([[makeQuery(id+"F5.imprint","IMPRINT",EDGE,{"derivedFrom":sQuery(id+"F5.wireOp",EDGE,"E133.MirrorCS")}),-1.0]])]});
            var Q8;
            Q8=makeQuery(id+"F5.imprint","IMPRINT",FACE,{"disambiguationData":[TD([[makeQuery(id+"F5.imprint","IMPRINT",EDGE,{"derivedFrom":sQuery(id+"F5.wireOp",EDGE,"E135.MirrorCS")}),-1.0]])]});
            var Q9;
            Q9=makeQuery(id+"F5.imprint","IMPRINT",FACE,{"disambiguationData":[TD([[makeQuery(id+"F5.imprint","IMPRINT",EDGE,{"derivedFrom":sQuery(id+"F5.wireOp",EDGE,"E129.MirrorCS")}),-1.0]])]});
            var Q10;
            Q10=makeQuery(id+"F5.imprint","IMPRINT",FACE,{"disambiguationData":[TD([[makeQuery(id+"F5.imprint","IMPRINT",EDGE,{"derivedFrom":sQuery(id+"F5.wireOp",EDGE,"305c0181-43c0-426a-b1aa-2cab068333554.MirrorCS")}),-1.0]])]});
            var Q11;
            Q11=makeQuery(id+"F5.imprint","IMPRINT",FACE,{"disambiguationData":[TD([[makeQuery(id+"F5.imprint","IMPRINT",EDGE,{"derivedFrom":sQuery(id+"F5.wireOp",EDGE,"305c0181-43c0-426a-b1aa-2cab068333553.MirrorCS")}),-1.0]])]});
            var Q12;
            Q12=makeQuery(id+"F5.imprint","IMPRINT",FACE,{"disambiguationData":[TD([[makeQuery(id+"F5.imprint","IMPRINT",EDGE,{"derivedFrom":sQuery(id+"F5.wireOp",EDGE,"E130.MirrorCS")}),-1.0]])]});
            var Q13;
            Q13=makeQuery(id+"F5.imprint","IMPRINT",FACE,{"disambiguationData":[TD([[makeQuery(id+"F5.imprint","IMPRINT",EDGE,{"derivedFrom":sQuery(id+"F5.wireOp",EDGE,"E134.MirrorCS")}),-1.0]])]});
            var Q14;
            Q14=makeQuery(id+"F5.imprint","IMPRINT",FACE,{"disambiguationData":[TD([[makeQuery(id+"F5.imprint","IMPRINT",EDGE,{"derivedFrom":sQuery(id+"F5.wireOp",EDGE,"E211.trimOffspring")}),1.0]])]});
            var Q15;
            Q15=makeQuery(id+"F5.imprint","IMPRINT",FACE,{"disambiguationData":[TD([[makeQuery(id+"F5.imprint","IMPRINT",EDGE,{"derivedFrom":sQuery(id+"F5.wireOp",EDGE,"E213.trimOffspring")}),1.0]])]});
            var Q16;
            Q16=makeQuery(id+"F5.imprint","IMPRINT",FACE,{"disambiguationData":[TD([[makeQuery(id+"F5.imprint","IMPRINT",EDGE,{"derivedFrom":sQuery(id+"F5.wireOp",EDGE,"E104.filletArc")}),1.0]])]});
            var Q17;
            Q17=makeQuery(id+"F5.imprint","IMPRINT",FACE,{"disambiguationData":[TD([[makeQuery(id+"F5.imprint","IMPRINT",EDGE,{"derivedFrom":sQuery(id+"F5.wireOp",EDGE,"E107.filletArc")}),1.0]])]});
            var Q18;
            Q18=makeQuery(id+"F5.imprint","IMPRINT",FACE,{"disambiguationData":[TD([[makeQuery(id+"F5.imprint","IMPRINT",EDGE,{"derivedFrom":sQuery(id+"F5.wireOp",EDGE,"E232.MirrorCS")}),-1.0]])]});
            var Q19;
            Q19=makeQuery(id+"F5.imprint","IMPRINT",FACE,{"disambiguationData":[TD([[makeQuery(id+"F5.imprint","IMPRINT",EDGE,{"derivedFrom":sQuery(id+"F5.wireOp",EDGE,"E277.MirrorCS")}),-1.0]])]});
            var Q20;
            Q20=makeQuery(id+"F5.imprint","IMPRINT",FACE,{"disambiguationData":[TD([[makeQuery(id+"F5.imprint","IMPRINT",EDGE,{"derivedFrom":sQuery(id+"F5.wireOp",EDGE,"E237.MirrorCS")}),-1.0]])]});
            var Q21;
            Q21=makeQuery(id+"F5.imprint","IMPRINT",FACE,{"disambiguationData":[TD([[makeQuery(id+"F5.imprint","IMPRINT",EDGE,{"derivedFrom":sQuery(id+"F5.wireOp",EDGE,"E278.MirrorCS")}),-1.0]])]});
            var Q22;
            Q22=makeQuery(id+"F5.imprint","IMPRINT",FACE,{"disambiguationData":[TD([[makeQuery(id+"F5.imprint","IMPRINT",EDGE,{"derivedFrom":sQuery(id+"F5.wireOp",EDGE,"E233.MirrorCS")}),-1.0]])]});
            var Q23;
            Q23=makeQuery(id+"F5.imprint","IMPRINT",FACE,{"disambiguationData":[TD([[makeQuery(id+"F5.imprint","IMPRINT",EDGE,{"derivedFrom":sQuery(id+"F5.wireOp",EDGE,"E279.MirrorCS")}),-1.0]])]});
            extrude(context, id + "F6", {"entities" : qUnion([Q0, Q1, Q2, Q3, Q4, Q5, Q6, Q7, Q8, Q9, Q10, Q11, Q12, Q13, Q14, Q15, Q16, Q17, Q18, Q19, Q20, Q21, Q22, Q23]), "operationType" : NewBodyOperationType.REMOVE, "endBound" : BoundingType.THROUGH_ALL, "oppositeDirection" : true, "depth" : 25 * mm});
        }
        {
            var Q0;
            Q0=makeQuery(id+"F0.imprint","IMPRINT",FACE,{"disambiguationData":[TD([[makeQuery(id+"F0.imprint","IMPRINT",EDGE,{"derivedFrom":sQuery(id+"F0.wireOp",EDGE,"E0.bottom")}),-1.0]])]});
            var sketch = newSketch(context, id + "F7", { "sketchPlane" : qUnion([Q0])});
            skLineSegment(sketch, "E309", {"start": v(-226.2, 112.39) * mm, "end": v(218.78, 112.39) * mm, "construction": true});
            skLineSegment(sketch, "E310", {"start": v(-237.08, -111.77) * mm, "end": v(225.9, -111.77) * mm, "construction": true});
            skLineSegment(sketch, "E311", {"start": v(-169.89, 137.24) * mm, "end": v(-169.9, -142.8) * mm, "construction": true});
            skLineSegment(sketch, "E312", {"start": v(-155.95, 137.99) * mm, "end": v(-155.95, -143.55) * mm, "construction": true});
            skLineSegment(sketch, "E313", {"start": v(-232.2, 0) * mm, "end": v(208.28, 0) * mm, "construction": true});
            skLineSegment(sketch, "E314", {"start": v(-74.6, 146.23) * mm, "end": v(-74.6, -143.55) * mm, "construction": true});
            skLineSegment(sketch, "E315", {"start": v(10.45, 149.6) * mm, "end": v(10.45, -150.3) * mm, "construction": true});
            skLineSegment(sketch, "E316", {"start": v(21.89, 146.6) * mm, "end": v(21.9, -140.55) * mm, "construction": true});
            skPoint(sketch, "E317", {"position": v(-169.89, -111.77) * mm});
            skPoint(sketch, "E318", {"position": v(-74.6, -111.77) * mm});
            skPoint(sketch, "E319", {"position": v(21.9, -111.77) * mm});
            skPoint(sketch, "E320", {"position": v(10.45, 0) * mm});
            skPoint(sketch, "E321", {"position": v(-155.95, 0) * mm});
            skPoint(sketch, "E322", {"position": v(-169.89, 112.39) * mm});
            skPoint(sketch, "E323", {"position": v(-74.6, 112.39) * mm});
            skPoint(sketch, "E324", {"position": v(21.89, 112.39) * mm});
            skPoint(sketch, "E325", {"position": v(-74.6, 0) * mm});
            skSolve(sketch);
        }
        {
            var Q0;
            Q0=sQuery(id+"F7.wireOp",VERTEX,"E317");
            var Q1;
            Q1=sQuery(id+"F7.wireOp",VERTEX,"E318");
            var Q2;
            Q2=sQuery(id+"F7.wireOp",VERTEX,"E319");
            var Q3;
            Q3=sQuery(id+"F7.wireOp",VERTEX,"E320");
            var Q4;
            Q4=sQuery(id+"F7.wireOp",VERTEX,"E321");
            var Q5;
            Q5=sQuery(id+"F7.wireOp",VERTEX,"E322");
            var Q6;
            Q6=sQuery(id+"F7.wireOp",VERTEX,"E323");
            var Q7;
            Q7=sQuery(id+"F7.wireOp",VERTEX,"E324");
            var Q8;
            Q8=sQuery(id+"F7.wireOp",VERTEX,"E325");
            var Q9;
            Q9=makeQuery(id+"F1.opExtrude","SWEPT_BODY",BODY,{"disambiguationData":[OSD([sQuery(id+"F0.wireOp",EDGE,"E0.bottom"),sQuery(id+"F0.wireOp",EDGE,"E0.top"),sQuery(id+"F0.wireOp",EDGE,"E0.left"),sQuery(id+"F0.wireOp",EDGE,"E0.right"),sQuery(id+"F0.wireOp",EDGE,"E10"),sQuery(id+"F0.wireOp",EDGE,"E11"),sQuery(id+"F0.wireOp",EDGE,"E12"),sQuery(id+"F0.wireOp",EDGE,"E13"),sQuery(id+"F0.wireOp",EDGE,"E14"),sQuery(id+"F0.wireOp",EDGE,"E15"),sQuery(id+"F0.wireOp",EDGE,"E16.bottom"),sQuery(id+"F0.wireOp",EDGE,"E16.top"),sQuery(id+"F0.wireOp",EDGE,"E16.left"),sQuery(id+"F0.wireOp",EDGE,"E16.right"),sQuery(id+"F0.wireOp",EDGE,"E21"),sQuery(id+"F0.wireOp",EDGE,"E22"),sQuery(id+"F0.wireOp",EDGE,"E23"),sQuery(id+"F0.wireOp",EDGE,"E24")])]});
            hole(context, id + "F8", {"style" : HoleStyle.C_BORE, "endStyle" : HoleEndStyle.THROUGH, "holeDiameter" : 3.5 * mm, "cBoreDiameter" : 6.5 * mm, "cBoreDepth" : 2 * mm, "locations" : qUnion([Q0, Q1, Q2, Q3, Q4, Q5, Q6, Q7, Q8]), "scope" : qUnion([Q9]), "isTappedThrough" : true});
        }
    });
